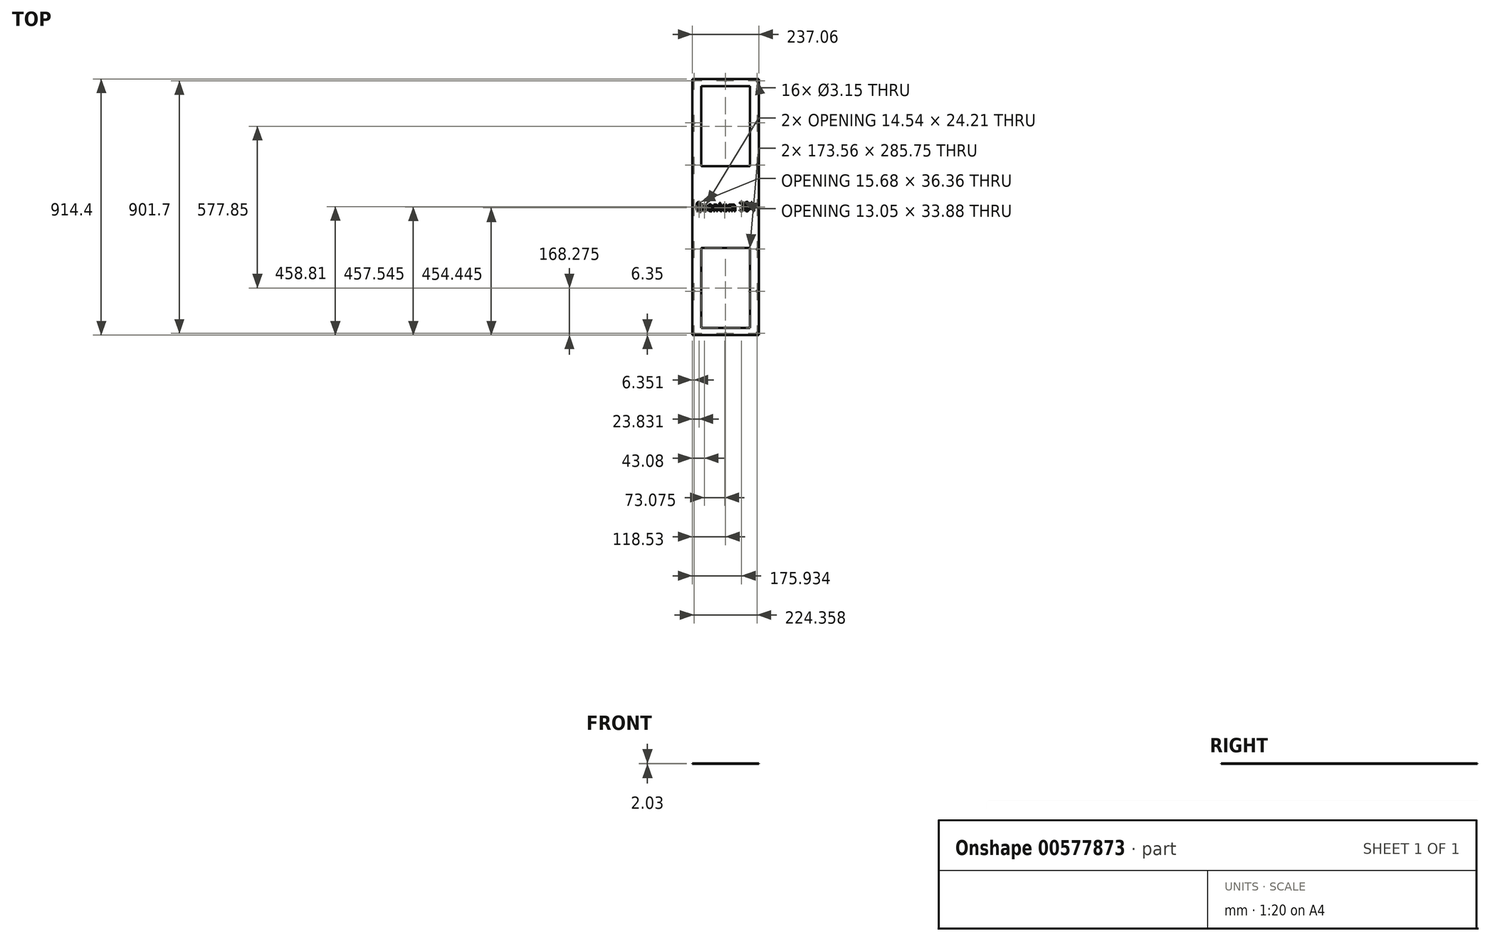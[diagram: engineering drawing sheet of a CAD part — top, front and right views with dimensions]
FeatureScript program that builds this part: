
annotation { "Feature Type Name" : "Feature", "Feature Type Description" : "" }
export const myFeature = defineFeature(function(context is Context, id is Id, definition is map)
    precondition{}
    {
        {
            var Q0;
            Q0=qCreatedBy(makeId("Top.planeOp"),FACE);
            var sketch = newSketch(context, id + "F0", { "sketchPlane" : qUnion([Q0])});
            skLineSegment(sketch, "E0", {"start": v(-118.53, -457.2) * mm, "end": v(118.53, -457.2) * mm});
            skLineSegment(sketch, "E1", {"start": v(-118.53, 457.2) * mm, "end": v(118.53, 457.2) * mm});
            skLineSegment(sketch, "E2", {"start": v(-118.53, 457.2) * mm, "end": v(-118.53, -457.2) * mm});
            skLineSegment(sketch, "E3", {"start": v(118.53, 457.2) * mm, "end": v(118.53, -457.2) * mm});
            skLineSegment(sketch, "E4", {"start": v(-86.78, 431.8) * mm, "end": v(86.78, 431.8) * mm});
            skLineSegment(sketch, "E5", {"start": v(-86.78, 146.05) * mm, "end": v(86.78, 146.05) * mm});
            skLineSegment(sketch, "E6", {"start": v(-86.78, 431.8) * mm, "end": v(-86.78, 146.05) * mm});
            skLineSegment(sketch, "E7", {"start": v(86.78, 431.8) * mm, "end": v(86.78, 146.05) * mm});
            skLineSegment(sketch, "E8", {"start": v(-86.78, -146.05) * mm, "end": v(86.78, -146.05) * mm});
            skLineSegment(sketch, "E9", {"start": v(-86.78, -431.8) * mm, "end": v(86.78, -431.8) * mm});
            skLineSegment(sketch, "E10", {"start": v(-86.78, -146.05) * mm, "end": v(-86.78, -431.8) * mm});
            skLineSegment(sketch, "E11", {"start": v(86.78, -146.05) * mm, "end": v(86.78, -431.8) * mm});
            skCircle(sketch, "E12", {"center": v(-112.18, 450.85) * mm, "radius": 1.58 * mm});
            skCircle(sketch, "E13", {"center": v(-112.18, -450.85) * mm, "radius": 1.58 * mm});
            skCircle(sketch, "E14", {"center": v(112.18, -450.85) * mm, "radius": 1.58 * mm});
            skCircle(sketch, "E15", {"center": v(112.18, 450.85) * mm, "radius": 1.58 * mm});
            skCircle(sketch, "E16", {"center": v(0, 450.85) * mm, "radius": 1.58 * mm});
            skCircle(sketch, "E17", {"center": v(0, -450.85) * mm, "radius": 1.58 * mm});
            skCircle(sketch, "E18", {"center": v(-112.18, 0) * mm, "radius": 1.58 * mm});
            skCircle(sketch, "E19", {"center": v(112.18, 0) * mm, "radius": 1.58 * mm});
            skCircle(sketch, "E20", {"center": v(-112.18, 300.57) * mm, "radius": 1.58 * mm});
            skCircle(sketch, "E21", {"center": v(-112.18, 150.28) * mm, "radius": 1.58 * mm});
            skCircle(sketch, "E22", {"center": v(112.18, 300.57) * mm, "radius": 1.58 * mm});
            skCircle(sketch, "E23", {"center": v(112.18, 150.28) * mm, "radius": 1.58 * mm});
            skCircle(sketch, "E24", {"center": v(-112.18, -150.28) * mm, "radius": 1.58 * mm});
            skCircle(sketch, "E25", {"center": v(112.18, -150.28) * mm, "radius": 1.58 * mm});
            skCircle(sketch, "E26", {"center": v(112.18, -300.57) * mm, "radius": 1.58 * mm});
            skCircle(sketch, "E27", {"center": v(-112.18, -300.57) * mm, "radius": 1.58 * mm});
            skLineSegment(sketch, "E28", {"start": v(-102.51, 12) * mm, "end": v(-102.41, 12.72) * mm});
            skLineSegment(sketch, "E29", {"start": v(-102.41, 12.72) * mm, "end": v(-102.24, 13.4) * mm});
            skLineSegment(sketch, "E30", {"start": v(-102.24, 13.4) * mm, "end": v(-102.02, 14.06) * mm});
            skLineSegment(sketch, "E31", {"start": v(-102.02, 14.06) * mm, "end": v(-101.7, 14.68) * mm});
            skLineSegment(sketch, "E32", {"start": v(-101.7, 14.68) * mm, "end": v(-101.35, 15.28) * mm});
            skLineSegment(sketch, "E33", {"start": v(-101.35, 15.28) * mm, "end": v(-100.9, 15.85) * mm});
            skLineSegment(sketch, "E34", {"start": v(-100.9, 15.85) * mm, "end": v(-100.4, 16.4) * mm});
            skLineSegment(sketch, "E35", {"start": v(-100.4, 16.4) * mm, "end": v(-99.86, 16.9) * mm});
            skLineSegment(sketch, "E36", {"start": v(-99.86, 16.9) * mm, "end": v(-99.29, 17.34) * mm});
            skLineSegment(sketch, "E37", {"start": v(-99.29, 17.34) * mm, "end": v(-98.7, 17.68) * mm});
            skLineSegment(sketch, "E38", {"start": v(-98.7, 17.68) * mm, "end": v(-98.07, 18) * mm});
            skLineSegment(sketch, "E39", {"start": v(-98.07, 18) * mm, "end": v(-97.4, 18.23) * mm});
            skLineSegment(sketch, "E40", {"start": v(-97.4, 18.23) * mm, "end": v(-96.73, 18.4) * mm});
            skLineSegment(sketch, "E41", {"start": v(-96.73, 18.4) * mm, "end": v(-96.01, 18.5) * mm});
            skLineSegment(sketch, "E42", {"start": v(-96.01, 18.5) * mm, "end": v(-95.27, 18.53) * mm});
            skLineSegment(sketch, "E43", {"start": v(-95.27, 18.53) * mm, "end": v(-94.55, 18.5) * mm});
            skLineSegment(sketch, "E44", {"start": v(-94.55, 18.5) * mm, "end": v(-93.83, 18.4) * mm});
            skLineSegment(sketch, "E45", {"start": v(-93.83, 18.4) * mm, "end": v(-93.16, 18.23) * mm});
            skLineSegment(sketch, "E46", {"start": v(-93.16, 18.23) * mm, "end": v(-92.5, 18) * mm});
            skLineSegment(sketch, "E47", {"start": v(-92.5, 18) * mm, "end": v(-91.87, 17.68) * mm});
            skLineSegment(sketch, "E48", {"start": v(-91.87, 17.68) * mm, "end": v(-91.28, 17.34) * mm});
            skLineSegment(sketch, "E49", {"start": v(-91.28, 17.34) * mm, "end": v(-90.7, 16.9) * mm});
            skLineSegment(sketch, "E50", {"start": v(-90.7, 16.9) * mm, "end": v(-90.16, 16.4) * mm});
            skLineSegment(sketch, "E51", {"start": v(-90.16, 16.4) * mm, "end": v(-89.66, 15.85) * mm});
            skLineSegment(sketch, "E52", {"start": v(-89.66, 15.85) * mm, "end": v(-89.22, 15.28) * mm});
            skLineSegment(sketch, "E53", {"start": v(-89.22, 15.28) * mm, "end": v(-88.87, 14.68) * mm});
            skLineSegment(sketch, "E54", {"start": v(-88.87, 14.68) * mm, "end": v(-88.55, 14.06) * mm});
            skLineSegment(sketch, "E55", {"start": v(-88.55, 14.06) * mm, "end": v(-88.32, 13.4) * mm});
            skLineSegment(sketch, "E56", {"start": v(-88.32, 13.4) * mm, "end": v(-88.15, 12.72) * mm});
            skLineSegment(sketch, "E57", {"start": v(-88.15, 12.72) * mm, "end": v(-88.05, 12) * mm});
            skLineSegment(sketch, "E58", {"start": v(-88.05, 12) * mm, "end": v(-88.03, 11.28) * mm});
            skLineSegment(sketch, "E59", {"start": v(-88.03, 11.28) * mm, "end": v(-88.03, -8.06) * mm});
            skLineSegment(sketch, "E60", {"start": v(-88.03, -8.06) * mm, "end": v(-88.03, -8.29) * mm});
            skLineSegment(sketch, "E61", {"start": v(-88.03, -8.29) * mm, "end": v(-88.03, -8.5) * mm});
            skLineSegment(sketch, "E62", {"start": v(-88.03, -8.5) * mm, "end": v(-88.05, -8.73) * mm});
            skLineSegment(sketch, "E63", {"start": v(-88.05, -8.73) * mm, "end": v(-88.08, -8.96) * mm});
            skLineSegment(sketch, "E64", {"start": v(-88.08, -8.96) * mm, "end": v(-88.1, -9.15) * mm});
            skLineSegment(sketch, "E65", {"start": v(-88.1, -9.15) * mm, "end": v(-88.13, -9.38) * mm});
            skLineSegment(sketch, "E66", {"start": v(-88.13, -9.38) * mm, "end": v(-88.15, -9.58) * mm});
            skLineSegment(sketch, "E67", {"start": v(-88.15, -9.58) * mm, "end": v(-88.2, -9.8) * mm});
            skLineSegment(sketch, "E68", {"start": v(-88.2, -9.8) * mm, "end": v(-88.22, -9.92) * mm});
            skLineSegment(sketch, "E69", {"start": v(-88.22, -9.92) * mm, "end": v(-88.27, -10.07) * mm});
            skLineSegment(sketch, "E70", {"start": v(-88.27, -10.07) * mm, "end": v(-88.32, -10.2) * mm});
            skLineSegment(sketch, "E71", {"start": v(-88.32, -10.2) * mm, "end": v(-88.37, -10.32) * mm});
            skLineSegment(sketch, "E72", {"start": v(-88.37, -10.32) * mm, "end": v(-88.45, -10.42) * mm});
            skLineSegment(sketch, "E73", {"start": v(-88.45, -10.42) * mm, "end": v(-88.52, -10.54) * mm});
            skLineSegment(sketch, "E74", {"start": v(-88.52, -10.54) * mm, "end": v(-88.62, -10.64) * mm});
            skLineSegment(sketch, "E75", {"start": v(-88.62, -10.64) * mm, "end": v(-88.72, -10.77) * mm});
            skLineSegment(sketch, "E76", {"start": v(-88.72, -10.77) * mm, "end": v(-88.87, -10.9) * mm});
            skLineSegment(sketch, "E77", {"start": v(-88.87, -10.9) * mm, "end": v(-89.04, -11.02) * mm});
            skLineSegment(sketch, "E78", {"start": v(-89.04, -11.02) * mm, "end": v(-89.2, -11.11) * mm});
            skLineSegment(sketch, "E79", {"start": v(-89.2, -11.11) * mm, "end": v(-89.37, -11.19) * mm});
            skLineSegment(sketch, "E80", {"start": v(-89.37, -11.19) * mm, "end": v(-89.54, -11.26) * mm});
            skLineSegment(sketch, "E81", {"start": v(-89.54, -11.26) * mm, "end": v(-89.71, -11.31) * mm});
            skLineSegment(sketch, "E82", {"start": v(-89.71, -11.31) * mm, "end": v(-89.91, -11.34) * mm});
            skLineSegment(sketch, "E83", {"start": v(-89.91, -11.34) * mm, "end": v(-90.1, -11.34) * mm});
            skLineSegment(sketch, "E84", {"start": v(-90.1, -11.34) * mm, "end": v(-90.3, -11.34) * mm});
            skLineSegment(sketch, "E85", {"start": v(-90.3, -11.34) * mm, "end": v(-90.48, -11.31) * mm});
            skLineSegment(sketch, "E86", {"start": v(-90.48, -11.31) * mm, "end": v(-90.68, -11.26) * mm});
            skLineSegment(sketch, "E87", {"start": v(-90.68, -11.26) * mm, "end": v(-90.85, -11.19) * mm});
            skLineSegment(sketch, "E88", {"start": v(-90.85, -11.19) * mm, "end": v(-91, -11.11) * mm});
            skLineSegment(sketch, "E89", {"start": v(-91, -11.11) * mm, "end": v(-91.18, -11.02) * mm});
            skLineSegment(sketch, "E90", {"start": v(-91.18, -11.02) * mm, "end": v(-91.33, -10.92) * mm});
            skLineSegment(sketch, "E91", {"start": v(-91.33, -10.92) * mm, "end": v(-91.47, -10.77) * mm});
            skLineSegment(sketch, "E92", {"start": v(-91.47, -10.77) * mm, "end": v(-91.6, -10.62) * mm});
            skLineSegment(sketch, "E93", {"start": v(-91.6, -10.62) * mm, "end": v(-91.72, -10.47) * mm});
            skLineSegment(sketch, "E94", {"start": v(-91.72, -10.47) * mm, "end": v(-91.82, -10.32) * mm});
            skLineSegment(sketch, "E95", {"start": v(-91.82, -10.32) * mm, "end": v(-91.9, -10.15) * mm});
            skLineSegment(sketch, "E96", {"start": v(-91.9, -10.15) * mm, "end": v(-91.97, -9.97) * mm});
            skLineSegment(sketch, "E97", {"start": v(-91.97, -9.97) * mm, "end": v(-92, -9.8) * mm});
            skLineSegment(sketch, "E98", {"start": v(-92, -9.8) * mm, "end": v(-92.02, -9.6) * mm});
            skLineSegment(sketch, "E99", {"start": v(-92.02, -9.6) * mm, "end": v(-92.04, -9.4) * mm});
            skLineSegment(sketch, "E100", {"start": v(-92.04, -9.4) * mm, "end": v(-92.04, -9.35) * mm});
            skLineSegment(sketch, "E101", {"start": v(-92.04, -9.35) * mm, "end": v(-92.04, -9.3) * mm});
            skLineSegment(sketch, "E102", {"start": v(-92.04, -9.3) * mm, "end": v(-92.04, -9.25) * mm});
            skLineSegment(sketch, "E103", {"start": v(-92.04, -9.25) * mm, "end": v(-92.04, -9.2) * mm});
            skLineSegment(sketch, "E104", {"start": v(-92.04, -9.2) * mm, "end": v(-92.02, -9.15) * mm});
            skLineSegment(sketch, "E105", {"start": v(-92.02, -9.15) * mm, "end": v(-92.02, -9.08) * mm});
            skLineSegment(sketch, "E106", {"start": v(-92.02, -9.08) * mm, "end": v(-92.02, -9.03) * mm});
            skLineSegment(sketch, "E107", {"start": v(-92.02, -9.03) * mm, "end": v(-92.02, -8.98) * mm});
            skLineSegment(sketch, "E108", {"start": v(-92.02, -8.98) * mm, "end": v(-92, -8.86) * mm});
            skLineSegment(sketch, "E109", {"start": v(-92, -8.86) * mm, "end": v(-91.97, -8.76) * mm});
            skLineSegment(sketch, "E110", {"start": v(-91.97, -8.76) * mm, "end": v(-91.95, -8.63) * mm});
            skLineSegment(sketch, "E111", {"start": v(-91.95, -8.63) * mm, "end": v(-91.92, -8.53) * mm});
            skLineSegment(sketch, "E112", {"start": v(-91.92, -8.53) * mm, "end": v(-91.92, -8.41) * mm});
            skLineSegment(sketch, "E113", {"start": v(-91.92, -8.41) * mm, "end": v(-91.9, -8.31) * mm});
            skLineSegment(sketch, "E114", {"start": v(-91.9, -8.31) * mm, "end": v(-91.9, -8.19) * mm});
            skLineSegment(sketch, "E115", {"start": v(-91.9, -8.19) * mm, "end": v(-91.9, -8.06) * mm});
            skLineSegment(sketch, "E116", {"start": v(-91.9, -8.06) * mm, "end": v(-91.9, 11.28) * mm});
            skLineSegment(sketch, "E117", {"start": v(-91.9, 11.28) * mm, "end": v(-91.92, 11.6) * mm});
            skLineSegment(sketch, "E118", {"start": v(-91.92, 11.6) * mm, "end": v(-91.95, 11.95) * mm});
            skLineSegment(sketch, "E119", {"start": v(-91.95, 11.95) * mm, "end": v(-92.04, 12.28) * mm});
            skLineSegment(sketch, "E120", {"start": v(-92.04, 12.28) * mm, "end": v(-92.14, 12.57) * mm});
            skLineSegment(sketch, "E121", {"start": v(-92.14, 12.57) * mm, "end": v(-92.3, 12.87) * mm});
            skLineSegment(sketch, "E122", {"start": v(-92.3, 12.87) * mm, "end": v(-92.44, 13.14) * mm});
            skLineSegment(sketch, "E123", {"start": v(-92.44, 13.14) * mm, "end": v(-92.66, 13.42) * mm});
            skLineSegment(sketch, "E124", {"start": v(-92.66, 13.42) * mm, "end": v(-92.89, 13.67) * mm});
            skLineSegment(sketch, "E125", {"start": v(-92.89, 13.67) * mm, "end": v(-93.14, 13.89) * mm});
            skLineSegment(sketch, "E126", {"start": v(-93.14, 13.89) * mm, "end": v(-93.4, 14.11) * mm});
            skLineSegment(sketch, "E127", {"start": v(-93.4, 14.11) * mm, "end": v(-93.68, 14.26) * mm});
            skLineSegment(sketch, "E128", {"start": v(-93.68, 14.26) * mm, "end": v(-93.98, 14.4) * mm});
            skLineSegment(sketch, "E129", {"start": v(-93.98, 14.4) * mm, "end": v(-94.28, 14.5) * mm});
            skLineSegment(sketch, "E130", {"start": v(-94.28, 14.5) * mm, "end": v(-94.6, 14.6) * mm});
            skLineSegment(sketch, "E131", {"start": v(-94.6, 14.6) * mm, "end": v(-94.95, 14.63) * mm});
            skLineSegment(sketch, "E132", {"start": v(-94.95, 14.63) * mm, "end": v(-95.27, 14.66) * mm});
            skLineSegment(sketch, "E133", {"start": v(-95.27, 14.66) * mm, "end": v(-95.62, 14.63) * mm});
            skLineSegment(sketch, "E134", {"start": v(-95.62, 14.63) * mm, "end": v(-95.96, 14.6) * mm});
            skLineSegment(sketch, "E135", {"start": v(-95.96, 14.6) * mm, "end": v(-96.29, 14.5) * mm});
            skLineSegment(sketch, "E136", {"start": v(-96.29, 14.5) * mm, "end": v(-96.58, 14.4) * mm});
            skLineSegment(sketch, "E137", {"start": v(-96.58, 14.4) * mm, "end": v(-96.88, 14.26) * mm});
            skLineSegment(sketch, "E138", {"start": v(-96.88, 14.26) * mm, "end": v(-97.15, 14.11) * mm});
            skLineSegment(sketch, "E139", {"start": v(-97.15, 14.11) * mm, "end": v(-97.43, 13.89) * mm});
            skLineSegment(sketch, "E140", {"start": v(-97.43, 13.89) * mm, "end": v(-97.68, 13.67) * mm});
            skLineSegment(sketch, "E141", {"start": v(-97.68, 13.67) * mm, "end": v(-97.9, 13.42) * mm});
            skLineSegment(sketch, "E142", {"start": v(-97.9, 13.42) * mm, "end": v(-98.12, 13.14) * mm});
            skLineSegment(sketch, "E143", {"start": v(-98.12, 13.14) * mm, "end": v(-98.27, 12.87) * mm});
            skLineSegment(sketch, "E144", {"start": v(-98.27, 12.87) * mm, "end": v(-98.42, 12.57) * mm});
            skLineSegment(sketch, "E145", {"start": v(-98.42, 12.57) * mm, "end": v(-98.52, 12.28) * mm});
            skLineSegment(sketch, "E146", {"start": v(-98.52, 12.28) * mm, "end": v(-98.62, 11.95) * mm});
            skLineSegment(sketch, "E147", {"start": v(-98.62, 11.95) * mm, "end": v(-98.64, 11.6) * mm});
            skLineSegment(sketch, "E148", {"start": v(-98.64, 11.6) * mm, "end": v(-98.67, 11.28) * mm});
            skLineSegment(sketch, "E149", {"start": v(-98.67, 11.28) * mm, "end": v(-98.67, -8.06) * mm});
            skLineSegment(sketch, "E150", {"start": v(-98.67, -8.06) * mm, "end": v(-98.64, -8.41) * mm});
            skLineSegment(sketch, "E151", {"start": v(-98.64, -8.41) * mm, "end": v(-98.62, -8.73) * mm});
            skLineSegment(sketch, "E152", {"start": v(-98.62, -8.73) * mm, "end": v(-98.54, -9.03) * mm});
            skLineSegment(sketch, "E153", {"start": v(-98.54, -9.03) * mm, "end": v(-98.44, -9.33) * mm});
            skLineSegment(sketch, "E154", {"start": v(-98.44, -9.33) * mm, "end": v(-98.3, -9.6) * mm});
            skLineSegment(sketch, "E155", {"start": v(-98.3, -9.6) * mm, "end": v(-98.15, -9.85) * mm});
            skLineSegment(sketch, "E156", {"start": v(-98.15, -9.85) * mm, "end": v(-97.95, -10.1) * mm});
            skLineSegment(sketch, "E157", {"start": v(-97.95, -10.1) * mm, "end": v(-97.72, -10.32) * mm});
            skLineSegment(sketch, "E158", {"start": v(-97.72, -10.32) * mm, "end": v(-97.5, -10.52) * mm});
            skLineSegment(sketch, "E159", {"start": v(-97.5, -10.52) * mm, "end": v(-97.25, -10.72) * mm});
            skLineSegment(sketch, "E160", {"start": v(-97.25, -10.72) * mm, "end": v(-97, -10.9) * mm});
            skLineSegment(sketch, "E161", {"start": v(-97, -10.9) * mm, "end": v(-96.73, -11.04) * mm});
            skLineSegment(sketch, "E162", {"start": v(-96.73, -11.04) * mm, "end": v(-96.48, -11.16) * mm});
            skLineSegment(sketch, "E163", {"start": v(-96.48, -11.16) * mm, "end": v(-96.19, -11.29) * mm});
            skLineSegment(sketch, "E164", {"start": v(-96.19, -11.29) * mm, "end": v(-95.91, -11.39) * mm});
            skLineSegment(sketch, "E165", {"start": v(-95.91, -11.39) * mm, "end": v(-95.62, -11.49) * mm});
            skLineSegment(sketch, "E166", {"start": v(-95.62, -11.49) * mm, "end": v(-88.2, -14.07) * mm});
            skLineSegment(sketch, "E167", {"start": v(-88.2, -14.07) * mm, "end": v(-88, -14.14) * mm});
            skLineSegment(sketch, "E168", {"start": v(-88, -14.14) * mm, "end": v(-87.83, -14.24) * mm});
            skLineSegment(sketch, "E169", {"start": v(-87.83, -14.24) * mm, "end": v(-87.68, -14.34) * mm});
            skLineSegment(sketch, "E170", {"start": v(-87.68, -14.34) * mm, "end": v(-87.53, -14.46) * mm});
            skLineSegment(sketch, "E171", {"start": v(-87.53, -14.46) * mm, "end": v(-87.38, -14.59) * mm});
            skLineSegment(sketch, "E172", {"start": v(-87.38, -14.59) * mm, "end": v(-87.26, -14.74) * mm});
            skLineSegment(sketch, "E173", {"start": v(-87.26, -14.74) * mm, "end": v(-87.16, -14.88) * mm});
            skLineSegment(sketch, "E174", {"start": v(-87.16, -14.88) * mm, "end": v(-87.06, -15.06) * mm});
            skLineSegment(sketch, "E175", {"start": v(-87.06, -15.06) * mm, "end": v(-87, -15.18) * mm});
            skLineSegment(sketch, "E176", {"start": v(-87, -15.18) * mm, "end": v(-86.98, -15.28) * mm});
            skLineSegment(sketch, "E177", {"start": v(-86.98, -15.28) * mm, "end": v(-86.93, -15.38) * mm});
            skLineSegment(sketch, "E178", {"start": v(-86.93, -15.38) * mm, "end": v(-86.91, -15.5) * mm});
            skLineSegment(sketch, "E179", {"start": v(-86.91, -15.5) * mm, "end": v(-86.89, -15.6) * mm});
            skLineSegment(sketch, "E180", {"start": v(-86.89, -15.6) * mm, "end": v(-86.89, -15.7) * mm});
            skLineSegment(sketch, "E181", {"start": v(-86.89, -15.7) * mm, "end": v(-86.86, -15.8) * mm});
            skLineSegment(sketch, "E182", {"start": v(-86.86, -15.8) * mm, "end": v(-86.86, -15.9) * mm});
            skLineSegment(sketch, "E183", {"start": v(-86.86, -15.9) * mm, "end": v(-86.86, -15.98) * mm});
            skLineSegment(sketch, "E184", {"start": v(-86.86, -15.98) * mm, "end": v(-86.86, -16.05) * mm});
            skLineSegment(sketch, "E185", {"start": v(-86.86, -16.05) * mm, "end": v(-86.89, -16.13) * mm});
            skLineSegment(sketch, "E186", {"start": v(-86.89, -16.13) * mm, "end": v(-86.89, -16.2) * mm});
            skLineSegment(sketch, "E187", {"start": v(-86.89, -16.2) * mm, "end": v(-86.91, -16.27) * mm});
            skLineSegment(sketch, "E188", {"start": v(-86.91, -16.27) * mm, "end": v(-86.91, -16.35) * mm});
            skLineSegment(sketch, "E189", {"start": v(-86.91, -16.35) * mm, "end": v(-86.93, -16.45) * mm});
            skLineSegment(sketch, "E190", {"start": v(-86.93, -16.45) * mm, "end": v(-86.96, -16.52) * mm});
            skLineSegment(sketch, "E191", {"start": v(-86.96, -16.52) * mm, "end": v(-87.03, -16.7) * mm});
            skLineSegment(sketch, "E192", {"start": v(-87.03, -16.7) * mm, "end": v(-87.13, -16.87) * mm});
            skLineSegment(sketch, "E193", {"start": v(-87.13, -16.87) * mm, "end": v(-87.23, -17.04) * mm});
            skLineSegment(sketch, "E194", {"start": v(-87.23, -17.04) * mm, "end": v(-87.33, -17.2) * mm});
            skLineSegment(sketch, "E195", {"start": v(-87.33, -17.2) * mm, "end": v(-87.48, -17.32) * mm});
            skLineSegment(sketch, "E196", {"start": v(-87.48, -17.32) * mm, "end": v(-87.63, -17.44) * mm});
            skLineSegment(sketch, "E197", {"start": v(-87.63, -17.44) * mm, "end": v(-87.78, -17.56) * mm});
            skLineSegment(sketch, "E198", {"start": v(-87.78, -17.56) * mm, "end": v(-87.95, -17.66) * mm});
            skLineSegment(sketch, "E199", {"start": v(-87.95, -17.66) * mm, "end": v(-88.05, -17.69) * mm});
            skLineSegment(sketch, "E200", {"start": v(-88.05, -17.69) * mm, "end": v(-88.18, -17.74) * mm});
            skLineSegment(sketch, "E201", {"start": v(-88.18, -17.74) * mm, "end": v(-88.27, -17.76) * mm});
            skLineSegment(sketch, "E202", {"start": v(-88.27, -17.76) * mm, "end": v(-88.37, -17.79) * mm});
            skLineSegment(sketch, "E203", {"start": v(-88.37, -17.79) * mm, "end": v(-88.5, -17.81) * mm});
            skLineSegment(sketch, "E204", {"start": v(-88.5, -17.81) * mm, "end": v(-88.6, -17.84) * mm});
            skLineSegment(sketch, "E205", {"start": v(-88.6, -17.84) * mm, "end": v(-88.7, -17.84) * mm});
            skLineSegment(sketch, "E206", {"start": v(-88.7, -17.84) * mm, "end": v(-88.8, -17.84) * mm});
            skLineSegment(sketch, "E207", {"start": v(-88.8, -17.84) * mm, "end": v(-88.87, -17.84) * mm});
            skLineSegment(sketch, "E208", {"start": v(-88.87, -17.84) * mm, "end": v(-88.97, -17.84) * mm});
            skLineSegment(sketch, "E209", {"start": v(-88.97, -17.84) * mm, "end": v(-89.04, -17.84) * mm});
            skLineSegment(sketch, "E210", {"start": v(-89.04, -17.84) * mm, "end": v(-89.12, -17.81) * mm});
            skLineSegment(sketch, "E211", {"start": v(-89.12, -17.81) * mm, "end": v(-89.2, -17.81) * mm});
            skLineSegment(sketch, "E212", {"start": v(-89.2, -17.81) * mm, "end": v(-89.27, -17.79) * mm});
            skLineSegment(sketch, "E213", {"start": v(-89.27, -17.79) * mm, "end": v(-89.34, -17.76) * mm});
            skLineSegment(sketch, "E214", {"start": v(-89.34, -17.76) * mm, "end": v(-89.44, -17.74) * mm});
            skLineSegment(sketch, "E215", {"start": v(-89.44, -17.74) * mm, "end": v(-97.2, -15.08) * mm});
            skLineSegment(sketch, "E216", {"start": v(-97.2, -15.08) * mm, "end": v(-97.7, -14.9) * mm});
            skLineSegment(sketch, "E217", {"start": v(-97.7, -14.9) * mm, "end": v(-98.15, -14.71) * mm});
            skLineSegment(sketch, "E218", {"start": v(-98.15, -14.71) * mm, "end": v(-98.6, -14.49) * mm});
            skLineSegment(sketch, "E219", {"start": v(-98.6, -14.49) * mm, "end": v(-98.99, -14.26) * mm});
            skLineSegment(sketch, "E220", {"start": v(-98.99, -14.26) * mm, "end": v(-99.39, -14.02) * mm});
            skLineSegment(sketch, "E221", {"start": v(-99.39, -14.02) * mm, "end": v(-99.76, -13.77) * mm});
            skLineSegment(sketch, "E222", {"start": v(-99.76, -13.77) * mm, "end": v(-100.08, -13.5) * mm});
            skLineSegment(sketch, "E223", {"start": v(-100.08, -13.5) * mm, "end": v(-100.4, -13.2) * mm});
            skLineSegment(sketch, "E224", {"start": v(-100.4, -13.2) * mm, "end": v(-100.9, -12.65) * mm});
            skLineSegment(sketch, "E225", {"start": v(-100.9, -12.65) * mm, "end": v(-101.35, -12.08) * mm});
            skLineSegment(sketch, "E226", {"start": v(-101.35, -12.08) * mm, "end": v(-101.7, -11.49) * mm});
            skLineSegment(sketch, "E227", {"start": v(-101.7, -11.49) * mm, "end": v(-102.02, -10.87) * mm});
            skLineSegment(sketch, "E228", {"start": v(-102.02, -10.87) * mm, "end": v(-102.24, -10.2) * mm});
            skLineSegment(sketch, "E229", {"start": v(-102.24, -10.2) * mm, "end": v(-102.41, -9.53) * mm});
            skLineSegment(sketch, "E230", {"start": v(-102.41, -9.53) * mm, "end": v(-102.51, -8.8) * mm});
            skLineSegment(sketch, "E231", {"start": v(-102.51, -8.8) * mm, "end": v(-102.54, -8.06) * mm});
            skLineSegment(sketch, "E232", {"start": v(-102.54, -8.06) * mm, "end": v(-102.54, 11.28) * mm});
            skLineSegment(sketch, "E233", {"start": v(-102.54, 11.28) * mm, "end": v(-102.51, 12) * mm});
            skLineSegment(sketch, "E234", {"start": v(-82.67, -8.34) * mm, "end": v(-82.72, -7.6) * mm});
            skLineSegment(sketch, "E235", {"start": v(-82.72, -7.6) * mm, "end": v(-82.72, 7.41) * mm});
            skLineSegment(sketch, "E236", {"start": v(-82.72, 7.41) * mm, "end": v(-82.7, 7.59) * mm});
            skLineSegment(sketch, "E237", {"start": v(-82.7, 7.59) * mm, "end": v(-82.67, 7.79) * mm});
            skLineSegment(sketch, "E238", {"start": v(-82.67, 7.79) * mm, "end": v(-82.62, 7.96) * mm});
            skLineSegment(sketch, "E239", {"start": v(-82.62, 7.96) * mm, "end": v(-82.57, 8.13) * mm});
            skLineSegment(sketch, "E240", {"start": v(-82.57, 8.13) * mm, "end": v(-82.5, 8.3) * mm});
            skLineSegment(sketch, "E241", {"start": v(-82.5, 8.3) * mm, "end": v(-82.4, 8.48) * mm});
            skLineSegment(sketch, "E242", {"start": v(-82.4, 8.48) * mm, "end": v(-82.27, 8.63) * mm});
            skLineSegment(sketch, "E243", {"start": v(-82.27, 8.63) * mm, "end": v(-82.15, 8.78) * mm});
            skLineSegment(sketch, "E244", {"start": v(-82.15, 8.78) * mm, "end": v(-82, 8.9) * mm});
            skLineSegment(sketch, "E245", {"start": v(-82, 8.9) * mm, "end": v(-81.85, 9.03) * mm});
            skLineSegment(sketch, "E246", {"start": v(-81.85, 9.03) * mm, "end": v(-81.68, 9.13) * mm});
            skLineSegment(sketch, "E247", {"start": v(-81.68, 9.13) * mm, "end": v(-81.5, 9.2) * mm});
            skLineSegment(sketch, "E248", {"start": v(-81.5, 9.2) * mm, "end": v(-81.33, 9.25) * mm});
            skLineSegment(sketch, "E249", {"start": v(-81.33, 9.25) * mm, "end": v(-81.16, 9.3) * mm});
            skLineSegment(sketch, "E250", {"start": v(-81.16, 9.3) * mm, "end": v(-80.96, 9.32) * mm});
            skLineSegment(sketch, "E251", {"start": v(-80.96, 9.32) * mm, "end": v(-80.78, 9.35) * mm});
            skLineSegment(sketch, "E252", {"start": v(-80.78, 9.35) * mm, "end": v(-80.58, 9.32) * mm});
            skLineSegment(sketch, "E253", {"start": v(-80.58, 9.32) * mm, "end": v(-80.39, 9.3) * mm});
            skLineSegment(sketch, "E254", {"start": v(-80.39, 9.3) * mm, "end": v(-80.21, 9.25) * mm});
            skLineSegment(sketch, "E255", {"start": v(-80.21, 9.25) * mm, "end": v(-80.04, 9.2) * mm});
            skLineSegment(sketch, "E256", {"start": v(-80.04, 9.2) * mm, "end": v(-79.87, 9.13) * mm});
            skLineSegment(sketch, "E257", {"start": v(-79.87, 9.13) * mm, "end": v(-79.7, 9.03) * mm});
            skLineSegment(sketch, "E258", {"start": v(-79.7, 9.03) * mm, "end": v(-79.54, 8.9) * mm});
            skLineSegment(sketch, "E259", {"start": v(-79.54, 8.9) * mm, "end": v(-79.4, 8.78) * mm});
            skLineSegment(sketch, "E260", {"start": v(-79.4, 8.78) * mm, "end": v(-79.27, 8.63) * mm});
            skLineSegment(sketch, "E261", {"start": v(-79.27, 8.63) * mm, "end": v(-79.15, 8.48) * mm});
            skLineSegment(sketch, "E262", {"start": v(-79.15, 8.48) * mm, "end": v(-79.05, 8.3) * mm});
            skLineSegment(sketch, "E263", {"start": v(-79.05, 8.3) * mm, "end": v(-78.97, 8.13) * mm});
            skLineSegment(sketch, "E264", {"start": v(-78.97, 8.13) * mm, "end": v(-78.92, 7.96) * mm});
            skLineSegment(sketch, "E265", {"start": v(-78.92, 7.96) * mm, "end": v(-78.87, 7.79) * mm});
            skLineSegment(sketch, "E266", {"start": v(-78.87, 7.79) * mm, "end": v(-78.85, 7.59) * mm});
            skLineSegment(sketch, "E267", {"start": v(-78.85, 7.59) * mm, "end": v(-78.85, 7.41) * mm});
            skLineSegment(sketch, "E268", {"start": v(-78.85, 7.41) * mm, "end": v(-78.85, -7.6) * mm});
            skLineSegment(sketch, "E269", {"start": v(-78.85, -7.6) * mm, "end": v(-78.82, -7.94) * mm});
            skLineSegment(sketch, "E270", {"start": v(-78.82, -7.94) * mm, "end": v(-78.77, -8.26) * mm});
            skLineSegment(sketch, "E271", {"start": v(-78.77, -8.26) * mm, "end": v(-78.7, -8.58) * mm});
            skLineSegment(sketch, "E272", {"start": v(-78.7, -8.58) * mm, "end": v(-78.6, -8.88) * mm});
            skLineSegment(sketch, "E273", {"start": v(-78.6, -8.88) * mm, "end": v(-78.45, -9.18) * mm});
            skLineSegment(sketch, "E274", {"start": v(-78.45, -9.18) * mm, "end": v(-78.28, -9.45) * mm});
            skLineSegment(sketch, "E275", {"start": v(-78.28, -9.45) * mm, "end": v(-78.08, -9.73) * mm});
            skLineSegment(sketch, "E276", {"start": v(-78.08, -9.73) * mm, "end": v(-77.86, -10) * mm});
            skLineSegment(sketch, "E277", {"start": v(-77.86, -10) * mm, "end": v(-77.58, -10.22) * mm});
            skLineSegment(sketch, "E278", {"start": v(-77.58, -10.22) * mm, "end": v(-77.31, -10.42) * mm});
            skLineSegment(sketch, "E279", {"start": v(-77.31, -10.42) * mm, "end": v(-77.04, -10.6) * mm});
            skLineSegment(sketch, "E280", {"start": v(-77.04, -10.6) * mm, "end": v(-76.74, -10.74) * mm});
            skLineSegment(sketch, "E281", {"start": v(-76.74, -10.74) * mm, "end": v(-76.44, -10.84) * mm});
            skLineSegment(sketch, "E282", {"start": v(-76.44, -10.84) * mm, "end": v(-76.12, -10.92) * mm});
            skLineSegment(sketch, "E283", {"start": v(-76.12, -10.92) * mm, "end": v(-75.8, -10.97) * mm});
            skLineSegment(sketch, "E284", {"start": v(-75.8, -10.97) * mm, "end": v(-75.45, -11) * mm});
            skLineSegment(sketch, "E285", {"start": v(-75.45, -11) * mm, "end": v(-72.05, -11) * mm});
            skLineSegment(sketch, "E286", {"start": v(-72.05, -11) * mm, "end": v(-72.05, 7.41) * mm});
            skLineSegment(sketch, "E287", {"start": v(-72.05, 7.41) * mm, "end": v(-72.05, 7.59) * mm});
            skLineSegment(sketch, "E288", {"start": v(-72.05, 7.59) * mm, "end": v(-72.03, 7.79) * mm});
            skLineSegment(sketch, "E289", {"start": v(-72.03, 7.79) * mm, "end": v(-71.98, 7.96) * mm});
            skLineSegment(sketch, "E290", {"start": v(-71.98, 7.96) * mm, "end": v(-71.93, 8.13) * mm});
            skLineSegment(sketch, "E291", {"start": v(-71.93, 8.13) * mm, "end": v(-71.85, 8.3) * mm});
            skLineSegment(sketch, "E292", {"start": v(-71.85, 8.3) * mm, "end": v(-71.75, 8.48) * mm});
            skLineSegment(sketch, "E293", {"start": v(-71.75, 8.48) * mm, "end": v(-71.63, 8.63) * mm});
            skLineSegment(sketch, "E294", {"start": v(-71.63, 8.63) * mm, "end": v(-71.5, 8.78) * mm});
            skLineSegment(sketch, "E295", {"start": v(-71.5, 8.78) * mm, "end": v(-71.36, 8.9) * mm});
            skLineSegment(sketch, "E296", {"start": v(-71.36, 8.9) * mm, "end": v(-71.2, 9.03) * mm});
            skLineSegment(sketch, "E297", {"start": v(-71.2, 9.03) * mm, "end": v(-71.04, 9.13) * mm});
            skLineSegment(sketch, "E298", {"start": v(-71.04, 9.13) * mm, "end": v(-70.86, 9.2) * mm});
            skLineSegment(sketch, "E299", {"start": v(-70.86, 9.2) * mm, "end": v(-70.69, 9.25) * mm});
            skLineSegment(sketch, "E300", {"start": v(-70.69, 9.25) * mm, "end": v(-70.51, 9.3) * mm});
            skLineSegment(sketch, "E301", {"start": v(-70.51, 9.3) * mm, "end": v(-70.32, 9.32) * mm});
            skLineSegment(sketch, "E302", {"start": v(-70.32, 9.32) * mm, "end": v(-70.12, 9.35) * mm});
            skLineSegment(sketch, "E303", {"start": v(-70.12, 9.35) * mm, "end": v(-69.94, 9.32) * mm});
            skLineSegment(sketch, "E304", {"start": v(-69.94, 9.32) * mm, "end": v(-69.75, 9.3) * mm});
            skLineSegment(sketch, "E305", {"start": v(-69.75, 9.3) * mm, "end": v(-69.57, 9.25) * mm});
            skLineSegment(sketch, "E306", {"start": v(-69.57, 9.25) * mm, "end": v(-69.4, 9.2) * mm});
            skLineSegment(sketch, "E307", {"start": v(-69.4, 9.2) * mm, "end": v(-69.22, 9.13) * mm});
            skLineSegment(sketch, "E308", {"start": v(-69.22, 9.13) * mm, "end": v(-69.05, 9.03) * mm});
            skLineSegment(sketch, "E309", {"start": v(-69.05, 9.03) * mm, "end": v(-68.9, 8.9) * mm});
            skLineSegment(sketch, "E310", {"start": v(-68.9, 8.9) * mm, "end": v(-68.75, 8.78) * mm});
            skLineSegment(sketch, "E311", {"start": v(-68.75, 8.78) * mm, "end": v(-68.63, 8.63) * mm});
            skLineSegment(sketch, "E312", {"start": v(-68.63, 8.63) * mm, "end": v(-68.5, 8.48) * mm});
            skLineSegment(sketch, "E313", {"start": v(-68.5, 8.48) * mm, "end": v(-68.4, 8.3) * mm});
            skLineSegment(sketch, "E314", {"start": v(-68.4, 8.3) * mm, "end": v(-68.33, 8.13) * mm});
            skLineSegment(sketch, "E315", {"start": v(-68.33, 8.13) * mm, "end": v(-68.28, 7.96) * mm});
            skLineSegment(sketch, "E316", {"start": v(-68.28, 7.96) * mm, "end": v(-68.23, 7.79) * mm});
            skLineSegment(sketch, "E317", {"start": v(-68.23, 7.79) * mm, "end": v(-68.2, 7.59) * mm});
            skLineSegment(sketch, "E318", {"start": v(-68.2, 7.59) * mm, "end": v(-68.18, 7.41) * mm});
            skLineSegment(sketch, "E319", {"start": v(-68.18, 7.41) * mm, "end": v(-68.18, -12.93) * mm});
            skLineSegment(sketch, "E320", {"start": v(-68.18, -12.93) * mm, "end": v(-68.2, -13.1) * mm});
            skLineSegment(sketch, "E321", {"start": v(-68.2, -13.1) * mm, "end": v(-68.23, -13.3) * mm});
            skLineSegment(sketch, "E322", {"start": v(-68.23, -13.3) * mm, "end": v(-68.28, -13.47) * mm});
            skLineSegment(sketch, "E323", {"start": v(-68.28, -13.47) * mm, "end": v(-68.33, -13.64) * mm});
            skLineSegment(sketch, "E324", {"start": v(-68.33, -13.64) * mm, "end": v(-68.4, -13.82) * mm});
            skLineSegment(sketch, "E325", {"start": v(-68.4, -13.82) * mm, "end": v(-68.5, -14) * mm});
            skLineSegment(sketch, "E326", {"start": v(-68.5, -14) * mm, "end": v(-68.63, -14.14) * mm});
            skLineSegment(sketch, "E327", {"start": v(-68.63, -14.14) * mm, "end": v(-68.75, -14.29) * mm});
            skLineSegment(sketch, "E328", {"start": v(-68.75, -14.29) * mm, "end": v(-68.9, -14.41) * mm});
            skLineSegment(sketch, "E329", {"start": v(-68.9, -14.41) * mm, "end": v(-69.05, -14.54) * mm});
            skLineSegment(sketch, "E330", {"start": v(-69.05, -14.54) * mm, "end": v(-69.22, -14.64) * mm});
            skLineSegment(sketch, "E331", {"start": v(-69.22, -14.64) * mm, "end": v(-69.4, -14.71) * mm});
            skLineSegment(sketch, "E332", {"start": v(-69.4, -14.71) * mm, "end": v(-69.57, -14.76) * mm});
            skLineSegment(sketch, "E333", {"start": v(-69.57, -14.76) * mm, "end": v(-69.75, -14.81) * mm});
            skLineSegment(sketch, "E334", {"start": v(-69.75, -14.81) * mm, "end": v(-69.94, -14.84) * mm});
            skLineSegment(sketch, "E335", {"start": v(-69.94, -14.84) * mm, "end": v(-70.12, -14.86) * mm});
            skLineSegment(sketch, "E336", {"start": v(-70.12, -14.86) * mm, "end": v(-75.45, -14.86) * mm});
            skLineSegment(sketch, "E337", {"start": v(-75.45, -14.86) * mm, "end": v(-76.2, -14.81) * mm});
            skLineSegment(sketch, "E338", {"start": v(-76.2, -14.81) * mm, "end": v(-76.89, -14.71) * mm});
            skLineSegment(sketch, "E339", {"start": v(-76.89, -14.71) * mm, "end": v(-77.58, -14.54) * mm});
            skLineSegment(sketch, "E340", {"start": v(-77.58, -14.54) * mm, "end": v(-78.23, -14.31) * mm});
            skLineSegment(sketch, "E341", {"start": v(-78.23, -14.31) * mm, "end": v(-78.85, -14.02) * mm});
            skLineSegment(sketch, "E342", {"start": v(-78.85, -14.02) * mm, "end": v(-79.47, -13.64) * mm});
            skLineSegment(sketch, "E343", {"start": v(-79.47, -13.64) * mm, "end": v(-80.04, -13.22) * mm});
            skLineSegment(sketch, "E344", {"start": v(-80.04, -13.22) * mm, "end": v(-80.58, -12.73) * mm});
            skLineSegment(sketch, "E345", {"start": v(-80.58, -12.73) * mm, "end": v(-81.08, -12.18) * mm});
            skLineSegment(sketch, "E346", {"start": v(-81.08, -12.18) * mm, "end": v(-81.5, -11.61) * mm});
            skLineSegment(sketch, "E347", {"start": v(-81.5, -11.61) * mm, "end": v(-81.87, -11) * mm});
            skLineSegment(sketch, "E348", {"start": v(-81.87, -11) * mm, "end": v(-82.17, -10.37) * mm});
            skLineSegment(sketch, "E349", {"start": v(-82.17, -10.37) * mm, "end": v(-82.4, -9.73) * mm});
            skLineSegment(sketch, "E350", {"start": v(-82.4, -9.73) * mm, "end": v(-82.57, -9.03) * mm});
            skLineSegment(sketch, "E351", {"start": v(-82.57, -9.03) * mm, "end": v(-82.67, -8.34) * mm});
            skLineSegment(sketch, "E352", {"start": v(-62.35, -4.89) * mm, "end": v(-62.25, -4.2) * mm});
            skLineSegment(sketch, "E353", {"start": v(-62.25, -4.2) * mm, "end": v(-62.08, -3.5) * mm});
            skLineSegment(sketch, "E354", {"start": v(-62.08, -3.5) * mm, "end": v(-61.86, -2.85) * mm});
            skLineSegment(sketch, "E355", {"start": v(-61.86, -2.85) * mm, "end": v(-61.53, -2.23) * mm});
            skLineSegment(sketch, "E356", {"start": v(-61.53, -2.23) * mm, "end": v(-61.19, -1.61) * mm});
            skLineSegment(sketch, "E357", {"start": v(-61.19, -1.61) * mm, "end": v(-60.74, -1.04) * mm});
            skLineSegment(sketch, "E358", {"start": v(-60.74, -1.04) * mm, "end": v(-60.25, -0.5) * mm});
            skLineSegment(sketch, "E359", {"start": v(-60.25, -0.5) * mm, "end": v(-59.77, -0.05) * mm});
            skLineSegment(sketch, "E360", {"start": v(-59.77, -0.05) * mm, "end": v(-59.25, 0.32) * mm});
            skLineSegment(sketch, "E361", {"start": v(-59.25, 0.32) * mm, "end": v(-58.73, 0.67) * mm});
            skLineSegment(sketch, "E362", {"start": v(-58.73, 0.67) * mm, "end": v(-58.19, 0.97) * mm});
            skLineSegment(sketch, "E363", {"start": v(-58.19, 0.97) * mm, "end": v(-57.62, 1.19) * mm});
            skLineSegment(sketch, "E364", {"start": v(-57.62, 1.19) * mm, "end": v(-57.02, 1.39) * mm});
            skLineSegment(sketch, "E365", {"start": v(-57.02, 1.39) * mm, "end": v(-56.4, 1.51) * mm});
            skLineSegment(sketch, "E366", {"start": v(-56.4, 1.51) * mm, "end": v(-55.78, 1.61) * mm});
            skLineSegment(sketch, "E367", {"start": v(-55.78, 1.61) * mm, "end": v(-55.53, 1.59) * mm});
            skLineSegment(sketch, "E368", {"start": v(-55.53, 1.59) * mm, "end": v(-55.3, 1.56) * mm});
            skLineSegment(sketch, "E369", {"start": v(-55.3, 1.56) * mm, "end": v(-55.11, 1.51) * mm});
            skLineSegment(sketch, "E370", {"start": v(-55.11, 1.51) * mm, "end": v(-54.91, 1.46) * mm});
            skLineSegment(sketch, "E371", {"start": v(-54.91, 1.46) * mm, "end": v(-54.71, 1.36) * mm});
            skLineSegment(sketch, "E372", {"start": v(-54.71, 1.36) * mm, "end": v(-54.54, 1.26) * mm});
            skLineSegment(sketch, "E373", {"start": v(-54.54, 1.26) * mm, "end": v(-54.4, 1.16) * mm});
            skLineSegment(sketch, "E374", {"start": v(-54.4, 1.16) * mm, "end": v(-54.24, 1.02) * mm});
            skLineSegment(sketch, "E375", {"start": v(-54.24, 1.02) * mm, "end": v(-54.12, 0.87) * mm});
            skLineSegment(sketch, "E376", {"start": v(-54.12, 0.87) * mm, "end": v(-54, 0.72) * mm});
            skLineSegment(sketch, "E377", {"start": v(-54, 0.72) * mm, "end": v(-53.9, 0.54) * mm});
            skLineSegment(sketch, "E378", {"start": v(-53.9, 0.54) * mm, "end": v(-53.82, 0.4) * mm});
            skLineSegment(sketch, "E379", {"start": v(-53.82, 0.4) * mm, "end": v(-53.75, 0.22) * mm});
            skLineSegment(sketch, "E380", {"start": v(-53.75, 0.22) * mm, "end": v(-53.7, 0.05) * mm});
            skLineSegment(sketch, "E381", {"start": v(-53.7, 0.05) * mm, "end": v(-53.67, -0.15) * mm});
            skLineSegment(sketch, "E382", {"start": v(-53.67, -0.15) * mm, "end": v(-53.67, -0.32) * mm});
            skLineSegment(sketch, "E383", {"start": v(-53.67, -0.32) * mm, "end": v(-53.67, -0.52) * mm});
            skLineSegment(sketch, "E384", {"start": v(-53.67, -0.52) * mm, "end": v(-53.7, -0.72) * mm});
            skLineSegment(sketch, "E385", {"start": v(-53.7, -0.72) * mm, "end": v(-53.75, -0.9) * mm});
            skLineSegment(sketch, "E386", {"start": v(-53.75, -0.9) * mm, "end": v(-53.82, -1.07) * mm});
            skLineSegment(sketch, "E387", {"start": v(-53.82, -1.07) * mm, "end": v(-53.9, -1.24) * mm});
            skLineSegment(sketch, "E388", {"start": v(-53.9, -1.24) * mm, "end": v(-54, -1.4) * mm});
            skLineSegment(sketch, "E389", {"start": v(-54, -1.4) * mm, "end": v(-54.1, -1.54) * mm});
            skLineSegment(sketch, "E390", {"start": v(-54.1, -1.54) * mm, "end": v(-54.22, -1.69) * mm});
            skLineSegment(sketch, "E391", {"start": v(-54.22, -1.69) * mm, "end": v(-54.37, -1.81) * mm});
            skLineSegment(sketch, "E392", {"start": v(-54.37, -1.81) * mm, "end": v(-54.5, -1.91) * mm});
            skLineSegment(sketch, "E393", {"start": v(-54.5, -1.91) * mm, "end": v(-54.64, -2.01) * mm});
            skLineSegment(sketch, "E394", {"start": v(-54.64, -2.01) * mm, "end": v(-54.79, -2.09) * mm});
            skLineSegment(sketch, "E395", {"start": v(-54.79, -2.09) * mm, "end": v(-54.94, -2.16) * mm});
            skLineSegment(sketch, "E396", {"start": v(-54.94, -2.16) * mm, "end": v(-55.09, -2.2) * mm});
            skLineSegment(sketch, "E397", {"start": v(-55.09, -2.2) * mm, "end": v(-55.23, -2.23) * mm});
            skLineSegment(sketch, "E398", {"start": v(-55.23, -2.23) * mm, "end": v(-55.4, -2.26) * mm});
            skLineSegment(sketch, "E399", {"start": v(-55.4, -2.26) * mm, "end": v(-55.7, -2.3) * mm});
            skLineSegment(sketch, "E400", {"start": v(-55.7, -2.3) * mm, "end": v(-56, -2.36) * mm});
            skLineSegment(sketch, "E401", {"start": v(-56, -2.36) * mm, "end": v(-56.28, -2.43) * mm});
            skLineSegment(sketch, "E402", {"start": v(-56.28, -2.43) * mm, "end": v(-56.55, -2.56) * mm});
            skLineSegment(sketch, "E403", {"start": v(-56.55, -2.56) * mm, "end": v(-56.8, -2.68) * mm});
            skLineSegment(sketch, "E404", {"start": v(-56.8, -2.68) * mm, "end": v(-57.05, -2.85) * mm});
            skLineSegment(sketch, "E405", {"start": v(-57.05, -2.85) * mm, "end": v(-57.3, -3.03) * mm});
            skLineSegment(sketch, "E406", {"start": v(-57.3, -3.03) * mm, "end": v(-57.52, -3.25) * mm});
            skLineSegment(sketch, "E407", {"start": v(-57.52, -3.25) * mm, "end": v(-57.74, -3.5) * mm});
            skLineSegment(sketch, "E408", {"start": v(-57.74, -3.5) * mm, "end": v(-57.96, -3.77) * mm});
            skLineSegment(sketch, "E409", {"start": v(-57.96, -3.77) * mm, "end": v(-58.11, -4.05) * mm});
            skLineSegment(sketch, "E410", {"start": v(-58.11, -4.05) * mm, "end": v(-58.26, -4.34) * mm});
            skLineSegment(sketch, "E411", {"start": v(-58.26, -4.34) * mm, "end": v(-58.36, -4.64) * mm});
            skLineSegment(sketch, "E412", {"start": v(-58.36, -4.64) * mm, "end": v(-58.46, -4.96) * mm});
            skLineSegment(sketch, "E413", {"start": v(-58.46, -4.96) * mm, "end": v(-58.48, -5.29) * mm});
            skLineSegment(sketch, "E414", {"start": v(-58.48, -5.29) * mm, "end": v(-58.5, -5.63) * mm});
            skLineSegment(sketch, "E415", {"start": v(-58.5, -5.63) * mm, "end": v(-58.5, -7.6) * mm});
            skLineSegment(sketch, "E416", {"start": v(-58.5, -7.6) * mm, "end": v(-58.48, -7.94) * mm});
            skLineSegment(sketch, "E417", {"start": v(-58.48, -7.94) * mm, "end": v(-58.46, -8.26) * mm});
            skLineSegment(sketch, "E418", {"start": v(-58.46, -8.26) * mm, "end": v(-58.36, -8.58) * mm});
            skLineSegment(sketch, "E419", {"start": v(-58.36, -8.58) * mm, "end": v(-58.26, -8.88) * mm});
            skLineSegment(sketch, "E420", {"start": v(-58.26, -8.88) * mm, "end": v(-58.11, -9.18) * mm});
            skLineSegment(sketch, "E421", {"start": v(-58.11, -9.18) * mm, "end": v(-57.96, -9.45) * mm});
            skLineSegment(sketch, "E422", {"start": v(-57.96, -9.45) * mm, "end": v(-57.74, -9.73) * mm});
            skLineSegment(sketch, "E423", {"start": v(-57.74, -9.73) * mm, "end": v(-57.52, -10) * mm});
            skLineSegment(sketch, "E424", {"start": v(-57.52, -10) * mm, "end": v(-57.27, -10.22) * mm});
            skLineSegment(sketch, "E425", {"start": v(-57.27, -10.22) * mm, "end": v(-57, -10.42) * mm});
            skLineSegment(sketch, "E426", {"start": v(-57, -10.42) * mm, "end": v(-56.72, -10.6) * mm});
            skLineSegment(sketch, "E427", {"start": v(-56.72, -10.6) * mm, "end": v(-56.43, -10.74) * mm});
            skLineSegment(sketch, "E428", {"start": v(-56.43, -10.74) * mm, "end": v(-56.13, -10.84) * mm});
            skLineSegment(sketch, "E429", {"start": v(-56.13, -10.84) * mm, "end": v(-55.8, -10.92) * mm});
            skLineSegment(sketch, "E430", {"start": v(-55.8, -10.92) * mm, "end": v(-55.46, -10.97) * mm});
            skLineSegment(sketch, "E431", {"start": v(-55.46, -10.97) * mm, "end": v(-55.11, -11) * mm});
            skLineSegment(sketch, "E432", {"start": v(-55.11, -11) * mm, "end": v(-51.74, -11) * mm});
            skLineSegment(sketch, "E433", {"start": v(-51.74, -11) * mm, "end": v(-51.74, 2.55) * mm});
            skLineSegment(sketch, "E434", {"start": v(-51.74, 2.55) * mm, "end": v(-51.76, 2.88) * mm});
            skLineSegment(sketch, "E435", {"start": v(-51.76, 2.88) * mm, "end": v(-51.81, 3.22) * mm});
            skLineSegment(sketch, "E436", {"start": v(-51.81, 3.22) * mm, "end": v(-51.89, 3.55) * mm});
            skLineSegment(sketch, "E437", {"start": v(-51.89, 3.55) * mm, "end": v(-52, 3.84) * mm});
            skLineSegment(sketch, "E438", {"start": v(-52, 3.84) * mm, "end": v(-52.13, 4.14) * mm});
            skLineSegment(sketch, "E439", {"start": v(-52.13, 4.14) * mm, "end": v(-52.3, 4.41) * mm});
            skLineSegment(sketch, "E440", {"start": v(-52.3, 4.41) * mm, "end": v(-52.5, 4.69) * mm});
            skLineSegment(sketch, "E441", {"start": v(-52.5, 4.69) * mm, "end": v(-52.73, 4.93) * mm});
            skLineSegment(sketch, "E442", {"start": v(-52.73, 4.93) * mm, "end": v(-53, 5.16) * mm});
            skLineSegment(sketch, "E443", {"start": v(-53, 5.16) * mm, "end": v(-53.25, 5.38) * mm});
            skLineSegment(sketch, "E444", {"start": v(-53.25, 5.38) * mm, "end": v(-53.55, 5.53) * mm});
            skLineSegment(sketch, "E445", {"start": v(-53.55, 5.53) * mm, "end": v(-53.82, 5.68) * mm});
            skLineSegment(sketch, "E446", {"start": v(-53.82, 5.68) * mm, "end": v(-54.14, 5.78) * mm});
            skLineSegment(sketch, "E447", {"start": v(-54.14, 5.78) * mm, "end": v(-54.47, 5.88) * mm});
            skLineSegment(sketch, "E448", {"start": v(-54.47, 5.88) * mm, "end": v(-54.79, 5.9) * mm});
            skLineSegment(sketch, "E449", {"start": v(-54.79, 5.9) * mm, "end": v(-55.14, 5.93) * mm});
            skLineSegment(sketch, "E450", {"start": v(-55.14, 5.93) * mm, "end": v(-55.48, 5.9) * mm});
            skLineSegment(sketch, "E451", {"start": v(-55.48, 5.9) * mm, "end": v(-55.83, 5.85) * mm});
            skLineSegment(sketch, "E452", {"start": v(-55.83, 5.85) * mm, "end": v(-56.15, 5.78) * mm});
            skLineSegment(sketch, "E453", {"start": v(-56.15, 5.78) * mm, "end": v(-56.45, 5.68) * mm});
            skLineSegment(sketch, "E454", {"start": v(-56.45, 5.68) * mm, "end": v(-56.75, 5.53) * mm});
            skLineSegment(sketch, "E455", {"start": v(-56.75, 5.53) * mm, "end": v(-57.05, 5.36) * mm});
            skLineSegment(sketch, "E456", {"start": v(-57.05, 5.36) * mm, "end": v(-57.32, 5.16) * mm});
            skLineSegment(sketch, "E457", {"start": v(-57.32, 5.16) * mm, "end": v(-57.6, 4.9) * mm});
            skLineSegment(sketch, "E458", {"start": v(-57.6, 4.9) * mm, "end": v(-57.71, 4.79) * mm});
            skLineSegment(sketch, "E459", {"start": v(-57.71, 4.79) * mm, "end": v(-57.86, 4.66) * mm});
            skLineSegment(sketch, "E460", {"start": v(-57.86, 4.66) * mm, "end": v(-58.04, 4.56) * mm});
            skLineSegment(sketch, "E461", {"start": v(-58.04, 4.56) * mm, "end": v(-58.19, 4.49) * mm});
            skLineSegment(sketch, "E462", {"start": v(-58.19, 4.49) * mm, "end": v(-58.36, 4.41) * mm});
            skLineSegment(sketch, "E463", {"start": v(-58.36, 4.41) * mm, "end": v(-58.56, 4.36) * mm});
            skLineSegment(sketch, "E464", {"start": v(-58.56, 4.36) * mm, "end": v(-58.73, 4.34) * mm});
            skLineSegment(sketch, "E465", {"start": v(-58.73, 4.34) * mm, "end": v(-58.96, 4.34) * mm});
            skLineSegment(sketch, "E466", {"start": v(-58.96, 4.34) * mm, "end": v(-59.13, 4.34) * mm});
            skLineSegment(sketch, "E467", {"start": v(-59.13, 4.34) * mm, "end": v(-59.33, 4.36) * mm});
            skLineSegment(sketch, "E468", {"start": v(-59.33, 4.36) * mm, "end": v(-59.5, 4.41) * mm});
            skLineSegment(sketch, "E469", {"start": v(-59.5, 4.41) * mm, "end": v(-59.67, 4.46) * mm});
            skLineSegment(sketch, "E470", {"start": v(-59.67, 4.46) * mm, "end": v(-59.85, 4.56) * mm});
            skLineSegment(sketch, "E471", {"start": v(-59.85, 4.56) * mm, "end": v(-60.02, 4.66) * mm});
            skLineSegment(sketch, "E472", {"start": v(-60.02, 4.66) * mm, "end": v(-60.17, 4.76) * mm});
            skLineSegment(sketch, "E473", {"start": v(-60.17, 4.76) * mm, "end": v(-60.32, 4.9) * mm});
            skLineSegment(sketch, "E474", {"start": v(-60.32, 4.9) * mm, "end": v(-60.44, 5.03) * mm});
            skLineSegment(sketch, "E475", {"start": v(-60.44, 5.03) * mm, "end": v(-60.57, 5.2) * mm});
            skLineSegment(sketch, "E476", {"start": v(-60.57, 5.2) * mm, "end": v(-60.67, 5.36) * mm});
            skLineSegment(sketch, "E477", {"start": v(-60.67, 5.36) * mm, "end": v(-60.74, 5.53) * mm});
            skLineSegment(sketch, "E478", {"start": v(-60.74, 5.53) * mm, "end": v(-60.8, 5.7) * mm});
            skLineSegment(sketch, "E479", {"start": v(-60.8, 5.7) * mm, "end": v(-60.84, 5.88) * mm});
            skLineSegment(sketch, "E480", {"start": v(-60.84, 5.88) * mm, "end": v(-60.87, 6.08) * mm});
            skLineSegment(sketch, "E481", {"start": v(-60.87, 6.08) * mm, "end": v(-60.89, 6.27) * mm});
            skLineSegment(sketch, "E482", {"start": v(-60.89, 6.27) * mm, "end": v(-60.87, 6.45) * mm});
            skLineSegment(sketch, "E483", {"start": v(-60.87, 6.45) * mm, "end": v(-60.84, 6.65) * mm});
            skLineSegment(sketch, "E484", {"start": v(-60.84, 6.65) * mm, "end": v(-60.8, 6.82) * mm});
            skLineSegment(sketch, "E485", {"start": v(-60.8, 6.82) * mm, "end": v(-60.74, 7) * mm});
            skLineSegment(sketch, "E486", {"start": v(-60.74, 7) * mm, "end": v(-60.67, 7.17) * mm});
            skLineSegment(sketch, "E487", {"start": v(-60.67, 7.17) * mm, "end": v(-60.57, 7.32) * mm});
            skLineSegment(sketch, "E488", {"start": v(-60.57, 7.32) * mm, "end": v(-60.44, 7.46) * mm});
            skLineSegment(sketch, "E489", {"start": v(-60.44, 7.46) * mm, "end": v(-60.32, 7.61) * mm});
            skLineSegment(sketch, "E490", {"start": v(-60.32, 7.61) * mm, "end": v(-59.77, 8.13) * mm});
            skLineSegment(sketch, "E491", {"start": v(-59.77, 8.13) * mm, "end": v(-59.18, 8.58) * mm});
            skLineSegment(sketch, "E492", {"start": v(-59.18, 8.58) * mm, "end": v(-58.58, 8.95) * mm});
            skLineSegment(sketch, "E493", {"start": v(-58.58, 8.95) * mm, "end": v(-57.94, 9.27) * mm});
            skLineSegment(sketch, "E494", {"start": v(-57.94, 9.27) * mm, "end": v(-57.27, 9.52) * mm});
            skLineSegment(sketch, "E495", {"start": v(-57.27, 9.52) * mm, "end": v(-56.6, 9.67) * mm});
            skLineSegment(sketch, "E496", {"start": v(-56.6, 9.67) * mm, "end": v(-55.88, 9.8) * mm});
            skLineSegment(sketch, "E497", {"start": v(-55.88, 9.8) * mm, "end": v(-55.14, 9.82) * mm});
            skLineSegment(sketch, "E498", {"start": v(-55.14, 9.82) * mm, "end": v(-54.42, 9.8) * mm});
            skLineSegment(sketch, "E499", {"start": v(-54.42, 9.8) * mm, "end": v(-53.7, 9.7) * mm});
            skLineSegment(sketch, "E500", {"start": v(-53.7, 9.7) * mm, "end": v(-53.03, 9.52) * mm});
            skLineSegment(sketch, "E501", {"start": v(-53.03, 9.52) * mm, "end": v(-52.36, 9.3) * mm});
            skLineSegment(sketch, "E502", {"start": v(-52.36, 9.3) * mm, "end": v(-51.74, 8.98) * mm});
            skLineSegment(sketch, "E503", {"start": v(-51.74, 8.98) * mm, "end": v(-51.14, 8.63) * mm});
            skLineSegment(sketch, "E504", {"start": v(-51.14, 8.63) * mm, "end": v(-50.57, 8.18) * mm});
            skLineSegment(sketch, "E505", {"start": v(-50.57, 8.18) * mm, "end": v(-50.03, 7.69) * mm});
            skLineSegment(sketch, "E506", {"start": v(-50.03, 7.69) * mm, "end": v(-49.53, 7.14) * mm});
            skLineSegment(sketch, "E507", {"start": v(-49.53, 7.14) * mm, "end": v(-49.08, 6.57) * mm});
            skLineSegment(sketch, "E508", {"start": v(-49.08, 6.57) * mm, "end": v(-48.71, 5.98) * mm});
            skLineSegment(sketch, "E509", {"start": v(-48.71, 5.98) * mm, "end": v(-48.41, 5.33) * mm});
            skLineSegment(sketch, "E510", {"start": v(-48.41, 5.33) * mm, "end": v(-48.19, 4.69) * mm});
            skLineSegment(sketch, "E511", {"start": v(-48.19, 4.69) * mm, "end": v(-48.02, 4) * mm});
            skLineSegment(sketch, "E512", {"start": v(-48.02, 4) * mm, "end": v(-47.92, 3.27) * mm});
            skLineSegment(sketch, "E513", {"start": v(-47.92, 3.27) * mm, "end": v(-47.87, 2.55) * mm});
            skLineSegment(sketch, "E514", {"start": v(-47.87, 2.55) * mm, "end": v(-47.87, -12.93) * mm});
            skLineSegment(sketch, "E515", {"start": v(-47.87, -12.93) * mm, "end": v(-47.87, -13.1) * mm});
            skLineSegment(sketch, "E516", {"start": v(-47.87, -13.1) * mm, "end": v(-47.9, -13.3) * mm});
            skLineSegment(sketch, "E517", {"start": v(-47.9, -13.3) * mm, "end": v(-47.94, -13.47) * mm});
            skLineSegment(sketch, "E518", {"start": v(-47.94, -13.47) * mm, "end": v(-48.02, -13.64) * mm});
            skLineSegment(sketch, "E519", {"start": v(-48.02, -13.64) * mm, "end": v(-48.1, -13.82) * mm});
            skLineSegment(sketch, "E520", {"start": v(-48.1, -13.82) * mm, "end": v(-48.19, -14) * mm});
            skLineSegment(sketch, "E521", {"start": v(-48.19, -14) * mm, "end": v(-48.31, -14.14) * mm});
            skLineSegment(sketch, "E522", {"start": v(-48.31, -14.14) * mm, "end": v(-48.44, -14.29) * mm});
            skLineSegment(sketch, "E523", {"start": v(-48.44, -14.29) * mm, "end": v(-48.59, -14.41) * mm});
            skLineSegment(sketch, "E524", {"start": v(-48.59, -14.41) * mm, "end": v(-48.74, -14.54) * mm});
            skLineSegment(sketch, "E525", {"start": v(-48.74, -14.54) * mm, "end": v(-48.88, -14.64) * mm});
            skLineSegment(sketch, "E526", {"start": v(-48.88, -14.64) * mm, "end": v(-49.06, -14.71) * mm});
            skLineSegment(sketch, "E527", {"start": v(-49.06, -14.71) * mm, "end": v(-49.23, -14.76) * mm});
            skLineSegment(sketch, "E528", {"start": v(-49.23, -14.76) * mm, "end": v(-49.4, -14.81) * mm});
            skLineSegment(sketch, "E529", {"start": v(-49.4, -14.81) * mm, "end": v(-49.6, -14.84) * mm});
            skLineSegment(sketch, "E530", {"start": v(-49.6, -14.84) * mm, "end": v(-49.8, -14.86) * mm});
            skLineSegment(sketch, "E531", {"start": v(-49.8, -14.86) * mm, "end": v(-55.11, -14.86) * mm});
            skLineSegment(sketch, "E532", {"start": v(-55.11, -14.86) * mm, "end": v(-55.85, -14.81) * mm});
            skLineSegment(sketch, "E533", {"start": v(-55.85, -14.81) * mm, "end": v(-56.57, -14.71) * mm});
            skLineSegment(sketch, "E534", {"start": v(-56.57, -14.71) * mm, "end": v(-57.24, -14.54) * mm});
            skLineSegment(sketch, "E535", {"start": v(-57.24, -14.54) * mm, "end": v(-57.91, -14.31) * mm});
            skLineSegment(sketch, "E536", {"start": v(-57.91, -14.31) * mm, "end": v(-58.53, -14.02) * mm});
            skLineSegment(sketch, "E537", {"start": v(-58.53, -14.02) * mm, "end": v(-59.13, -13.64) * mm});
            skLineSegment(sketch, "E538", {"start": v(-59.13, -13.64) * mm, "end": v(-59.7, -13.22) * mm});
            skLineSegment(sketch, "E539", {"start": v(-59.7, -13.22) * mm, "end": v(-60.25, -12.73) * mm});
            skLineSegment(sketch, "E540", {"start": v(-60.25, -12.73) * mm, "end": v(-60.74, -12.18) * mm});
            skLineSegment(sketch, "E541", {"start": v(-60.74, -12.18) * mm, "end": v(-61.19, -11.61) * mm});
            skLineSegment(sketch, "E542", {"start": v(-61.19, -11.61) * mm, "end": v(-61.53, -11) * mm});
            skLineSegment(sketch, "E543", {"start": v(-61.53, -11) * mm, "end": v(-61.86, -10.37) * mm});
            skLineSegment(sketch, "E544", {"start": v(-61.86, -10.37) * mm, "end": v(-62.08, -9.73) * mm});
            skLineSegment(sketch, "E545", {"start": v(-62.08, -9.73) * mm, "end": v(-62.25, -9.03) * mm});
            skLineSegment(sketch, "E546", {"start": v(-62.25, -9.03) * mm, "end": v(-62.35, -8.34) * mm});
            skLineSegment(sketch, "E547", {"start": v(-62.35, -8.34) * mm, "end": v(-62.38, -7.6) * mm});
            skLineSegment(sketch, "E548", {"start": v(-62.38, -7.6) * mm, "end": v(-62.38, -5.63) * mm});
            skLineSegment(sketch, "E549", {"start": v(-62.38, -5.63) * mm, "end": v(-62.35, -4.89) * mm});
            skLineSegment(sketch, "E550", {"start": v(-42.5, -13.3) * mm, "end": v(-42.53, -13.1) * mm});
            skLineSegment(sketch, "E551", {"start": v(-42.53, -13.1) * mm, "end": v(-42.53, -12.93) * mm});
            skLineSegment(sketch, "E552", {"start": v(-42.53, -12.93) * mm, "end": v(-42.53, 7.41) * mm});
            skLineSegment(sketch, "E553", {"start": v(-42.53, 7.41) * mm, "end": v(-42.53, 7.59) * mm});
            skLineSegment(sketch, "E554", {"start": v(-42.53, 7.59) * mm, "end": v(-42.5, 7.79) * mm});
            skLineSegment(sketch, "E555", {"start": v(-42.5, 7.79) * mm, "end": v(-42.46, 7.96) * mm});
            skLineSegment(sketch, "E556", {"start": v(-42.46, 7.96) * mm, "end": v(-42.39, 8.13) * mm});
            skLineSegment(sketch, "E557", {"start": v(-42.39, 8.13) * mm, "end": v(-42.31, 8.3) * mm});
            skLineSegment(sketch, "E558", {"start": v(-42.31, 8.3) * mm, "end": v(-42.21, 8.48) * mm});
            skLineSegment(sketch, "E559", {"start": v(-42.21, 8.48) * mm, "end": v(-42.09, 8.63) * mm});
            skLineSegment(sketch, "E560", {"start": v(-42.09, 8.63) * mm, "end": v(-41.96, 8.78) * mm});
            skLineSegment(sketch, "E561", {"start": v(-41.96, 8.78) * mm, "end": v(-41.82, 8.9) * mm});
            skLineSegment(sketch, "E562", {"start": v(-41.82, 8.9) * mm, "end": v(-41.67, 9.03) * mm});
            skLineSegment(sketch, "E563", {"start": v(-41.67, 9.03) * mm, "end": v(-41.52, 9.13) * mm});
            skLineSegment(sketch, "E564", {"start": v(-41.52, 9.13) * mm, "end": v(-41.34, 9.2) * mm});
            skLineSegment(sketch, "E565", {"start": v(-41.34, 9.2) * mm, "end": v(-41.17, 9.25) * mm});
            skLineSegment(sketch, "E566", {"start": v(-41.17, 9.25) * mm, "end": v(-41, 9.3) * mm});
            skLineSegment(sketch, "E567", {"start": v(-41, 9.3) * mm, "end": v(-40.8, 9.32) * mm});
            skLineSegment(sketch, "E568", {"start": v(-40.8, 9.32) * mm, "end": v(-40.6, 9.35) * mm});
            skLineSegment(sketch, "E569", {"start": v(-40.6, 9.35) * mm, "end": v(-35.3, 9.35) * mm});
            skLineSegment(sketch, "E570", {"start": v(-35.3, 9.35) * mm, "end": v(-34.55, 9.3) * mm});
            skLineSegment(sketch, "E571", {"start": v(-34.55, 9.3) * mm, "end": v(-33.83, 9.2) * mm});
            skLineSegment(sketch, "E572", {"start": v(-33.83, 9.2) * mm, "end": v(-33.16, 9.03) * mm});
            skLineSegment(sketch, "E573", {"start": v(-33.16, 9.03) * mm, "end": v(-32.49, 8.8) * mm});
            skLineSegment(sketch, "E574", {"start": v(-32.49, 8.8) * mm, "end": v(-31.87, 8.5) * mm});
            skLineSegment(sketch, "E575", {"start": v(-31.87, 8.5) * mm, "end": v(-31.27, 8.13) * mm});
            skLineSegment(sketch, "E576", {"start": v(-31.27, 8.13) * mm, "end": v(-30.7, 7.71) * mm});
            skLineSegment(sketch, "E577", {"start": v(-30.7, 7.71) * mm, "end": v(-30.16, 7.22) * mm});
            skLineSegment(sketch, "E578", {"start": v(-30.16, 7.22) * mm, "end": v(-29.66, 6.67) * mm});
            skLineSegment(sketch, "E579", {"start": v(-29.66, 6.67) * mm, "end": v(-29.21, 6.1) * mm});
            skLineSegment(sketch, "E580", {"start": v(-29.21, 6.1) * mm, "end": v(-28.87, 5.48) * mm});
            skLineSegment(sketch, "E581", {"start": v(-28.87, 5.48) * mm, "end": v(-28.54, 4.86) * mm});
            skLineSegment(sketch, "E582", {"start": v(-28.54, 4.86) * mm, "end": v(-28.32, 4.21) * mm});
            skLineSegment(sketch, "E583", {"start": v(-28.32, 4.21) * mm, "end": v(-28.15, 3.52) * mm});
            skLineSegment(sketch, "E584", {"start": v(-28.15, 3.52) * mm, "end": v(-28.05, 2.83) * mm});
            skLineSegment(sketch, "E585", {"start": v(-28.05, 2.83) * mm, "end": v(-28.02, 2.08) * mm});
            skLineSegment(sketch, "E586", {"start": v(-28.02, 2.08) * mm, "end": v(-28.02, -12.93) * mm});
            skLineSegment(sketch, "E587", {"start": v(-28.02, -12.93) * mm, "end": v(-28.02, -13.1) * mm});
            skLineSegment(sketch, "E588", {"start": v(-28.02, -13.1) * mm, "end": v(-28.05, -13.3) * mm});
            skLineSegment(sketch, "E589", {"start": v(-28.05, -13.3) * mm, "end": v(-28.1, -13.47) * mm});
            skLineSegment(sketch, "E590", {"start": v(-28.1, -13.47) * mm, "end": v(-28.17, -13.64) * mm});
            skLineSegment(sketch, "E591", {"start": v(-28.17, -13.64) * mm, "end": v(-28.25, -13.82) * mm});
            skLineSegment(sketch, "E592", {"start": v(-28.25, -13.82) * mm, "end": v(-28.35, -14) * mm});
            skLineSegment(sketch, "E593", {"start": v(-28.35, -14) * mm, "end": v(-28.47, -14.14) * mm});
            skLineSegment(sketch, "E594", {"start": v(-28.47, -14.14) * mm, "end": v(-28.6, -14.29) * mm});
            skLineSegment(sketch, "E595", {"start": v(-28.6, -14.29) * mm, "end": v(-28.74, -14.41) * mm});
            skLineSegment(sketch, "E596", {"start": v(-28.74, -14.41) * mm, "end": v(-28.9, -14.54) * mm});
            skLineSegment(sketch, "E597", {"start": v(-28.9, -14.54) * mm, "end": v(-29.04, -14.64) * mm});
            skLineSegment(sketch, "E598", {"start": v(-29.04, -14.64) * mm, "end": v(-29.21, -14.71) * mm});
            skLineSegment(sketch, "E599", {"start": v(-29.21, -14.71) * mm, "end": v(-29.39, -14.76) * mm});
            skLineSegment(sketch, "E600", {"start": v(-29.39, -14.76) * mm, "end": v(-29.56, -14.81) * mm});
            skLineSegment(sketch, "E601", {"start": v(-29.56, -14.81) * mm, "end": v(-29.76, -14.84) * mm});
            skLineSegment(sketch, "E602", {"start": v(-29.76, -14.84) * mm, "end": v(-29.96, -14.86) * mm});
            skLineSegment(sketch, "E603", {"start": v(-29.96, -14.86) * mm, "end": v(-30.16, -14.84) * mm});
            skLineSegment(sketch, "E604", {"start": v(-30.16, -14.84) * mm, "end": v(-30.36, -14.81) * mm});
            skLineSegment(sketch, "E605", {"start": v(-30.36, -14.81) * mm, "end": v(-30.53, -14.76) * mm});
            skLineSegment(sketch, "E606", {"start": v(-30.53, -14.76) * mm, "end": v(-30.7, -14.71) * mm});
            skLineSegment(sketch, "E607", {"start": v(-30.7, -14.71) * mm, "end": v(-30.88, -14.64) * mm});
            skLineSegment(sketch, "E608", {"start": v(-30.88, -14.64) * mm, "end": v(-31.03, -14.54) * mm});
            skLineSegment(sketch, "E609", {"start": v(-31.03, -14.54) * mm, "end": v(-31.17, -14.41) * mm});
            skLineSegment(sketch, "E610", {"start": v(-31.17, -14.41) * mm, "end": v(-31.32, -14.29) * mm});
            skLineSegment(sketch, "E611", {"start": v(-31.32, -14.29) * mm, "end": v(-31.45, -14.14) * mm});
            skLineSegment(sketch, "E612", {"start": v(-31.45, -14.14) * mm, "end": v(-31.57, -14) * mm});
            skLineSegment(sketch, "E613", {"start": v(-31.57, -14) * mm, "end": v(-31.67, -13.82) * mm});
            skLineSegment(sketch, "E614", {"start": v(-31.67, -13.82) * mm, "end": v(-31.74, -13.64) * mm});
            skLineSegment(sketch, "E615", {"start": v(-31.74, -13.64) * mm, "end": v(-31.82, -13.47) * mm});
            skLineSegment(sketch, "E616", {"start": v(-31.82, -13.47) * mm, "end": v(-31.87, -13.3) * mm});
            skLineSegment(sketch, "E617", {"start": v(-31.87, -13.3) * mm, "end": v(-31.9, -13.1) * mm});
            skLineSegment(sketch, "E618", {"start": v(-31.9, -13.1) * mm, "end": v(-31.9, -12.93) * mm});
            skLineSegment(sketch, "E619", {"start": v(-31.9, -12.93) * mm, "end": v(-31.9, 2.08) * mm});
            skLineSegment(sketch, "E620", {"start": v(-31.9, 2.08) * mm, "end": v(-31.92, 2.43) * mm});
            skLineSegment(sketch, "E621", {"start": v(-31.92, 2.43) * mm, "end": v(-31.94, 2.75) * mm});
            skLineSegment(sketch, "E622", {"start": v(-31.94, 2.75) * mm, "end": v(-32.04, 3.07) * mm});
            skLineSegment(sketch, "E623", {"start": v(-32.04, 3.07) * mm, "end": v(-32.14, 3.37) * mm});
            skLineSegment(sketch, "E624", {"start": v(-32.14, 3.37) * mm, "end": v(-32.3, 3.67) * mm});
            skLineSegment(sketch, "E625", {"start": v(-32.3, 3.67) * mm, "end": v(-32.44, 3.94) * mm});
            skLineSegment(sketch, "E626", {"start": v(-32.44, 3.94) * mm, "end": v(-32.66, 4.21) * mm});
            skLineSegment(sketch, "E627", {"start": v(-32.66, 4.21) * mm, "end": v(-32.89, 4.49) * mm});
            skLineSegment(sketch, "E628", {"start": v(-32.89, 4.49) * mm, "end": v(-33.13, 4.71) * mm});
            skLineSegment(sketch, "E629", {"start": v(-33.13, 4.71) * mm, "end": v(-33.4, 4.9) * mm});
            skLineSegment(sketch, "E630", {"start": v(-33.4, 4.9) * mm, "end": v(-33.68, 5.08) * mm});
            skLineSegment(sketch, "E631", {"start": v(-33.68, 5.08) * mm, "end": v(-33.98, 5.23) * mm});
            skLineSegment(sketch, "E632", {"start": v(-33.98, 5.23) * mm, "end": v(-34.27, 5.33) * mm});
            skLineSegment(sketch, "E633", {"start": v(-34.27, 5.33) * mm, "end": v(-34.6, 5.4) * mm});
            skLineSegment(sketch, "E634", {"start": v(-34.6, 5.4) * mm, "end": v(-34.94, 5.46) * mm});
            skLineSegment(sketch, "E635", {"start": v(-34.94, 5.46) * mm, "end": v(-35.3, 5.48) * mm});
            skLineSegment(sketch, "E636", {"start": v(-35.3, 5.48) * mm, "end": v(-38.66, 5.48) * mm});
            skLineSegment(sketch, "E637", {"start": v(-38.66, 5.48) * mm, "end": v(-38.66, -12.93) * mm});
            skLineSegment(sketch, "E638", {"start": v(-38.66, -12.93) * mm, "end": v(-38.66, -13.1) * mm});
            skLineSegment(sketch, "E639", {"start": v(-38.66, -13.1) * mm, "end": v(-38.69, -13.3) * mm});
            skLineSegment(sketch, "E640", {"start": v(-38.69, -13.3) * mm, "end": v(-38.74, -13.47) * mm});
            skLineSegment(sketch, "E641", {"start": v(-38.74, -13.47) * mm, "end": v(-38.81, -13.64) * mm});
            skLineSegment(sketch, "E642", {"start": v(-38.81, -13.64) * mm, "end": v(-38.89, -13.82) * mm});
            skLineSegment(sketch, "E643", {"start": v(-38.89, -13.82) * mm, "end": v(-38.99, -14) * mm});
            skLineSegment(sketch, "E644", {"start": v(-38.99, -14) * mm, "end": v(-39.11, -14.14) * mm});
            skLineSegment(sketch, "E645", {"start": v(-39.11, -14.14) * mm, "end": v(-39.24, -14.29) * mm});
            skLineSegment(sketch, "E646", {"start": v(-39.24, -14.29) * mm, "end": v(-39.38, -14.41) * mm});
            skLineSegment(sketch, "E647", {"start": v(-39.38, -14.41) * mm, "end": v(-39.53, -14.54) * mm});
            skLineSegment(sketch, "E648", {"start": v(-39.53, -14.54) * mm, "end": v(-39.68, -14.64) * mm});
            skLineSegment(sketch, "E649", {"start": v(-39.68, -14.64) * mm, "end": v(-39.86, -14.71) * mm});
            skLineSegment(sketch, "E650", {"start": v(-39.86, -14.71) * mm, "end": v(-40.03, -14.76) * mm});
            skLineSegment(sketch, "E651", {"start": v(-40.03, -14.76) * mm, "end": v(-40.2, -14.81) * mm});
            skLineSegment(sketch, "E652", {"start": v(-40.2, -14.81) * mm, "end": v(-40.4, -14.84) * mm});
            skLineSegment(sketch, "E653", {"start": v(-40.4, -14.84) * mm, "end": v(-40.6, -14.86) * mm});
            skLineSegment(sketch, "E654", {"start": v(-40.6, -14.86) * mm, "end": v(-40.8, -14.84) * mm});
            skLineSegment(sketch, "E655", {"start": v(-40.8, -14.84) * mm, "end": v(-41, -14.81) * mm});
            skLineSegment(sketch, "E656", {"start": v(-41, -14.81) * mm, "end": v(-41.17, -14.76) * mm});
            skLineSegment(sketch, "E657", {"start": v(-41.17, -14.76) * mm, "end": v(-41.34, -14.71) * mm});
            skLineSegment(sketch, "E658", {"start": v(-41.34, -14.71) * mm, "end": v(-41.52, -14.64) * mm});
            skLineSegment(sketch, "E659", {"start": v(-41.52, -14.64) * mm, "end": v(-41.67, -14.54) * mm});
            skLineSegment(sketch, "E660", {"start": v(-41.67, -14.54) * mm, "end": v(-41.82, -14.41) * mm});
            skLineSegment(sketch, "E661", {"start": v(-41.82, -14.41) * mm, "end": v(-41.96, -14.29) * mm});
            skLineSegment(sketch, "E662", {"start": v(-41.96, -14.29) * mm, "end": v(-42.09, -14.14) * mm});
            skLineSegment(sketch, "E663", {"start": v(-42.09, -14.14) * mm, "end": v(-42.21, -14) * mm});
            skLineSegment(sketch, "E664", {"start": v(-42.21, -14) * mm, "end": v(-42.31, -13.82) * mm});
            skLineSegment(sketch, "E665", {"start": v(-42.31, -13.82) * mm, "end": v(-42.39, -13.64) * mm});
            skLineSegment(sketch, "E666", {"start": v(-42.39, -13.64) * mm, "end": v(-42.46, -13.47) * mm});
            skLineSegment(sketch, "E667", {"start": v(-42.46, -13.47) * mm, "end": v(-42.5, -13.3) * mm});
            skLineSegment(sketch, "E668", {"start": v(-23.16, 7.02) * mm, "end": v(-23.19, 7.22) * mm});
            skLineSegment(sketch, "E669", {"start": v(-23.19, 7.22) * mm, "end": v(-23.19, 7.41) * mm});
            skLineSegment(sketch, "E670", {"start": v(-23.19, 7.41) * mm, "end": v(-23.19, 7.59) * mm});
            skLineSegment(sketch, "E671", {"start": v(-23.19, 7.59) * mm, "end": v(-23.16, 7.79) * mm});
            skLineSegment(sketch, "E672", {"start": v(-23.16, 7.79) * mm, "end": v(-23.11, 7.96) * mm});
            skLineSegment(sketch, "E673", {"start": v(-23.11, 7.96) * mm, "end": v(-23.06, 8.13) * mm});
            skLineSegment(sketch, "E674", {"start": v(-23.06, 8.13) * mm, "end": v(-22.96, 8.3) * mm});
            skLineSegment(sketch, "E675", {"start": v(-22.96, 8.3) * mm, "end": v(-22.86, 8.48) * mm});
            skLineSegment(sketch, "E676", {"start": v(-22.86, 8.48) * mm, "end": v(-22.77, 8.63) * mm});
            skLineSegment(sketch, "E677", {"start": v(-22.77, 8.63) * mm, "end": v(-22.62, 8.78) * mm});
            skLineSegment(sketch, "E678", {"start": v(-22.62, 8.78) * mm, "end": v(-22.52, 8.88) * mm});
            skLineSegment(sketch, "E679", {"start": v(-22.52, 8.88) * mm, "end": v(-22.42, 8.95) * mm});
            skLineSegment(sketch, "E680", {"start": v(-22.42, 8.95) * mm, "end": v(-22.32, 9.03) * mm});
            skLineSegment(sketch, "E681", {"start": v(-22.32, 9.03) * mm, "end": v(-22.2, 9.1) * mm});
            skLineSegment(sketch, "E682", {"start": v(-22.2, 9.1) * mm, "end": v(-22.1, 9.15) * mm});
            skLineSegment(sketch, "E683", {"start": v(-22.1, 9.15) * mm, "end": v(-21.97, 9.2) * mm});
            skLineSegment(sketch, "E684", {"start": v(-21.97, 9.2) * mm, "end": v(-21.85, 9.25) * mm});
            skLineSegment(sketch, "E685", {"start": v(-21.85, 9.25) * mm, "end": v(-21.72, 9.3) * mm});
            skLineSegment(sketch, "E686", {"start": v(-21.72, 9.3) * mm, "end": v(-21.72, 13.2) * mm});
            skLineSegment(sketch, "E687", {"start": v(-21.72, 13.2) * mm, "end": v(-21.72, 13.37) * mm});
            skLineSegment(sketch, "E688", {"start": v(-21.72, 13.37) * mm, "end": v(-21.7, 13.57) * mm});
            skLineSegment(sketch, "E689", {"start": v(-21.7, 13.57) * mm, "end": v(-21.65, 13.74) * mm});
            skLineSegment(sketch, "E690", {"start": v(-21.65, 13.74) * mm, "end": v(-21.57, 13.91) * mm});
            skLineSegment(sketch, "E691", {"start": v(-21.57, 13.91) * mm, "end": v(-21.5, 14.09) * mm});
            skLineSegment(sketch, "E692", {"start": v(-21.5, 14.09) * mm, "end": v(-21.4, 14.26) * mm});
            skLineSegment(sketch, "E693", {"start": v(-21.4, 14.26) * mm, "end": v(-21.28, 14.4) * mm});
            skLineSegment(sketch, "E694", {"start": v(-21.28, 14.4) * mm, "end": v(-21.15, 14.56) * mm});
            skLineSegment(sketch, "E695", {"start": v(-21.15, 14.56) * mm, "end": v(-21, 14.68) * mm});
            skLineSegment(sketch, "E696", {"start": v(-21, 14.68) * mm, "end": v(-20.83, 14.8) * mm});
            skLineSegment(sketch, "E697", {"start": v(-20.83, 14.8) * mm, "end": v(-20.68, 14.9) * mm});
            skLineSegment(sketch, "E698", {"start": v(-20.68, 14.9) * mm, "end": v(-20.5, 14.98) * mm});
            skLineSegment(sketch, "E699", {"start": v(-20.5, 14.98) * mm, "end": v(-20.33, 15.03) * mm});
            skLineSegment(sketch, "E700", {"start": v(-20.33, 15.03) * mm, "end": v(-20.16, 15.08) * mm});
            skLineSegment(sketch, "E701", {"start": v(-20.16, 15.08) * mm, "end": v(-19.99, 15.1) * mm});
            skLineSegment(sketch, "E702", {"start": v(-19.99, 15.1) * mm, "end": v(-19.79, 15.13) * mm});
            skLineSegment(sketch, "E703", {"start": v(-19.79, 15.13) * mm, "end": v(-19.6, 15.1) * mm});
            skLineSegment(sketch, "E704", {"start": v(-19.6, 15.1) * mm, "end": v(-19.4, 15.08) * mm});
            skLineSegment(sketch, "E705", {"start": v(-19.4, 15.08) * mm, "end": v(-19.22, 15.03) * mm});
            skLineSegment(sketch, "E706", {"start": v(-19.22, 15.03) * mm, "end": v(-19.04, 14.98) * mm});
            skLineSegment(sketch, "E707", {"start": v(-19.04, 14.98) * mm, "end": v(-18.87, 14.9) * mm});
            skLineSegment(sketch, "E708", {"start": v(-18.87, 14.9) * mm, "end": v(-18.72, 14.8) * mm});
            skLineSegment(sketch, "E709", {"start": v(-18.72, 14.8) * mm, "end": v(-18.57, 14.68) * mm});
            skLineSegment(sketch, "E710", {"start": v(-18.57, 14.68) * mm, "end": v(-18.42, 14.56) * mm});
            skLineSegment(sketch, "E711", {"start": v(-18.42, 14.56) * mm, "end": v(-18.3, 14.4) * mm});
            skLineSegment(sketch, "E712", {"start": v(-18.3, 14.4) * mm, "end": v(-18.18, 14.26) * mm});
            skLineSegment(sketch, "E713", {"start": v(-18.18, 14.26) * mm, "end": v(-18.08, 14.09) * mm});
            skLineSegment(sketch, "E714", {"start": v(-18.08, 14.09) * mm, "end": v(-18, 13.91) * mm});
            skLineSegment(sketch, "E715", {"start": v(-18, 13.91) * mm, "end": v(-17.93, 13.74) * mm});
            skLineSegment(sketch, "E716", {"start": v(-17.93, 13.74) * mm, "end": v(-17.88, 13.57) * mm});
            skLineSegment(sketch, "E717", {"start": v(-17.88, 13.57) * mm, "end": v(-17.85, 13.37) * mm});
            skLineSegment(sketch, "E718", {"start": v(-17.85, 13.37) * mm, "end": v(-17.85, 13.2) * mm});
            skLineSegment(sketch, "E719", {"start": v(-17.85, 13.2) * mm, "end": v(-17.85, 9.35) * mm});
            skLineSegment(sketch, "E720", {"start": v(-17.85, 9.35) * mm, "end": v(-15.42, 9.35) * mm});
            skLineSegment(sketch, "E721", {"start": v(-15.42, 9.35) * mm, "end": v(-15.25, 9.32) * mm});
            skLineSegment(sketch, "E722", {"start": v(-15.25, 9.32) * mm, "end": v(-15.05, 9.3) * mm});
            skLineSegment(sketch, "E723", {"start": v(-15.05, 9.3) * mm, "end": v(-14.88, 9.25) * mm});
            skLineSegment(sketch, "E724", {"start": v(-14.88, 9.25) * mm, "end": v(-14.7, 9.2) * mm});
            skLineSegment(sketch, "E725", {"start": v(-14.7, 9.2) * mm, "end": v(-14.53, 9.13) * mm});
            skLineSegment(sketch, "E726", {"start": v(-14.53, 9.13) * mm, "end": v(-14.36, 9.03) * mm});
            skLineSegment(sketch, "E727", {"start": v(-14.36, 9.03) * mm, "end": v(-14.2, 8.9) * mm});
            skLineSegment(sketch, "E728", {"start": v(-14.2, 8.9) * mm, "end": v(-14.06, 8.78) * mm});
            skLineSegment(sketch, "E729", {"start": v(-14.06, 8.78) * mm, "end": v(-13.93, 8.63) * mm});
            skLineSegment(sketch, "E730", {"start": v(-13.93, 8.63) * mm, "end": v(-13.81, 8.48) * mm});
            skLineSegment(sketch, "E731", {"start": v(-13.81, 8.48) * mm, "end": v(-13.71, 8.3) * mm});
            skLineSegment(sketch, "E732", {"start": v(-13.71, 8.3) * mm, "end": v(-13.64, 8.13) * mm});
            skLineSegment(sketch, "E733", {"start": v(-13.64, 8.13) * mm, "end": v(-13.59, 7.96) * mm});
            skLineSegment(sketch, "E734", {"start": v(-13.59, 7.96) * mm, "end": v(-13.54, 7.79) * mm});
            skLineSegment(sketch, "E735", {"start": v(-13.54, 7.79) * mm, "end": v(-13.51, 7.59) * mm});
            skLineSegment(sketch, "E736", {"start": v(-13.51, 7.59) * mm, "end": v(-13.49, 7.41) * mm});
            skLineSegment(sketch, "E737", {"start": v(-13.49, 7.41) * mm, "end": v(-13.51, 7.22) * mm});
            skLineSegment(sketch, "E738", {"start": v(-13.51, 7.22) * mm, "end": v(-13.54, 7.02) * mm});
            skLineSegment(sketch, "E739", {"start": v(-13.54, 7.02) * mm, "end": v(-13.59, 6.84) * mm});
            skLineSegment(sketch, "E740", {"start": v(-13.59, 6.84) * mm, "end": v(-13.64, 6.67) * mm});
            skLineSegment(sketch, "E741", {"start": v(-13.64, 6.67) * mm, "end": v(-13.71, 6.5) * mm});
            skLineSegment(sketch, "E742", {"start": v(-13.71, 6.5) * mm, "end": v(-13.81, 6.32) * mm});
            skLineSegment(sketch, "E743", {"start": v(-13.81, 6.32) * mm, "end": v(-13.93, 6.17) * mm});
            skLineSegment(sketch, "E744", {"start": v(-13.93, 6.17) * mm, "end": v(-14.06, 6.03) * mm});
            skLineSegment(sketch, "E745", {"start": v(-14.06, 6.03) * mm, "end": v(-14.2, 5.9) * mm});
            skLineSegment(sketch, "E746", {"start": v(-14.2, 5.9) * mm, "end": v(-14.36, 5.78) * mm});
            skLineSegment(sketch, "E747", {"start": v(-14.36, 5.78) * mm, "end": v(-14.53, 5.68) * mm});
            skLineSegment(sketch, "E748", {"start": v(-14.53, 5.68) * mm, "end": v(-14.7, 5.6) * mm});
            skLineSegment(sketch, "E749", {"start": v(-14.7, 5.6) * mm, "end": v(-14.88, 5.55) * mm});
            skLineSegment(sketch, "E750", {"start": v(-14.88, 5.55) * mm, "end": v(-15.05, 5.5) * mm});
            skLineSegment(sketch, "E751", {"start": v(-15.05, 5.5) * mm, "end": v(-15.25, 5.48) * mm});
            skLineSegment(sketch, "E752", {"start": v(-15.25, 5.48) * mm, "end": v(-15.42, 5.48) * mm});
            skLineSegment(sketch, "E753", {"start": v(-15.42, 5.48) * mm, "end": v(-17.85, 5.48) * mm});
            skLineSegment(sketch, "E754", {"start": v(-17.85, 5.48) * mm, "end": v(-17.85, -8.56) * mm});
            skLineSegment(sketch, "E755", {"start": v(-17.85, -8.56) * mm, "end": v(-17.85, -8.8) * mm});
            skLineSegment(sketch, "E756", {"start": v(-17.85, -8.8) * mm, "end": v(-17.8, -9.06) * mm});
            skLineSegment(sketch, "E757", {"start": v(-17.8, -9.06) * mm, "end": v(-17.75, -9.28) * mm});
            skLineSegment(sketch, "E758", {"start": v(-17.75, -9.28) * mm, "end": v(-17.68, -9.5) * mm});
            skLineSegment(sketch, "E759", {"start": v(-17.68, -9.5) * mm, "end": v(-17.58, -9.7) * mm});
            skLineSegment(sketch, "E760", {"start": v(-17.58, -9.7) * mm, "end": v(-17.46, -9.9) * mm});
            skLineSegment(sketch, "E761", {"start": v(-17.46, -9.9) * mm, "end": v(-17.3, -10.1) * mm});
            skLineSegment(sketch, "E762", {"start": v(-17.3, -10.1) * mm, "end": v(-17.16, -10.27) * mm});
            skLineSegment(sketch, "E763", {"start": v(-17.16, -10.27) * mm, "end": v(-16.96, -10.44) * mm});
            skLineSegment(sketch, "E764", {"start": v(-16.96, -10.44) * mm, "end": v(-16.79, -10.6) * mm});
            skLineSegment(sketch, "E765", {"start": v(-16.79, -10.6) * mm, "end": v(-16.59, -10.7) * mm});
            skLineSegment(sketch, "E766", {"start": v(-16.59, -10.7) * mm, "end": v(-16.37, -10.8) * mm});
            skLineSegment(sketch, "E767", {"start": v(-16.37, -10.8) * mm, "end": v(-16.14, -10.9) * mm});
            skLineSegment(sketch, "E768", {"start": v(-16.14, -10.9) * mm, "end": v(-15.92, -10.94) * mm});
            skLineSegment(sketch, "E769", {"start": v(-15.92, -10.94) * mm, "end": v(-15.7, -10.97) * mm});
            skLineSegment(sketch, "E770", {"start": v(-15.7, -10.97) * mm, "end": v(-15.42, -11) * mm});
            skLineSegment(sketch, "E771", {"start": v(-15.42, -11) * mm, "end": v(-15.22, -11) * mm});
            skLineSegment(sketch, "E772", {"start": v(-15.22, -11) * mm, "end": v(-15.05, -11.02) * mm});
            skLineSegment(sketch, "E773", {"start": v(-15.05, -11.02) * mm, "end": v(-14.85, -11.06) * mm});
            skLineSegment(sketch, "E774", {"start": v(-14.85, -11.06) * mm, "end": v(-14.68, -11.11) * mm});
            skLineSegment(sketch, "E775", {"start": v(-14.68, -11.11) * mm, "end": v(-14.5, -11.21) * mm});
            skLineSegment(sketch, "E776", {"start": v(-14.5, -11.21) * mm, "end": v(-14.36, -11.31) * mm});
            skLineSegment(sketch, "E777", {"start": v(-14.36, -11.31) * mm, "end": v(-14.18, -11.41) * mm});
            skLineSegment(sketch, "E778", {"start": v(-14.18, -11.41) * mm, "end": v(-14.03, -11.56) * mm});
            skLineSegment(sketch, "E779", {"start": v(-14.03, -11.56) * mm, "end": v(-13.9, -11.7) * mm});
            skLineSegment(sketch, "E780", {"start": v(-13.9, -11.7) * mm, "end": v(-13.79, -11.86) * mm});
            skLineSegment(sketch, "E781", {"start": v(-13.79, -11.86) * mm, "end": v(-13.69, -12.03) * mm});
            skLineSegment(sketch, "E782", {"start": v(-13.69, -12.03) * mm, "end": v(-13.61, -12.18) * mm});
            skLineSegment(sketch, "E783", {"start": v(-13.61, -12.18) * mm, "end": v(-13.56, -12.35) * mm});
            skLineSegment(sketch, "E784", {"start": v(-13.56, -12.35) * mm, "end": v(-13.51, -12.53) * mm});
            skLineSegment(sketch, "E785", {"start": v(-13.51, -12.53) * mm, "end": v(-13.49, -12.73) * mm});
            skLineSegment(sketch, "E786", {"start": v(-13.49, -12.73) * mm, "end": v(-13.49, -12.93) * mm});
            skLineSegment(sketch, "E787", {"start": v(-13.49, -12.93) * mm, "end": v(-13.49, -13.1) * mm});
            skLineSegment(sketch, "E788", {"start": v(-13.49, -13.1) * mm, "end": v(-13.51, -13.3) * mm});
            skLineSegment(sketch, "E789", {"start": v(-13.51, -13.3) * mm, "end": v(-13.56, -13.47) * mm});
            skLineSegment(sketch, "E790", {"start": v(-13.56, -13.47) * mm, "end": v(-13.61, -13.64) * mm});
            skLineSegment(sketch, "E791", {"start": v(-13.61, -13.64) * mm, "end": v(-13.69, -13.82) * mm});
            skLineSegment(sketch, "E792", {"start": v(-13.69, -13.82) * mm, "end": v(-13.79, -14) * mm});
            skLineSegment(sketch, "E793", {"start": v(-13.79, -14) * mm, "end": v(-13.9, -14.14) * mm});
            skLineSegment(sketch, "E794", {"start": v(-13.9, -14.14) * mm, "end": v(-14.03, -14.29) * mm});
            skLineSegment(sketch, "E795", {"start": v(-14.03, -14.29) * mm, "end": v(-14.18, -14.41) * mm});
            skLineSegment(sketch, "E796", {"start": v(-14.18, -14.41) * mm, "end": v(-14.36, -14.54) * mm});
            skLineSegment(sketch, "E797", {"start": v(-14.36, -14.54) * mm, "end": v(-14.5, -14.64) * mm});
            skLineSegment(sketch, "E798", {"start": v(-14.5, -14.64) * mm, "end": v(-14.68, -14.71) * mm});
            skLineSegment(sketch, "E799", {"start": v(-14.68, -14.71) * mm, "end": v(-14.85, -14.76) * mm});
            skLineSegment(sketch, "E800", {"start": v(-14.85, -14.76) * mm, "end": v(-15.05, -14.81) * mm});
            skLineSegment(sketch, "E801", {"start": v(-15.05, -14.81) * mm, "end": v(-15.22, -14.84) * mm});
            skLineSegment(sketch, "E802", {"start": v(-15.22, -14.84) * mm, "end": v(-15.42, -14.86) * mm});
            skLineSegment(sketch, "E803", {"start": v(-15.42, -14.86) * mm, "end": v(-16.07, -14.81) * mm});
            skLineSegment(sketch, "E804", {"start": v(-16.07, -14.81) * mm, "end": v(-16.69, -14.74) * mm});
            skLineSegment(sketch, "E805", {"start": v(-16.69, -14.74) * mm, "end": v(-17.28, -14.59) * mm});
            skLineSegment(sketch, "E806", {"start": v(-17.28, -14.59) * mm, "end": v(-17.83, -14.39) * mm});
            skLineSegment(sketch, "E807", {"start": v(-17.83, -14.39) * mm, "end": v(-18.37, -14.12) * mm});
            skLineSegment(sketch, "E808", {"start": v(-18.37, -14.12) * mm, "end": v(-18.9, -13.82) * mm});
            skLineSegment(sketch, "E809", {"start": v(-18.9, -13.82) * mm, "end": v(-19.4, -13.42) * mm});
            skLineSegment(sketch, "E810", {"start": v(-19.4, -13.42) * mm, "end": v(-19.86, -13) * mm});
            skLineSegment(sketch, "E811", {"start": v(-19.86, -13) * mm, "end": v(-20.3, -12.53) * mm});
            skLineSegment(sketch, "E812", {"start": v(-20.3, -12.53) * mm, "end": v(-20.68, -12.03) * mm});
            skLineSegment(sketch, "E813", {"start": v(-20.68, -12.03) * mm, "end": v(-21, -11.51) * mm});
            skLineSegment(sketch, "E814", {"start": v(-21, -11.51) * mm, "end": v(-21.25, -10.97) * mm});
            skLineSegment(sketch, "E815", {"start": v(-21.25, -10.97) * mm, "end": v(-21.48, -10.4) * mm});
            skLineSegment(sketch, "E816", {"start": v(-21.48, -10.4) * mm, "end": v(-21.6, -9.8) * mm});
            skLineSegment(sketch, "E817", {"start": v(-21.6, -9.8) * mm, "end": v(-21.7, -9.2) * mm});
            skLineSegment(sketch, "E818", {"start": v(-21.7, -9.2) * mm, "end": v(-21.72, -8.56) * mm});
            skLineSegment(sketch, "E819", {"start": v(-21.72, -8.56) * mm, "end": v(-21.72, 5.5) * mm});
            skLineSegment(sketch, "E820", {"start": v(-21.72, 5.5) * mm, "end": v(-21.85, 5.55) * mm});
            skLineSegment(sketch, "E821", {"start": v(-21.85, 5.55) * mm, "end": v(-21.97, 5.6) * mm});
            skLineSegment(sketch, "E822", {"start": v(-21.97, 5.6) * mm, "end": v(-22.1, 5.65) * mm});
            skLineSegment(sketch, "E823", {"start": v(-22.1, 5.65) * mm, "end": v(-22.2, 5.7) * mm});
            skLineSegment(sketch, "E824", {"start": v(-22.2, 5.7) * mm, "end": v(-22.32, 5.78) * mm});
            skLineSegment(sketch, "E825", {"start": v(-22.32, 5.78) * mm, "end": v(-22.42, 5.85) * mm});
            skLineSegment(sketch, "E826", {"start": v(-22.42, 5.85) * mm, "end": v(-22.52, 5.95) * mm});
            skLineSegment(sketch, "E827", {"start": v(-22.52, 5.95) * mm, "end": v(-22.62, 6.05) * mm});
            skLineSegment(sketch, "E828", {"start": v(-22.62, 6.05) * mm, "end": v(-22.77, 6.2) * mm});
            skLineSegment(sketch, "E829", {"start": v(-22.77, 6.2) * mm, "end": v(-22.86, 6.35) * mm});
            skLineSegment(sketch, "E830", {"start": v(-22.86, 6.35) * mm, "end": v(-22.96, 6.52) * mm});
            skLineSegment(sketch, "E831", {"start": v(-22.96, 6.52) * mm, "end": v(-23.06, 6.67) * mm});
            skLineSegment(sketch, "E832", {"start": v(-23.06, 6.67) * mm, "end": v(-23.11, 6.84) * mm});
            skLineSegment(sketch, "E833", {"start": v(-23.11, 6.84) * mm, "end": v(-23.16, 7.02) * mm});
            skLineSegment(sketch, "E834", {"start": v(-9.6, -8.34) * mm, "end": v(-9.64, -7.6) * mm});
            skLineSegment(sketch, "E835", {"start": v(-9.64, -7.6) * mm, "end": v(-9.64, 7.41) * mm});
            skLineSegment(sketch, "E836", {"start": v(-9.64, 7.41) * mm, "end": v(-9.62, 7.59) * mm});
            skLineSegment(sketch, "E837", {"start": v(-9.62, 7.59) * mm, "end": v(-9.6, 7.79) * mm});
            skLineSegment(sketch, "E838", {"start": v(-9.6, 7.79) * mm, "end": v(-9.54, 7.96) * mm});
            skLineSegment(sketch, "E839", {"start": v(-9.54, 7.96) * mm, "end": v(-9.5, 8.13) * mm});
            skLineSegment(sketch, "E840", {"start": v(-9.5, 8.13) * mm, "end": v(-9.42, 8.3) * mm});
            skLineSegment(sketch, "E841", {"start": v(-9.42, 8.3) * mm, "end": v(-9.32, 8.48) * mm});
            skLineSegment(sketch, "E842", {"start": v(-9.32, 8.48) * mm, "end": v(-9.2, 8.63) * mm});
            skLineSegment(sketch, "E843", {"start": v(-9.2, 8.63) * mm, "end": v(-9.07, 8.78) * mm});
            skLineSegment(sketch, "E844", {"start": v(-9.07, 8.78) * mm, "end": v(-8.92, 8.9) * mm});
            skLineSegment(sketch, "E845", {"start": v(-8.92, 8.9) * mm, "end": v(-8.78, 9.03) * mm});
            skLineSegment(sketch, "E846", {"start": v(-8.78, 9.03) * mm, "end": v(-8.6, 9.13) * mm});
            skLineSegment(sketch, "E847", {"start": v(-8.6, 9.13) * mm, "end": v(-8.43, 9.2) * mm});
            skLineSegment(sketch, "E848", {"start": v(-8.43, 9.2) * mm, "end": v(-8.25, 9.25) * mm});
            skLineSegment(sketch, "E849", {"start": v(-8.25, 9.25) * mm, "end": v(-8.08, 9.3) * mm});
            skLineSegment(sketch, "E850", {"start": v(-8.08, 9.3) * mm, "end": v(-7.88, 9.32) * mm});
            skLineSegment(sketch, "E851", {"start": v(-7.88, 9.32) * mm, "end": v(-7.7, 9.35) * mm});
            skLineSegment(sketch, "E852", {"start": v(-7.7, 9.35) * mm, "end": v(-7.51, 9.32) * mm});
            skLineSegment(sketch, "E853", {"start": v(-7.51, 9.32) * mm, "end": v(-7.31, 9.3) * mm});
            skLineSegment(sketch, "E854", {"start": v(-7.31, 9.3) * mm, "end": v(-7.14, 9.25) * mm});
            skLineSegment(sketch, "E855", {"start": v(-7.14, 9.25) * mm, "end": v(-6.96, 9.2) * mm});
            skLineSegment(sketch, "E856", {"start": v(-6.96, 9.2) * mm, "end": v(-6.8, 9.13) * mm});
            skLineSegment(sketch, "E857", {"start": v(-6.8, 9.13) * mm, "end": v(-6.62, 9.03) * mm});
            skLineSegment(sketch, "E858", {"start": v(-6.62, 9.03) * mm, "end": v(-6.47, 8.9) * mm});
            skLineSegment(sketch, "E859", {"start": v(-6.47, 8.9) * mm, "end": v(-6.32, 8.78) * mm});
            skLineSegment(sketch, "E860", {"start": v(-6.32, 8.78) * mm, "end": v(-6.2, 8.63) * mm});
            skLineSegment(sketch, "E861", {"start": v(-6.2, 8.63) * mm, "end": v(-6.07, 8.48) * mm});
            skLineSegment(sketch, "E862", {"start": v(-6.07, 8.48) * mm, "end": v(-5.97, 8.3) * mm});
            skLineSegment(sketch, "E863", {"start": v(-5.97, 8.3) * mm, "end": v(-5.9, 8.13) * mm});
            skLineSegment(sketch, "E864", {"start": v(-5.9, 8.13) * mm, "end": v(-5.85, 7.96) * mm});
            skLineSegment(sketch, "E865", {"start": v(-5.85, 7.96) * mm, "end": v(-5.8, 7.79) * mm});
            skLineSegment(sketch, "E866", {"start": v(-5.8, 7.79) * mm, "end": v(-5.77, 7.59) * mm});
            skLineSegment(sketch, "E867", {"start": v(-5.77, 7.59) * mm, "end": v(-5.77, 7.41) * mm});
            skLineSegment(sketch, "E868", {"start": v(-5.77, 7.41) * mm, "end": v(-5.77, -7.6) * mm});
            skLineSegment(sketch, "E869", {"start": v(-5.77, -7.6) * mm, "end": v(-5.75, -7.94) * mm});
            skLineSegment(sketch, "E870", {"start": v(-5.75, -7.94) * mm, "end": v(-5.7, -8.26) * mm});
            skLineSegment(sketch, "E871", {"start": v(-5.7, -8.26) * mm, "end": v(-5.63, -8.58) * mm});
            skLineSegment(sketch, "E872", {"start": v(-5.63, -8.58) * mm, "end": v(-5.53, -8.88) * mm});
            skLineSegment(sketch, "E873", {"start": v(-5.53, -8.88) * mm, "end": v(-5.38, -9.18) * mm});
            skLineSegment(sketch, "E874", {"start": v(-5.38, -9.18) * mm, "end": v(-5.2, -9.45) * mm});
            skLineSegment(sketch, "E875", {"start": v(-5.2, -9.45) * mm, "end": v(-5, -9.73) * mm});
            skLineSegment(sketch, "E876", {"start": v(-5, -9.73) * mm, "end": v(-4.78, -10) * mm});
            skLineSegment(sketch, "E877", {"start": v(-4.78, -10) * mm, "end": v(-4.5, -10.22) * mm});
            skLineSegment(sketch, "E878", {"start": v(-4.5, -10.22) * mm, "end": v(-4.24, -10.42) * mm});
            skLineSegment(sketch, "E879", {"start": v(-4.24, -10.42) * mm, "end": v(-3.96, -10.6) * mm});
            skLineSegment(sketch, "E880", {"start": v(-3.96, -10.6) * mm, "end": v(-3.67, -10.74) * mm});
            skLineSegment(sketch, "E881", {"start": v(-3.67, -10.74) * mm, "end": v(-3.37, -10.84) * mm});
            skLineSegment(sketch, "E882", {"start": v(-3.37, -10.84) * mm, "end": v(-3.05, -10.92) * mm});
            skLineSegment(sketch, "E883", {"start": v(-3.05, -10.92) * mm, "end": v(-2.72, -10.97) * mm});
            skLineSegment(sketch, "E884", {"start": v(-2.72, -10.97) * mm, "end": v(-2.38, -11) * mm});
            skLineSegment(sketch, "E885", {"start": v(-2.38, -11) * mm, "end": v(1.02, -11) * mm});
            skLineSegment(sketch, "E886", {"start": v(1.02, -11) * mm, "end": v(1.02, 7.41) * mm});
            skLineSegment(sketch, "E887", {"start": v(1.02, 7.41) * mm, "end": v(1.02, 7.59) * mm});
            skLineSegment(sketch, "E888", {"start": v(1.02, 7.59) * mm, "end": v(1.05, 7.79) * mm});
            skLineSegment(sketch, "E889", {"start": v(1.05, 7.79) * mm, "end": v(1.1, 7.96) * mm});
            skLineSegment(sketch, "E890", {"start": v(1.1, 7.96) * mm, "end": v(1.15, 8.13) * mm});
            skLineSegment(sketch, "E891", {"start": v(1.15, 8.13) * mm, "end": v(1.22, 8.3) * mm});
            skLineSegment(sketch, "E892", {"start": v(1.22, 8.3) * mm, "end": v(1.32, 8.48) * mm});
            skLineSegment(sketch, "E893", {"start": v(1.32, 8.48) * mm, "end": v(1.44, 8.63) * mm});
            skLineSegment(sketch, "E894", {"start": v(1.44, 8.63) * mm, "end": v(1.57, 8.78) * mm});
            skLineSegment(sketch, "E895", {"start": v(1.57, 8.78) * mm, "end": v(1.72, 8.9) * mm});
            skLineSegment(sketch, "E896", {"start": v(1.72, 8.9) * mm, "end": v(1.87, 9.03) * mm});
            skLineSegment(sketch, "E897", {"start": v(1.87, 9.03) * mm, "end": v(2.04, 9.13) * mm});
            skLineSegment(sketch, "E898", {"start": v(2.04, 9.13) * mm, "end": v(2.21, 9.2) * mm});
            skLineSegment(sketch, "E899", {"start": v(2.21, 9.2) * mm, "end": v(2.39, 9.25) * mm});
            skLineSegment(sketch, "E900", {"start": v(2.39, 9.25) * mm, "end": v(2.56, 9.3) * mm});
            skLineSegment(sketch, "E901", {"start": v(2.56, 9.3) * mm, "end": v(2.76, 9.32) * mm});
            skLineSegment(sketch, "E902", {"start": v(2.76, 9.32) * mm, "end": v(2.96, 9.35) * mm});
            skLineSegment(sketch, "E903", {"start": v(2.96, 9.35) * mm, "end": v(3.13, 9.32) * mm});
            skLineSegment(sketch, "E904", {"start": v(3.13, 9.32) * mm, "end": v(3.33, 9.3) * mm});
            skLineSegment(sketch, "E905", {"start": v(3.33, 9.3) * mm, "end": v(3.5, 9.25) * mm});
            skLineSegment(sketch, "E906", {"start": v(3.5, 9.25) * mm, "end": v(3.68, 9.2) * mm});
            skLineSegment(sketch, "E907", {"start": v(3.68, 9.2) * mm, "end": v(3.85, 9.13) * mm});
            skLineSegment(sketch, "E908", {"start": v(3.85, 9.13) * mm, "end": v(4.02, 9.03) * mm});
            skLineSegment(sketch, "E909", {"start": v(4.02, 9.03) * mm, "end": v(4.17, 8.9) * mm});
            skLineSegment(sketch, "E910", {"start": v(4.17, 8.9) * mm, "end": v(4.32, 8.78) * mm});
            skLineSegment(sketch, "E911", {"start": v(4.32, 8.78) * mm, "end": v(4.45, 8.63) * mm});
            skLineSegment(sketch, "E912", {"start": v(4.45, 8.63) * mm, "end": v(4.57, 8.48) * mm});
            skLineSegment(sketch, "E913", {"start": v(4.57, 8.48) * mm, "end": v(4.67, 8.3) * mm});
            skLineSegment(sketch, "E914", {"start": v(4.67, 8.3) * mm, "end": v(4.74, 8.13) * mm});
            skLineSegment(sketch, "E915", {"start": v(4.74, 8.13) * mm, "end": v(4.8, 7.96) * mm});
            skLineSegment(sketch, "E916", {"start": v(4.8, 7.96) * mm, "end": v(4.84, 7.79) * mm});
            skLineSegment(sketch, "E917", {"start": v(4.84, 7.79) * mm, "end": v(4.87, 7.59) * mm});
            skLineSegment(sketch, "E918", {"start": v(4.87, 7.59) * mm, "end": v(4.9, 7.41) * mm});
            skLineSegment(sketch, "E919", {"start": v(4.9, 7.41) * mm, "end": v(4.9, -12.93) * mm});
            skLineSegment(sketch, "E920", {"start": v(4.9, -12.93) * mm, "end": v(4.87, -13.1) * mm});
            skLineSegment(sketch, "E921", {"start": v(4.87, -13.1) * mm, "end": v(4.84, -13.3) * mm});
            skLineSegment(sketch, "E922", {"start": v(4.84, -13.3) * mm, "end": v(4.8, -13.47) * mm});
            skLineSegment(sketch, "E923", {"start": v(4.8, -13.47) * mm, "end": v(4.74, -13.64) * mm});
            skLineSegment(sketch, "E924", {"start": v(4.74, -13.64) * mm, "end": v(4.67, -13.82) * mm});
            skLineSegment(sketch, "E925", {"start": v(4.67, -13.82) * mm, "end": v(4.57, -14) * mm});
            skLineSegment(sketch, "E926", {"start": v(4.57, -14) * mm, "end": v(4.45, -14.14) * mm});
            skLineSegment(sketch, "E927", {"start": v(4.45, -14.14) * mm, "end": v(4.32, -14.29) * mm});
            skLineSegment(sketch, "E928", {"start": v(4.32, -14.29) * mm, "end": v(4.17, -14.41) * mm});
            skLineSegment(sketch, "E929", {"start": v(4.17, -14.41) * mm, "end": v(4.02, -14.54) * mm});
            skLineSegment(sketch, "E930", {"start": v(4.02, -14.54) * mm, "end": v(3.85, -14.64) * mm});
            skLineSegment(sketch, "E931", {"start": v(3.85, -14.64) * mm, "end": v(3.68, -14.71) * mm});
            skLineSegment(sketch, "E932", {"start": v(3.68, -14.71) * mm, "end": v(3.5, -14.76) * mm});
            skLineSegment(sketch, "E933", {"start": v(3.5, -14.76) * mm, "end": v(3.33, -14.81) * mm});
            skLineSegment(sketch, "E934", {"start": v(3.33, -14.81) * mm, "end": v(3.13, -14.84) * mm});
            skLineSegment(sketch, "E935", {"start": v(3.13, -14.84) * mm, "end": v(2.96, -14.86) * mm});
            skLineSegment(sketch, "E936", {"start": v(2.96, -14.86) * mm, "end": v(-2.38, -14.86) * mm});
            skLineSegment(sketch, "E937", {"start": v(-2.38, -14.86) * mm, "end": v(-3.12, -14.81) * mm});
            skLineSegment(sketch, "E938", {"start": v(-3.12, -14.81) * mm, "end": v(-3.81, -14.71) * mm});
            skLineSegment(sketch, "E939", {"start": v(-3.81, -14.71) * mm, "end": v(-4.5, -14.54) * mm});
            skLineSegment(sketch, "E940", {"start": v(-4.5, -14.54) * mm, "end": v(-5.15, -14.31) * mm});
            skLineSegment(sketch, "E941", {"start": v(-5.15, -14.31) * mm, "end": v(-5.77, -14.02) * mm});
            skLineSegment(sketch, "E942", {"start": v(-5.77, -14.02) * mm, "end": v(-6.4, -13.64) * mm});
            skLineSegment(sketch, "E943", {"start": v(-6.4, -13.64) * mm, "end": v(-6.96, -13.22) * mm});
            skLineSegment(sketch, "E944", {"start": v(-6.96, -13.22) * mm, "end": v(-7.51, -12.73) * mm});
            skLineSegment(sketch, "E945", {"start": v(-7.51, -12.73) * mm, "end": v(-8, -12.18) * mm});
            skLineSegment(sketch, "E946", {"start": v(-8, -12.18) * mm, "end": v(-8.43, -11.61) * mm});
            skLineSegment(sketch, "E947", {"start": v(-8.43, -11.61) * mm, "end": v(-8.8, -11) * mm});
            skLineSegment(sketch, "E948", {"start": v(-8.8, -11) * mm, "end": v(-9.1, -10.37) * mm});
            skLineSegment(sketch, "E949", {"start": v(-9.1, -10.37) * mm, "end": v(-9.32, -9.73) * mm});
            skLineSegment(sketch, "E950", {"start": v(-9.32, -9.73) * mm, "end": v(-9.5, -9.03) * mm});
            skLineSegment(sketch, "E951", {"start": v(-9.5, -9.03) * mm, "end": v(-9.6, -8.34) * mm});
            skLineSegment(sketch, "E952", {"start": v(11.69, -13.3) * mm, "end": v(11.66, -13.1) * mm});
            skLineSegment(sketch, "E953", {"start": v(11.66, -13.1) * mm, "end": v(11.66, -12.93) * mm});
            skLineSegment(sketch, "E954", {"start": v(11.66, -12.93) * mm, "end": v(11.66, 7.41) * mm});
            skLineSegment(sketch, "E955", {"start": v(11.66, 7.41) * mm, "end": v(11.66, 7.59) * mm});
            skLineSegment(sketch, "E956", {"start": v(11.66, 7.59) * mm, "end": v(11.69, 7.79) * mm});
            skLineSegment(sketch, "E957", {"start": v(11.69, 7.79) * mm, "end": v(11.74, 7.96) * mm});
            skLineSegment(sketch, "E958", {"start": v(11.74, 7.96) * mm, "end": v(11.81, 8.13) * mm});
            skLineSegment(sketch, "E959", {"start": v(11.81, 8.13) * mm, "end": v(11.89, 8.3) * mm});
            skLineSegment(sketch, "E960", {"start": v(11.89, 8.3) * mm, "end": v(11.99, 8.48) * mm});
            skLineSegment(sketch, "E961", {"start": v(11.99, 8.48) * mm, "end": v(12.11, 8.63) * mm});
            skLineSegment(sketch, "E962", {"start": v(12.11, 8.63) * mm, "end": v(12.23, 8.78) * mm});
            skLineSegment(sketch, "E963", {"start": v(12.23, 8.78) * mm, "end": v(12.38, 8.9) * mm});
            skLineSegment(sketch, "E964", {"start": v(12.38, 8.9) * mm, "end": v(12.53, 9.03) * mm});
            skLineSegment(sketch, "E965", {"start": v(12.53, 9.03) * mm, "end": v(12.68, 9.13) * mm});
            skLineSegment(sketch, "E966", {"start": v(12.68, 9.13) * mm, "end": v(12.85, 9.2) * mm});
            skLineSegment(sketch, "E967", {"start": v(12.85, 9.2) * mm, "end": v(13.03, 9.25) * mm});
            skLineSegment(sketch, "E968", {"start": v(13.03, 9.25) * mm, "end": v(13.2, 9.3) * mm});
            skLineSegment(sketch, "E969", {"start": v(13.2, 9.3) * mm, "end": v(13.4, 9.32) * mm});
            skLineSegment(sketch, "E970", {"start": v(13.4, 9.32) * mm, "end": v(13.6, 9.35) * mm});
            skLineSegment(sketch, "E971", {"start": v(13.6, 9.35) * mm, "end": v(27.64, 9.35) * mm});
            skLineSegment(sketch, "E972", {"start": v(27.64, 9.35) * mm, "end": v(28.36, 9.3) * mm});
            skLineSegment(sketch, "E973", {"start": v(28.36, 9.3) * mm, "end": v(29.08, 9.2) * mm});
            skLineSegment(sketch, "E974", {"start": v(29.08, 9.2) * mm, "end": v(29.75, 9.03) * mm});
            skLineSegment(sketch, "E975", {"start": v(29.75, 9.03) * mm, "end": v(30.42, 8.8) * mm});
            skLineSegment(sketch, "E976", {"start": v(30.42, 8.8) * mm, "end": v(31.04, 8.5) * mm});
            skLineSegment(sketch, "E977", {"start": v(31.04, 8.5) * mm, "end": v(31.63, 8.13) * mm});
            skLineSegment(sketch, "E978", {"start": v(31.63, 8.13) * mm, "end": v(32.2, 7.71) * mm});
            skLineSegment(sketch, "E979", {"start": v(32.2, 7.71) * mm, "end": v(32.75, 7.22) * mm});
            skLineSegment(sketch, "E980", {"start": v(32.75, 7.22) * mm, "end": v(33.24, 6.67) * mm});
            skLineSegment(sketch, "E981", {"start": v(33.24, 6.67) * mm, "end": v(33.7, 6.1) * mm});
            skLineSegment(sketch, "E982", {"start": v(33.7, 6.1) * mm, "end": v(34.04, 5.48) * mm});
            skLineSegment(sketch, "E983", {"start": v(34.04, 5.48) * mm, "end": v(34.36, 4.86) * mm});
            skLineSegment(sketch, "E984", {"start": v(34.36, 4.86) * mm, "end": v(34.58, 4.21) * mm});
            skLineSegment(sketch, "E985", {"start": v(34.58, 4.21) * mm, "end": v(34.76, 3.52) * mm});
            skLineSegment(sketch, "E986", {"start": v(34.76, 3.52) * mm, "end": v(34.86, 2.83) * mm});
            skLineSegment(sketch, "E987", {"start": v(34.86, 2.83) * mm, "end": v(34.88, 2.08) * mm});
            skLineSegment(sketch, "E988", {"start": v(34.88, 2.08) * mm, "end": v(34.88, -12.93) * mm});
            skLineSegment(sketch, "E989", {"start": v(34.88, -12.93) * mm, "end": v(34.88, -13.1) * mm});
            skLineSegment(sketch, "E990", {"start": v(34.88, -13.1) * mm, "end": v(34.86, -13.3) * mm});
            skLineSegment(sketch, "E991", {"start": v(34.86, -13.3) * mm, "end": v(34.8, -13.47) * mm});
            skLineSegment(sketch, "E992", {"start": v(34.8, -13.47) * mm, "end": v(34.73, -13.64) * mm});
            skLineSegment(sketch, "E993", {"start": v(34.73, -13.64) * mm, "end": v(34.66, -13.82) * mm});
            skLineSegment(sketch, "E994", {"start": v(34.66, -13.82) * mm, "end": v(34.56, -14) * mm});
            skLineSegment(sketch, "E995", {"start": v(34.56, -14) * mm, "end": v(34.43, -14.14) * mm});
            skLineSegment(sketch, "E996", {"start": v(34.43, -14.14) * mm, "end": v(34.31, -14.29) * mm});
            skLineSegment(sketch, "E997", {"start": v(34.31, -14.29) * mm, "end": v(34.16, -14.41) * mm});
            skLineSegment(sketch, "E998", {"start": v(34.16, -14.41) * mm, "end": v(34.01, -14.54) * mm});
            skLineSegment(sketch, "E999", {"start": v(34.01, -14.54) * mm, "end": v(33.86, -14.64) * mm});
            skLineSegment(sketch, "E1000", {"start": v(33.86, -14.64) * mm, "end": v(33.7, -14.71) * mm});
            skLineSegment(sketch, "E1001", {"start": v(33.7, -14.71) * mm, "end": v(33.52, -14.76) * mm});
            skLineSegment(sketch, "E1002", {"start": v(33.52, -14.76) * mm, "end": v(33.34, -14.81) * mm});
            skLineSegment(sketch, "E1003", {"start": v(33.34, -14.81) * mm, "end": v(33.14, -14.84) * mm});
            skLineSegment(sketch, "E1004", {"start": v(33.14, -14.84) * mm, "end": v(32.95, -14.86) * mm});
            skLineSegment(sketch, "E1005", {"start": v(32.95, -14.86) * mm, "end": v(32.75, -14.84) * mm});
            skLineSegment(sketch, "E1006", {"start": v(32.75, -14.84) * mm, "end": v(32.55, -14.81) * mm});
            skLineSegment(sketch, "E1007", {"start": v(32.55, -14.81) * mm, "end": v(32.38, -14.76) * mm});
            skLineSegment(sketch, "E1008", {"start": v(32.38, -14.76) * mm, "end": v(32.2, -14.71) * mm});
            skLineSegment(sketch, "E1009", {"start": v(32.2, -14.71) * mm, "end": v(32.03, -14.64) * mm});
            skLineSegment(sketch, "E1010", {"start": v(32.03, -14.64) * mm, "end": v(31.88, -14.54) * mm});
            skLineSegment(sketch, "E1011", {"start": v(31.88, -14.54) * mm, "end": v(31.73, -14.41) * mm});
            skLineSegment(sketch, "E1012", {"start": v(31.73, -14.41) * mm, "end": v(31.58, -14.29) * mm});
            skLineSegment(sketch, "E1013", {"start": v(31.58, -14.29) * mm, "end": v(31.46, -14.14) * mm});
            skLineSegment(sketch, "E1014", {"start": v(31.46, -14.14) * mm, "end": v(31.33, -14) * mm});
            skLineSegment(sketch, "E1015", {"start": v(31.33, -14) * mm, "end": v(31.23, -13.82) * mm});
            skLineSegment(sketch, "E1016", {"start": v(31.23, -13.82) * mm, "end": v(31.16, -13.64) * mm});
            skLineSegment(sketch, "E1017", {"start": v(31.16, -13.64) * mm, "end": v(31.09, -13.47) * mm});
            skLineSegment(sketch, "E1018", {"start": v(31.09, -13.47) * mm, "end": v(31.04, -13.3) * mm});
            skLineSegment(sketch, "E1019", {"start": v(31.04, -13.3) * mm, "end": v(31.01, -13.1) * mm});
            skLineSegment(sketch, "E1020", {"start": v(31.01, -13.1) * mm, "end": v(31.01, -12.93) * mm});
            skLineSegment(sketch, "E1021", {"start": v(31.01, -12.93) * mm, "end": v(31.01, 2.08) * mm});
            skLineSegment(sketch, "E1022", {"start": v(31.01, 2.08) * mm, "end": v(30.99, 2.43) * mm});
            skLineSegment(sketch, "E1023", {"start": v(30.99, 2.43) * mm, "end": v(30.96, 2.75) * mm});
            skLineSegment(sketch, "E1024", {"start": v(30.96, 2.75) * mm, "end": v(30.86, 3.07) * mm});
            skLineSegment(sketch, "E1025", {"start": v(30.86, 3.07) * mm, "end": v(30.76, 3.37) * mm});
            skLineSegment(sketch, "E1026", {"start": v(30.76, 3.37) * mm, "end": v(30.61, 3.67) * mm});
            skLineSegment(sketch, "E1027", {"start": v(30.61, 3.67) * mm, "end": v(30.47, 3.94) * mm});
            skLineSegment(sketch, "E1028", {"start": v(30.47, 3.94) * mm, "end": v(30.24, 4.21) * mm});
            skLineSegment(sketch, "E1029", {"start": v(30.24, 4.21) * mm, "end": v(30.02, 4.49) * mm});
            skLineSegment(sketch, "E1030", {"start": v(30.02, 4.49) * mm, "end": v(29.77, 4.71) * mm});
            skLineSegment(sketch, "E1031", {"start": v(29.77, 4.71) * mm, "end": v(29.5, 4.9) * mm});
            skLineSegment(sketch, "E1032", {"start": v(29.5, 4.9) * mm, "end": v(29.23, 5.08) * mm});
            skLineSegment(sketch, "E1033", {"start": v(29.23, 5.08) * mm, "end": v(28.93, 5.23) * mm});
            skLineSegment(sketch, "E1034", {"start": v(28.93, 5.23) * mm, "end": v(28.63, 5.33) * mm});
            skLineSegment(sketch, "E1035", {"start": v(28.63, 5.33) * mm, "end": v(28.3, 5.4) * mm});
            skLineSegment(sketch, "E1036", {"start": v(28.3, 5.4) * mm, "end": v(27.96, 5.46) * mm});
            skLineSegment(sketch, "E1037", {"start": v(27.96, 5.46) * mm, "end": v(27.64, 5.48) * mm});
            skLineSegment(sketch, "E1038", {"start": v(27.64, 5.48) * mm, "end": v(25.2, 5.48) * mm});
            skLineSegment(sketch, "E1039", {"start": v(25.2, 5.48) * mm, "end": v(25.2, -12.93) * mm});
            skLineSegment(sketch, "E1040", {"start": v(25.2, -12.93) * mm, "end": v(25.2, -13.1) * mm});
            skLineSegment(sketch, "E1041", {"start": v(25.2, -13.1) * mm, "end": v(25.18, -13.3) * mm});
            skLineSegment(sketch, "E1042", {"start": v(25.18, -13.3) * mm, "end": v(25.13, -13.47) * mm});
            skLineSegment(sketch, "E1043", {"start": v(25.13, -13.47) * mm, "end": v(25.06, -13.64) * mm});
            skLineSegment(sketch, "E1044", {"start": v(25.06, -13.64) * mm, "end": v(24.98, -13.82) * mm});
            skLineSegment(sketch, "E1045", {"start": v(24.98, -13.82) * mm, "end": v(24.88, -14) * mm});
            skLineSegment(sketch, "E1046", {"start": v(24.88, -14) * mm, "end": v(24.76, -14.14) * mm});
            skLineSegment(sketch, "E1047", {"start": v(24.76, -14.14) * mm, "end": v(24.64, -14.29) * mm});
            skLineSegment(sketch, "E1048", {"start": v(24.64, -14.29) * mm, "end": v(24.49, -14.41) * mm});
            skLineSegment(sketch, "E1049", {"start": v(24.49, -14.41) * mm, "end": v(24.34, -14.54) * mm});
            skLineSegment(sketch, "E1050", {"start": v(24.34, -14.54) * mm, "end": v(24.2, -14.64) * mm});
            skLineSegment(sketch, "E1051", {"start": v(24.2, -14.64) * mm, "end": v(24.02, -14.71) * mm});
            skLineSegment(sketch, "E1052", {"start": v(24.02, -14.71) * mm, "end": v(23.84, -14.76) * mm});
            skLineSegment(sketch, "E1053", {"start": v(23.84, -14.76) * mm, "end": v(23.67, -14.81) * mm});
            skLineSegment(sketch, "E1054", {"start": v(23.67, -14.81) * mm, "end": v(23.47, -14.84) * mm});
            skLineSegment(sketch, "E1055", {"start": v(23.47, -14.84) * mm, "end": v(23.27, -14.86) * mm});
            skLineSegment(sketch, "E1056", {"start": v(23.27, -14.86) * mm, "end": v(23.07, -14.84) * mm});
            skLineSegment(sketch, "E1057", {"start": v(23.07, -14.84) * mm, "end": v(22.88, -14.81) * mm});
            skLineSegment(sketch, "E1058", {"start": v(22.88, -14.81) * mm, "end": v(22.7, -14.76) * mm});
            skLineSegment(sketch, "E1059", {"start": v(22.7, -14.76) * mm, "end": v(22.53, -14.71) * mm});
            skLineSegment(sketch, "E1060", {"start": v(22.53, -14.71) * mm, "end": v(22.35, -14.64) * mm});
            skLineSegment(sketch, "E1061", {"start": v(22.35, -14.64) * mm, "end": v(22.2, -14.54) * mm});
            skLineSegment(sketch, "E1062", {"start": v(22.2, -14.54) * mm, "end": v(22.06, -14.41) * mm});
            skLineSegment(sketch, "E1063", {"start": v(22.06, -14.41) * mm, "end": v(21.9, -14.29) * mm});
            skLineSegment(sketch, "E1064", {"start": v(21.9, -14.29) * mm, "end": v(21.78, -14.14) * mm});
            skLineSegment(sketch, "E1065", {"start": v(21.78, -14.14) * mm, "end": v(21.66, -14) * mm});
            skLineSegment(sketch, "E1066", {"start": v(21.66, -14) * mm, "end": v(21.56, -13.82) * mm});
            skLineSegment(sketch, "E1067", {"start": v(21.56, -13.82) * mm, "end": v(21.49, -13.64) * mm});
            skLineSegment(sketch, "E1068", {"start": v(21.49, -13.64) * mm, "end": v(21.41, -13.47) * mm});
            skLineSegment(sketch, "E1069", {"start": v(21.41, -13.47) * mm, "end": v(21.36, -13.3) * mm});
            skLineSegment(sketch, "E1070", {"start": v(21.36, -13.3) * mm, "end": v(21.34, -13.1) * mm});
            skLineSegment(sketch, "E1071", {"start": v(21.34, -13.1) * mm, "end": v(21.34, -12.93) * mm});
            skLineSegment(sketch, "E1072", {"start": v(21.34, -12.93) * mm, "end": v(21.34, 5.48) * mm});
            skLineSegment(sketch, "E1073", {"start": v(21.34, 5.48) * mm, "end": v(15.53, 5.48) * mm});
            skLineSegment(sketch, "E1074", {"start": v(15.53, 5.48) * mm, "end": v(15.53, -12.93) * mm});
            skLineSegment(sketch, "E1075", {"start": v(15.53, -12.93) * mm, "end": v(15.53, -13.1) * mm});
            skLineSegment(sketch, "E1076", {"start": v(15.53, -13.1) * mm, "end": v(15.5, -13.3) * mm});
            skLineSegment(sketch, "E1077", {"start": v(15.5, -13.3) * mm, "end": v(15.46, -13.47) * mm});
            skLineSegment(sketch, "E1078", {"start": v(15.46, -13.47) * mm, "end": v(15.38, -13.64) * mm});
            skLineSegment(sketch, "E1079", {"start": v(15.38, -13.64) * mm, "end": v(15.31, -13.82) * mm});
            skLineSegment(sketch, "E1080", {"start": v(15.31, -13.82) * mm, "end": v(15.21, -14) * mm});
            skLineSegment(sketch, "E1081", {"start": v(15.21, -14) * mm, "end": v(15.09, -14.14) * mm});
            skLineSegment(sketch, "E1082", {"start": v(15.09, -14.14) * mm, "end": v(14.96, -14.29) * mm});
            skLineSegment(sketch, "E1083", {"start": v(14.96, -14.29) * mm, "end": v(14.81, -14.41) * mm});
            skLineSegment(sketch, "E1084", {"start": v(14.81, -14.41) * mm, "end": v(14.67, -14.54) * mm});
            skLineSegment(sketch, "E1085", {"start": v(14.67, -14.54) * mm, "end": v(14.52, -14.64) * mm});
            skLineSegment(sketch, "E1086", {"start": v(14.52, -14.64) * mm, "end": v(14.34, -14.71) * mm});
            skLineSegment(sketch, "E1087", {"start": v(14.34, -14.71) * mm, "end": v(14.17, -14.76) * mm});
            skLineSegment(sketch, "E1088", {"start": v(14.17, -14.76) * mm, "end": v(14, -14.81) * mm});
            skLineSegment(sketch, "E1089", {"start": v(14, -14.81) * mm, "end": v(13.8, -14.84) * mm});
            skLineSegment(sketch, "E1090", {"start": v(13.8, -14.84) * mm, "end": v(13.6, -14.86) * mm});
            skLineSegment(sketch, "E1091", {"start": v(13.6, -14.86) * mm, "end": v(13.4, -14.84) * mm});
            skLineSegment(sketch, "E1092", {"start": v(13.4, -14.84) * mm, "end": v(13.2, -14.81) * mm});
            skLineSegment(sketch, "E1093", {"start": v(13.2, -14.81) * mm, "end": v(13.03, -14.76) * mm});
            skLineSegment(sketch, "E1094", {"start": v(13.03, -14.76) * mm, "end": v(12.85, -14.71) * mm});
            skLineSegment(sketch, "E1095", {"start": v(12.85, -14.71) * mm, "end": v(12.68, -14.64) * mm});
            skLineSegment(sketch, "E1096", {"start": v(12.68, -14.64) * mm, "end": v(12.53, -14.54) * mm});
            skLineSegment(sketch, "E1097", {"start": v(12.53, -14.54) * mm, "end": v(12.38, -14.41) * mm});
            skLineSegment(sketch, "E1098", {"start": v(12.38, -14.41) * mm, "end": v(12.23, -14.29) * mm});
            skLineSegment(sketch, "E1099", {"start": v(12.23, -14.29) * mm, "end": v(12.11, -14.14) * mm});
            skLineSegment(sketch, "E1100", {"start": v(12.11, -14.14) * mm, "end": v(11.99, -14) * mm});
            skLineSegment(sketch, "E1101", {"start": v(11.99, -14) * mm, "end": v(11.89, -13.82) * mm});
            skLineSegment(sketch, "E1102", {"start": v(11.89, -13.82) * mm, "end": v(11.81, -13.64) * mm});
            skLineSegment(sketch, "E1103", {"start": v(11.81, -13.64) * mm, "end": v(11.74, -13.47) * mm});
            skLineSegment(sketch, "E1104", {"start": v(11.74, -13.47) * mm, "end": v(11.69, -13.3) * mm});
            skLineSegment(sketch, "E1105", {"start": v(50.9, -11.93) * mm, "end": v(50.88, -11.76) * mm});
            skLineSegment(sketch, "E1106", {"start": v(50.88, -11.76) * mm, "end": v(50.9, -11.56) * mm});
            skLineSegment(sketch, "E1107", {"start": v(50.9, -11.56) * mm, "end": v(50.93, -11.36) * mm});
            skLineSegment(sketch, "E1108", {"start": v(50.93, -11.36) * mm, "end": v(50.98, -11.19) * mm});
            skLineSegment(sketch, "E1109", {"start": v(50.98, -11.19) * mm, "end": v(51.03, -11.02) * mm});
            skLineSegment(sketch, "E1110", {"start": v(51.03, -11.02) * mm, "end": v(51.1, -10.84) * mm});
            skLineSegment(sketch, "E1111", {"start": v(51.1, -10.84) * mm, "end": v(51.2, -10.7) * mm});
            skLineSegment(sketch, "E1112", {"start": v(51.2, -10.7) * mm, "end": v(51.33, -10.52) * mm});
            skLineSegment(sketch, "E1113", {"start": v(51.33, -10.52) * mm, "end": v(51.45, -10.4) * mm});
            skLineSegment(sketch, "E1114", {"start": v(51.45, -10.4) * mm, "end": v(51.6, -10.25) * mm});
            skLineSegment(sketch, "E1115", {"start": v(51.6, -10.25) * mm, "end": v(51.75, -10.15) * mm});
            skLineSegment(sketch, "E1116", {"start": v(51.75, -10.15) * mm, "end": v(51.92, -10.05) * mm});
            skLineSegment(sketch, "E1117", {"start": v(51.92, -10.05) * mm, "end": v(52.1, -9.95) * mm});
            skLineSegment(sketch, "E1118", {"start": v(52.1, -9.95) * mm, "end": v(52.27, -9.9) * mm});
            skLineSegment(sketch, "E1119", {"start": v(52.27, -9.9) * mm, "end": v(52.44, -9.85) * mm});
            skLineSegment(sketch, "E1120", {"start": v(52.44, -9.85) * mm, "end": v(52.64, -9.82) * mm});
            skLineSegment(sketch, "E1121", {"start": v(52.64, -9.82) * mm, "end": v(52.81, -9.82) * mm});
            skLineSegment(sketch, "E1122", {"start": v(52.81, -9.82) * mm, "end": v(53.01, -9.82) * mm});
            skLineSegment(sketch, "E1123", {"start": v(53.01, -9.82) * mm, "end": v(53.21, -9.85) * mm});
            skLineSegment(sketch, "E1124", {"start": v(53.21, -9.85) * mm, "end": v(53.39, -9.9) * mm});
            skLineSegment(sketch, "E1125", {"start": v(53.39, -9.9) * mm, "end": v(53.56, -9.95) * mm});
            skLineSegment(sketch, "E1126", {"start": v(53.56, -9.95) * mm, "end": v(53.73, -10.02) * mm});
            skLineSegment(sketch, "E1127", {"start": v(53.73, -10.02) * mm, "end": v(53.9, -10.12) * mm});
            skLineSegment(sketch, "E1128", {"start": v(53.9, -10.12) * mm, "end": v(54.05, -10.25) * mm});
            skLineSegment(sketch, "E1129", {"start": v(54.05, -10.25) * mm, "end": v(54.2, -10.37) * mm});
            skLineSegment(sketch, "E1130", {"start": v(54.2, -10.37) * mm, "end": v(54.48, -10.62) * mm});
            skLineSegment(sketch, "E1131", {"start": v(54.48, -10.62) * mm, "end": v(54.75, -10.84) * mm});
            skLineSegment(sketch, "E1132", {"start": v(54.75, -10.84) * mm, "end": v(55.05, -11.02) * mm});
            skLineSegment(sketch, "E1133", {"start": v(55.05, -11.02) * mm, "end": v(55.34, -11.16) * mm});
            skLineSegment(sketch, "E1134", {"start": v(55.34, -11.16) * mm, "end": v(55.67, -11.29) * mm});
            skLineSegment(sketch, "E1135", {"start": v(55.67, -11.29) * mm, "end": v(55.99, -11.36) * mm});
            skLineSegment(sketch, "E1136", {"start": v(55.99, -11.36) * mm, "end": v(56.34, -11.41) * mm});
            skLineSegment(sketch, "E1137", {"start": v(56.34, -11.41) * mm, "end": v(56.66, -11.44) * mm});
            skLineSegment(sketch, "E1138", {"start": v(56.66, -11.44) * mm, "end": v(57.03, -11.41) * mm});
            skLineSegment(sketch, "E1139", {"start": v(57.03, -11.41) * mm, "end": v(57.35, -11.39) * mm});
            skLineSegment(sketch, "E1140", {"start": v(57.35, -11.39) * mm, "end": v(57.68, -11.29) * mm});
            skLineSegment(sketch, "E1141", {"start": v(57.68, -11.29) * mm, "end": v(57.97, -11.19) * mm});
            skLineSegment(sketch, "E1142", {"start": v(57.97, -11.19) * mm, "end": v(58.27, -11.04) * mm});
            skLineSegment(sketch, "E1143", {"start": v(58.27, -11.04) * mm, "end": v(58.57, -10.9) * mm});
            skLineSegment(sketch, "E1144", {"start": v(58.57, -10.9) * mm, "end": v(58.82, -10.67) * mm});
            skLineSegment(sketch, "E1145", {"start": v(58.82, -10.67) * mm, "end": v(59.07, -10.44) * mm});
            skLineSegment(sketch, "E1146", {"start": v(59.07, -10.44) * mm, "end": v(59.31, -10.2) * mm});
            skLineSegment(sketch, "E1147", {"start": v(59.31, -10.2) * mm, "end": v(59.51, -9.92) * mm});
            skLineSegment(sketch, "E1148", {"start": v(59.51, -9.92) * mm, "end": v(59.69, -9.65) * mm});
            skLineSegment(sketch, "E1149", {"start": v(59.69, -9.65) * mm, "end": v(59.8, -9.35) * mm});
            skLineSegment(sketch, "E1150", {"start": v(59.8, -9.35) * mm, "end": v(59.9, -9.06) * mm});
            skLineSegment(sketch, "E1151", {"start": v(59.9, -9.06) * mm, "end": v(60, -8.73) * mm});
            skLineSegment(sketch, "E1152", {"start": v(60, -8.73) * mm, "end": v(60.03, -8.41) * mm});
            skLineSegment(sketch, "E1153", {"start": v(60.03, -8.41) * mm, "end": v(60.06, -8.06) * mm});
            skLineSegment(sketch, "E1154", {"start": v(60.06, -8.06) * mm, "end": v(60.06, -2.73) * mm});
            skLineSegment(sketch, "E1155", {"start": v(60.06, -2.73) * mm, "end": v(60.06, -2.48) * mm});
            skLineSegment(sketch, "E1156", {"start": v(60.06, -2.48) * mm, "end": v(60, -2.23) * mm});
            skLineSegment(sketch, "E1157", {"start": v(60, -2.23) * mm, "end": v(59.96, -2.01) * mm});
            skLineSegment(sketch, "E1158", {"start": v(59.96, -2.01) * mm, "end": v(59.88, -1.79) * mm});
            skLineSegment(sketch, "E1159", {"start": v(59.88, -1.79) * mm, "end": v(59.78, -1.59) * mm});
            skLineSegment(sketch, "E1160", {"start": v(59.78, -1.59) * mm, "end": v(59.66, -1.4) * mm});
            skLineSegment(sketch, "E1161", {"start": v(59.66, -1.4) * mm, "end": v(59.54, -1.2) * mm});
            skLineSegment(sketch, "E1162", {"start": v(59.54, -1.2) * mm, "end": v(59.36, -1.02) * mm});
            skLineSegment(sketch, "E1163", {"start": v(59.36, -1.02) * mm, "end": v(59.19, -0.85) * mm});
            skLineSegment(sketch, "E1164", {"start": v(59.19, -0.85) * mm, "end": v(59, -0.7) * mm});
            skLineSegment(sketch, "E1165", {"start": v(59, -0.7) * mm, "end": v(58.8, -0.6) * mm});
            skLineSegment(sketch, "E1166", {"start": v(58.8, -0.6) * mm, "end": v(58.6, -0.5) * mm});
            skLineSegment(sketch, "E1167", {"start": v(58.6, -0.5) * mm, "end": v(58.37, -0.42) * mm});
            skLineSegment(sketch, "E1168", {"start": v(58.37, -0.42) * mm, "end": v(58.15, -0.35) * mm});
            skLineSegment(sketch, "E1169", {"start": v(58.15, -0.35) * mm, "end": v(57.9, -0.32) * mm});
            skLineSegment(sketch, "E1170", {"start": v(57.9, -0.32) * mm, "end": v(57.65, -0.32) * mm});
            skLineSegment(sketch, "E1171", {"start": v(57.65, -0.32) * mm, "end": v(57.63, -0.32) * mm});
            skLineSegment(sketch, "E1172", {"start": v(57.63, -0.32) * mm, "end": v(57.45, -0.3) * mm});
            skLineSegment(sketch, "E1173", {"start": v(57.45, -0.3) * mm, "end": v(57.25, -0.27) * mm});
            skLineSegment(sketch, "E1174", {"start": v(57.25, -0.27) * mm, "end": v(57.08, -0.23) * mm});
            skLineSegment(sketch, "E1175", {"start": v(57.08, -0.23) * mm, "end": v(56.9, -0.18) * mm});
            skLineSegment(sketch, "E1176", {"start": v(56.9, -0.18) * mm, "end": v(56.73, -0.08) * mm});
            skLineSegment(sketch, "E1177", {"start": v(56.73, -0.08) * mm, "end": v(56.56, 0.02) * mm});
            skLineSegment(sketch, "E1178", {"start": v(56.56, 0.02) * mm, "end": v(56.41, 0.12) * mm});
            skLineSegment(sketch, "E1179", {"start": v(56.41, 0.12) * mm, "end": v(56.26, 0.27) * mm});
            skLineSegment(sketch, "E1180", {"start": v(56.26, 0.27) * mm, "end": v(56.14, 0.42) * mm});
            skLineSegment(sketch, "E1181", {"start": v(56.14, 0.42) * mm, "end": v(56.01, 0.57) * mm});
            skLineSegment(sketch, "E1182", {"start": v(56.01, 0.57) * mm, "end": v(55.92, 0.74) * mm});
            skLineSegment(sketch, "E1183", {"start": v(55.92, 0.74) * mm, "end": v(55.84, 0.9) * mm});
            skLineSegment(sketch, "E1184", {"start": v(55.84, 0.9) * mm, "end": v(55.8, 1.06) * mm});
            skLineSegment(sketch, "E1185", {"start": v(55.8, 1.06) * mm, "end": v(55.74, 1.24) * mm});
            skLineSegment(sketch, "E1186", {"start": v(55.74, 1.24) * mm, "end": v(55.72, 1.44) * mm});
            skLineSegment(sketch, "E1187", {"start": v(55.72, 1.44) * mm, "end": v(55.7, 1.61) * mm});
            skLineSegment(sketch, "E1188", {"start": v(55.7, 1.61) * mm, "end": v(55.72, 1.8) * mm});
            skLineSegment(sketch, "E1189", {"start": v(55.72, 1.8) * mm, "end": v(55.74, 2) * mm});
            skLineSegment(sketch, "E1190", {"start": v(55.74, 2) * mm, "end": v(55.8, 2.18) * mm});
            skLineSegment(sketch, "E1191", {"start": v(55.8, 2.18) * mm, "end": v(55.84, 2.35) * mm});
            skLineSegment(sketch, "E1192", {"start": v(55.84, 2.35) * mm, "end": v(55.92, 2.53) * mm});
            skLineSegment(sketch, "E1193", {"start": v(55.92, 2.53) * mm, "end": v(56.01, 2.7) * mm});
            skLineSegment(sketch, "E1194", {"start": v(56.01, 2.7) * mm, "end": v(56.14, 2.85) * mm});
            skLineSegment(sketch, "E1195", {"start": v(56.14, 2.85) * mm, "end": v(56.26, 3) * mm});
            skLineSegment(sketch, "E1196", {"start": v(56.26, 3) * mm, "end": v(56.41, 3.12) * mm});
            skLineSegment(sketch, "E1197", {"start": v(56.41, 3.12) * mm, "end": v(56.56, 3.25) * mm});
            skLineSegment(sketch, "E1198", {"start": v(56.56, 3.25) * mm, "end": v(56.73, 3.35) * mm});
            skLineSegment(sketch, "E1199", {"start": v(56.73, 3.35) * mm, "end": v(56.9, 3.42) * mm});
            skLineSegment(sketch, "E1200", {"start": v(56.9, 3.42) * mm, "end": v(57.08, 3.47) * mm});
            skLineSegment(sketch, "E1201", {"start": v(57.08, 3.47) * mm, "end": v(57.25, 3.52) * mm});
            skLineSegment(sketch, "E1202", {"start": v(57.25, 3.52) * mm, "end": v(57.45, 3.55) * mm});
            skLineSegment(sketch, "E1203", {"start": v(57.45, 3.55) * mm, "end": v(57.63, 3.55) * mm});
            skLineSegment(sketch, "E1204", {"start": v(57.63, 3.55) * mm, "end": v(57.65, 3.55) * mm});
            skLineSegment(sketch, "E1205", {"start": v(57.65, 3.55) * mm, "end": v(57.9, 3.57) * mm});
            skLineSegment(sketch, "E1206", {"start": v(57.9, 3.57) * mm, "end": v(58.15, 3.6) * mm});
            skLineSegment(sketch, "E1207", {"start": v(58.15, 3.6) * mm, "end": v(58.37, 3.64) * mm});
            skLineSegment(sketch, "E1208", {"start": v(58.37, 3.64) * mm, "end": v(58.6, 3.74) * mm});
            skLineSegment(sketch, "E1209", {"start": v(58.6, 3.74) * mm, "end": v(58.8, 3.84) * mm});
            skLineSegment(sketch, "E1210", {"start": v(58.8, 3.84) * mm, "end": v(59, 3.94) * mm});
            skLineSegment(sketch, "E1211", {"start": v(59, 3.94) * mm, "end": v(59.19, 4.1) * mm});
            skLineSegment(sketch, "E1212", {"start": v(59.19, 4.1) * mm, "end": v(59.36, 4.26) * mm});
            skLineSegment(sketch, "E1213", {"start": v(59.36, 4.26) * mm, "end": v(59.54, 4.44) * mm});
            skLineSegment(sketch, "E1214", {"start": v(59.54, 4.44) * mm, "end": v(59.66, 4.64) * mm});
            skLineSegment(sketch, "E1215", {"start": v(59.66, 4.64) * mm, "end": v(59.78, 4.83) * mm});
            skLineSegment(sketch, "E1216", {"start": v(59.78, 4.83) * mm, "end": v(59.88, 5.03) * mm});
            skLineSegment(sketch, "E1217", {"start": v(59.88, 5.03) * mm, "end": v(59.96, 5.26) * mm});
            skLineSegment(sketch, "E1218", {"start": v(59.96, 5.26) * mm, "end": v(60, 5.48) * mm});
            skLineSegment(sketch, "E1219", {"start": v(60, 5.48) * mm, "end": v(60.06, 5.73) * mm});
            skLineSegment(sketch, "E1220", {"start": v(60.06, 5.73) * mm, "end": v(60.06, 5.98) * mm});
            skLineSegment(sketch, "E1221", {"start": v(60.06, 5.98) * mm, "end": v(60.06, 11.28) * mm});
            skLineSegment(sketch, "E1222", {"start": v(60.06, 11.28) * mm, "end": v(60.03, 11.63) * mm});
            skLineSegment(sketch, "E1223", {"start": v(60.03, 11.63) * mm, "end": v(60, 11.95) * mm});
            skLineSegment(sketch, "E1224", {"start": v(60, 11.95) * mm, "end": v(59.9, 12.28) * mm});
            skLineSegment(sketch, "E1225", {"start": v(59.9, 12.28) * mm, "end": v(59.8, 12.57) * mm});
            skLineSegment(sketch, "E1226", {"start": v(59.8, 12.57) * mm, "end": v(59.69, 12.87) * mm});
            skLineSegment(sketch, "E1227", {"start": v(59.69, 12.87) * mm, "end": v(59.51, 13.14) * mm});
            skLineSegment(sketch, "E1228", {"start": v(59.51, 13.14) * mm, "end": v(59.31, 13.42) * mm});
            skLineSegment(sketch, "E1229", {"start": v(59.31, 13.42) * mm, "end": v(59.07, 13.67) * mm});
            skLineSegment(sketch, "E1230", {"start": v(59.07, 13.67) * mm, "end": v(58.82, 13.89) * mm});
            skLineSegment(sketch, "E1231", {"start": v(58.82, 13.89) * mm, "end": v(58.57, 14.11) * mm});
            skLineSegment(sketch, "E1232", {"start": v(58.57, 14.11) * mm, "end": v(58.27, 14.26) * mm});
            skLineSegment(sketch, "E1233", {"start": v(58.27, 14.26) * mm, "end": v(57.97, 14.4) * mm});
            skLineSegment(sketch, "E1234", {"start": v(57.97, 14.4) * mm, "end": v(57.68, 14.5) * mm});
            skLineSegment(sketch, "E1235", {"start": v(57.68, 14.5) * mm, "end": v(57.35, 14.6) * mm});
            skLineSegment(sketch, "E1236", {"start": v(57.35, 14.6) * mm, "end": v(57.03, 14.63) * mm});
            skLineSegment(sketch, "E1237", {"start": v(57.03, 14.63) * mm, "end": v(56.66, 14.66) * mm});
            skLineSegment(sketch, "E1238", {"start": v(56.66, 14.66) * mm, "end": v(56.34, 14.63) * mm});
            skLineSegment(sketch, "E1239", {"start": v(56.34, 14.63) * mm, "end": v(55.99, 14.58) * mm});
            skLineSegment(sketch, "E1240", {"start": v(55.99, 14.58) * mm, "end": v(55.67, 14.5) * mm});
            skLineSegment(sketch, "E1241", {"start": v(55.67, 14.5) * mm, "end": v(55.37, 14.4) * mm});
            skLineSegment(sketch, "E1242", {"start": v(55.37, 14.4) * mm, "end": v(55.07, 14.26) * mm});
            skLineSegment(sketch, "E1243", {"start": v(55.07, 14.26) * mm, "end": v(54.77, 14.06) * mm});
            skLineSegment(sketch, "E1244", {"start": v(54.77, 14.06) * mm, "end": v(54.48, 13.86) * mm});
            skLineSegment(sketch, "E1245", {"start": v(54.48, 13.86) * mm, "end": v(54.2, 13.62) * mm});
            skLineSegment(sketch, "E1246", {"start": v(54.2, 13.62) * mm, "end": v(54.05, 13.5) * mm});
            skLineSegment(sketch, "E1247", {"start": v(54.05, 13.5) * mm, "end": v(53.9, 13.37) * mm});
            skLineSegment(sketch, "E1248", {"start": v(53.9, 13.37) * mm, "end": v(53.73, 13.27) * mm});
            skLineSegment(sketch, "E1249", {"start": v(53.73, 13.27) * mm, "end": v(53.56, 13.2) * mm});
            skLineSegment(sketch, "E1250", {"start": v(53.56, 13.2) * mm, "end": v(53.39, 13.12) * mm});
            skLineSegment(sketch, "E1251", {"start": v(53.39, 13.12) * mm, "end": v(53.21, 13.07) * mm});
            skLineSegment(sketch, "E1252", {"start": v(53.21, 13.07) * mm, "end": v(53.01, 13.05) * mm});
            skLineSegment(sketch, "E1253", {"start": v(53.01, 13.05) * mm, "end": v(52.81, 13.05) * mm});
            skLineSegment(sketch, "E1254", {"start": v(52.81, 13.05) * mm, "end": v(52.64, 13.05) * mm});
            skLineSegment(sketch, "E1255", {"start": v(52.64, 13.05) * mm, "end": v(52.44, 13.07) * mm});
            skLineSegment(sketch, "E1256", {"start": v(52.44, 13.07) * mm, "end": v(52.27, 13.12) * mm});
            skLineSegment(sketch, "E1257", {"start": v(52.27, 13.12) * mm, "end": v(52.1, 13.17) * mm});
            skLineSegment(sketch, "E1258", {"start": v(52.1, 13.17) * mm, "end": v(51.92, 13.27) * mm});
            skLineSegment(sketch, "E1259", {"start": v(51.92, 13.27) * mm, "end": v(51.75, 13.37) * mm});
            skLineSegment(sketch, "E1260", {"start": v(51.75, 13.37) * mm, "end": v(51.6, 13.47) * mm});
            skLineSegment(sketch, "E1261", {"start": v(51.6, 13.47) * mm, "end": v(51.45, 13.62) * mm});
            skLineSegment(sketch, "E1262", {"start": v(51.45, 13.62) * mm, "end": v(51.33, 13.74) * mm});
            skLineSegment(sketch, "E1263", {"start": v(51.33, 13.74) * mm, "end": v(51.2, 13.91) * mm});
            skLineSegment(sketch, "E1264", {"start": v(51.2, 13.91) * mm, "end": v(51.1, 14.06) * mm});
            skLineSegment(sketch, "E1265", {"start": v(51.1, 14.06) * mm, "end": v(51.03, 14.24) * mm});
            skLineSegment(sketch, "E1266", {"start": v(51.03, 14.24) * mm, "end": v(50.98, 14.4) * mm});
            skLineSegment(sketch, "E1267", {"start": v(50.98, 14.4) * mm, "end": v(50.93, 14.58) * mm});
            skLineSegment(sketch, "E1268", {"start": v(50.93, 14.58) * mm, "end": v(50.9, 14.78) * mm});
            skLineSegment(sketch, "E1269", {"start": v(50.9, 14.78) * mm, "end": v(50.88, 14.98) * mm});
            skLineSegment(sketch, "E1270", {"start": v(50.88, 14.98) * mm, "end": v(50.9, 15.15) * mm});
            skLineSegment(sketch, "E1271", {"start": v(50.9, 15.15) * mm, "end": v(50.93, 15.35) * mm});
            skLineSegment(sketch, "E1272", {"start": v(50.93, 15.35) * mm, "end": v(50.98, 15.53) * mm});
            skLineSegment(sketch, "E1273", {"start": v(50.98, 15.53) * mm, "end": v(51.03, 15.7) * mm});
            skLineSegment(sketch, "E1274", {"start": v(51.03, 15.7) * mm, "end": v(51.13, 15.87) * mm});
            skLineSegment(sketch, "E1275", {"start": v(51.13, 15.87) * mm, "end": v(51.23, 16.02) * mm});
            skLineSegment(sketch, "E1276", {"start": v(51.23, 16.02) * mm, "end": v(51.33, 16.17) * mm});
            skLineSegment(sketch, "E1277", {"start": v(51.33, 16.17) * mm, "end": v(51.48, 16.32) * mm});
            skLineSegment(sketch, "E1278", {"start": v(51.48, 16.32) * mm, "end": v(52.05, 16.84) * mm});
            skLineSegment(sketch, "E1279", {"start": v(52.05, 16.84) * mm, "end": v(52.62, 17.31) * mm});
            skLineSegment(sketch, "E1280", {"start": v(52.62, 17.31) * mm, "end": v(53.24, 17.68) * mm});
            skLineSegment(sketch, "E1281", {"start": v(53.24, 17.68) * mm, "end": v(53.88, 18) * mm});
            skLineSegment(sketch, "E1282", {"start": v(53.88, 18) * mm, "end": v(54.53, 18.23) * mm});
            skLineSegment(sketch, "E1283", {"start": v(54.53, 18.23) * mm, "end": v(55.22, 18.4) * mm});
            skLineSegment(sketch, "E1284", {"start": v(55.22, 18.4) * mm, "end": v(55.94, 18.53) * mm});
            skLineSegment(sketch, "E1285", {"start": v(55.94, 18.53) * mm, "end": v(56.66, 18.55) * mm});
            skLineSegment(sketch, "E1286", {"start": v(56.66, 18.55) * mm, "end": v(57.4, 18.53) * mm});
            skLineSegment(sketch, "E1287", {"start": v(57.4, 18.53) * mm, "end": v(58.12, 18.43) * mm});
            skLineSegment(sketch, "E1288", {"start": v(58.12, 18.43) * mm, "end": v(58.8, 18.25) * mm});
            skLineSegment(sketch, "E1289", {"start": v(58.8, 18.25) * mm, "end": v(59.46, 18.03) * mm});
            skLineSegment(sketch, "E1290", {"start": v(59.46, 18.03) * mm, "end": v(60.08, 17.7) * mm});
            skLineSegment(sketch, "E1291", {"start": v(60.08, 17.7) * mm, "end": v(60.68, 17.36) * mm});
            skLineSegment(sketch, "E1292", {"start": v(60.68, 17.36) * mm, "end": v(61.25, 16.91) * mm});
            skLineSegment(sketch, "E1293", {"start": v(61.25, 16.91) * mm, "end": v(61.8, 16.42) * mm});
            skLineSegment(sketch, "E1294", {"start": v(61.8, 16.42) * mm, "end": v(62.3, 15.87) * mm});
            skLineSegment(sketch, "E1295", {"start": v(62.3, 15.87) * mm, "end": v(62.74, 15.3) * mm});
            skLineSegment(sketch, "E1296", {"start": v(62.74, 15.3) * mm, "end": v(63.08, 14.7) * mm});
            skLineSegment(sketch, "E1297", {"start": v(63.08, 14.7) * mm, "end": v(63.4, 14.09) * mm});
            skLineSegment(sketch, "E1298", {"start": v(63.4, 14.09) * mm, "end": v(63.63, 13.42) * mm});
            skLineSegment(sketch, "E1299", {"start": v(63.63, 13.42) * mm, "end": v(63.8, 12.75) * mm});
            skLineSegment(sketch, "E1300", {"start": v(63.8, 12.75) * mm, "end": v(63.9, 12.03) * mm});
            skLineSegment(sketch, "E1301", {"start": v(63.9, 12.03) * mm, "end": v(63.93, 11.28) * mm});
            skLineSegment(sketch, "E1302", {"start": v(63.93, 11.28) * mm, "end": v(63.93, 5.98) * mm});
            skLineSegment(sketch, "E1303", {"start": v(63.93, 5.98) * mm, "end": v(63.9, 5.33) * mm});
            skLineSegment(sketch, "E1304", {"start": v(63.9, 5.33) * mm, "end": v(63.83, 4.74) * mm});
            skLineSegment(sketch, "E1305", {"start": v(63.83, 4.74) * mm, "end": v(63.68, 4.14) * mm});
            skLineSegment(sketch, "E1306", {"start": v(63.68, 4.14) * mm, "end": v(63.48, 3.6) * mm});
            skLineSegment(sketch, "E1307", {"start": v(63.48, 3.6) * mm, "end": v(63.23, 3.07) * mm});
            skLineSegment(sketch, "E1308", {"start": v(63.23, 3.07) * mm, "end": v(62.94, 2.55) * mm});
            skLineSegment(sketch, "E1309", {"start": v(62.94, 2.55) * mm, "end": v(62.56, 2.08) * mm});
            skLineSegment(sketch, "E1310", {"start": v(62.56, 2.08) * mm, "end": v(62.17, 1.61) * mm});
            skLineSegment(sketch, "E1311", {"start": v(62.17, 1.61) * mm, "end": v(62.56, 1.16) * mm});
            skLineSegment(sketch, "E1312", {"start": v(62.56, 1.16) * mm, "end": v(62.94, 0.7) * mm});
            skLineSegment(sketch, "E1313", {"start": v(62.94, 0.7) * mm, "end": v(63.23, 0.17) * mm});
            skLineSegment(sketch, "E1314", {"start": v(63.23, 0.17) * mm, "end": v(63.48, -0.35) * mm});
            skLineSegment(sketch, "E1315", {"start": v(63.48, -0.35) * mm, "end": v(63.68, -0.9) * mm});
            skLineSegment(sketch, "E1316", {"start": v(63.68, -0.9) * mm, "end": v(63.83, -1.5) * mm});
            skLineSegment(sketch, "E1317", {"start": v(63.83, -1.5) * mm, "end": v(63.9, -2.09) * mm});
            skLineSegment(sketch, "E1318", {"start": v(63.9, -2.09) * mm, "end": v(63.93, -2.73) * mm});
            skLineSegment(sketch, "E1319", {"start": v(63.93, -2.73) * mm, "end": v(63.93, -8.06) * mm});
            skLineSegment(sketch, "E1320", {"start": v(63.93, -8.06) * mm, "end": v(63.9, -8.8) * mm});
            skLineSegment(sketch, "E1321", {"start": v(63.9, -8.8) * mm, "end": v(63.8, -9.53) * mm});
            skLineSegment(sketch, "E1322", {"start": v(63.8, -9.53) * mm, "end": v(63.63, -10.2) * mm});
            skLineSegment(sketch, "E1323", {"start": v(63.63, -10.2) * mm, "end": v(63.4, -10.87) * mm});
            skLineSegment(sketch, "E1324", {"start": v(63.4, -10.87) * mm, "end": v(63.08, -11.49) * mm});
            skLineSegment(sketch, "E1325", {"start": v(63.08, -11.49) * mm, "end": v(62.74, -12.08) * mm});
            skLineSegment(sketch, "E1326", {"start": v(62.74, -12.08) * mm, "end": v(62.3, -12.65) * mm});
            skLineSegment(sketch, "E1327", {"start": v(62.3, -12.65) * mm, "end": v(61.8, -13.2) * mm});
            skLineSegment(sketch, "E1328", {"start": v(61.8, -13.2) * mm, "end": v(61.25, -13.7) * mm});
            skLineSegment(sketch, "E1329", {"start": v(61.25, -13.7) * mm, "end": v(60.68, -14.14) * mm});
            skLineSegment(sketch, "E1330", {"start": v(60.68, -14.14) * mm, "end": v(60.08, -14.49) * mm});
            skLineSegment(sketch, "E1331", {"start": v(60.08, -14.49) * mm, "end": v(59.46, -14.81) * mm});
            skLineSegment(sketch, "E1332", {"start": v(59.46, -14.81) * mm, "end": v(58.8, -15.03) * mm});
            skLineSegment(sketch, "E1333", {"start": v(58.8, -15.03) * mm, "end": v(58.12, -15.2) * mm});
            skLineSegment(sketch, "E1334", {"start": v(58.12, -15.2) * mm, "end": v(57.4, -15.3) * mm});
            skLineSegment(sketch, "E1335", {"start": v(57.4, -15.3) * mm, "end": v(56.66, -15.33) * mm});
            skLineSegment(sketch, "E1336", {"start": v(56.66, -15.33) * mm, "end": v(55.94, -15.3) * mm});
            skLineSegment(sketch, "E1337", {"start": v(55.94, -15.3) * mm, "end": v(55.22, -15.18) * mm});
            skLineSegment(sketch, "E1338", {"start": v(55.22, -15.18) * mm, "end": v(54.53, -15) * mm});
            skLineSegment(sketch, "E1339", {"start": v(54.53, -15) * mm, "end": v(53.88, -14.79) * mm});
            skLineSegment(sketch, "E1340", {"start": v(53.88, -14.79) * mm, "end": v(53.24, -14.46) * mm});
            skLineSegment(sketch, "E1341", {"start": v(53.24, -14.46) * mm, "end": v(52.62, -14.1) * mm});
            skLineSegment(sketch, "E1342", {"start": v(52.62, -14.1) * mm, "end": v(52.05, -13.62) * mm});
            skLineSegment(sketch, "E1343", {"start": v(52.05, -13.62) * mm, "end": v(51.48, -13.1) * mm});
            skLineSegment(sketch, "E1344", {"start": v(51.48, -13.1) * mm, "end": v(51.33, -12.95) * mm});
            skLineSegment(sketch, "E1345", {"start": v(51.33, -12.95) * mm, "end": v(51.23, -12.8) * mm});
            skLineSegment(sketch, "E1346", {"start": v(51.23, -12.8) * mm, "end": v(51.13, -12.65) * mm});
            skLineSegment(sketch, "E1347", {"start": v(51.13, -12.65) * mm, "end": v(51.03, -12.48) * mm});
            skLineSegment(sketch, "E1348", {"start": v(51.03, -12.48) * mm, "end": v(50.98, -12.3) * mm});
            skLineSegment(sketch, "E1349", {"start": v(50.98, -12.3) * mm, "end": v(50.93, -12.13) * mm});
            skLineSegment(sketch, "E1350", {"start": v(50.93, -12.13) * mm, "end": v(50.9, -11.93) * mm});
            skLineSegment(sketch, "E1351", {"start": v(69.26, -8.8) * mm, "end": v(69.21, -8.06) * mm});
            skLineSegment(sketch, "E1352", {"start": v(69.21, -8.06) * mm, "end": v(69.21, -1.32) * mm});
            skLineSegment(sketch, "E1353", {"start": v(69.21, -1.32) * mm, "end": v(69.24, -1.14) * mm});
            skLineSegment(sketch, "E1354", {"start": v(69.24, -1.14) * mm, "end": v(69.26, -0.94) * mm});
            skLineSegment(sketch, "E1355", {"start": v(69.26, -0.94) * mm, "end": v(69.3, -0.77) * mm});
            skLineSegment(sketch, "E1356", {"start": v(69.3, -0.77) * mm, "end": v(69.36, -0.6) * mm});
            skLineSegment(sketch, "E1357", {"start": v(69.36, -0.6) * mm, "end": v(69.43, -0.42) * mm});
            skLineSegment(sketch, "E1358", {"start": v(69.43, -0.42) * mm, "end": v(69.53, -0.25) * mm});
            skLineSegment(sketch, "E1359", {"start": v(69.53, -0.25) * mm, "end": v(69.66, -0.1) * mm});
            skLineSegment(sketch, "E1360", {"start": v(69.66, -0.1) * mm, "end": v(69.78, 0.05) * mm});
            skLineSegment(sketch, "E1361", {"start": v(69.78, 0.05) * mm, "end": v(69.93, 0.17) * mm});
            skLineSegment(sketch, "E1362", {"start": v(69.93, 0.17) * mm, "end": v(70.08, 0.3) * mm});
            skLineSegment(sketch, "E1363", {"start": v(70.08, 0.3) * mm, "end": v(70.25, 0.4) * mm});
            skLineSegment(sketch, "E1364", {"start": v(70.25, 0.4) * mm, "end": v(70.43, 0.47) * mm});
            skLineSegment(sketch, "E1365", {"start": v(70.43, 0.47) * mm, "end": v(70.6, 0.52) * mm});
            skLineSegment(sketch, "E1366", {"start": v(70.6, 0.52) * mm, "end": v(70.77, 0.57) * mm});
            skLineSegment(sketch, "E1367", {"start": v(70.77, 0.57) * mm, "end": v(70.97, 0.6) * mm});
            skLineSegment(sketch, "E1368", {"start": v(70.97, 0.6) * mm, "end": v(71.15, 0.62) * mm});
            skLineSegment(sketch, "E1369", {"start": v(71.15, 0.62) * mm, "end": v(71.34, 0.6) * mm});
            skLineSegment(sketch, "E1370", {"start": v(71.34, 0.6) * mm, "end": v(71.54, 0.57) * mm});
            skLineSegment(sketch, "E1371", {"start": v(71.54, 0.57) * mm, "end": v(71.72, 0.52) * mm});
            skLineSegment(sketch, "E1372", {"start": v(71.72, 0.52) * mm, "end": v(71.89, 0.47) * mm});
            skLineSegment(sketch, "E1373", {"start": v(71.89, 0.47) * mm, "end": v(72.06, 0.4) * mm});
            skLineSegment(sketch, "E1374", {"start": v(72.06, 0.4) * mm, "end": v(72.24, 0.3) * mm});
            skLineSegment(sketch, "E1375", {"start": v(72.24, 0.3) * mm, "end": v(72.39, 0.17) * mm});
            skLineSegment(sketch, "E1376", {"start": v(72.39, 0.17) * mm, "end": v(72.53, 0.05) * mm});
            skLineSegment(sketch, "E1377", {"start": v(72.53, 0.05) * mm, "end": v(72.66, -0.1) * mm});
            skLineSegment(sketch, "E1378", {"start": v(72.66, -0.1) * mm, "end": v(72.78, -0.25) * mm});
            skLineSegment(sketch, "E1379", {"start": v(72.78, -0.25) * mm, "end": v(72.88, -0.42) * mm});
            skLineSegment(sketch, "E1380", {"start": v(72.88, -0.42) * mm, "end": v(72.96, -0.6) * mm});
            skLineSegment(sketch, "E1381", {"start": v(72.96, -0.6) * mm, "end": v(73, -0.77) * mm});
            skLineSegment(sketch, "E1382", {"start": v(73, -0.77) * mm, "end": v(73.06, -0.94) * mm});
            skLineSegment(sketch, "E1383", {"start": v(73.06, -0.94) * mm, "end": v(73.08, -1.14) * mm});
            skLineSegment(sketch, "E1384", {"start": v(73.08, -1.14) * mm, "end": v(73.08, -1.32) * mm});
            skLineSegment(sketch, "E1385", {"start": v(73.08, -1.32) * mm, "end": v(73.08, -8.06) * mm});
            skLineSegment(sketch, "E1386", {"start": v(73.08, -8.06) * mm, "end": v(73.1, -8.41) * mm});
            skLineSegment(sketch, "E1387", {"start": v(73.1, -8.41) * mm, "end": v(73.15, -8.76) * mm});
            skLineSegment(sketch, "E1388", {"start": v(73.15, -8.76) * mm, "end": v(73.23, -9.08) * mm});
            skLineSegment(sketch, "E1389", {"start": v(73.23, -9.08) * mm, "end": v(73.33, -9.38) * mm});
            skLineSegment(sketch, "E1390", {"start": v(73.33, -9.38) * mm, "end": v(73.48, -9.68) * mm});
            skLineSegment(sketch, "E1391", {"start": v(73.48, -9.68) * mm, "end": v(73.65, -9.95) * mm});
            skLineSegment(sketch, "E1392", {"start": v(73.65, -9.95) * mm, "end": v(73.85, -10.22) * mm});
            skLineSegment(sketch, "E1393", {"start": v(73.85, -10.22) * mm, "end": v(74.07, -10.47) * mm});
            skLineSegment(sketch, "E1394", {"start": v(74.07, -10.47) * mm, "end": v(74.35, -10.7) * mm});
            skLineSegment(sketch, "E1395", {"start": v(74.35, -10.7) * mm, "end": v(74.62, -10.92) * mm});
            skLineSegment(sketch, "E1396", {"start": v(74.62, -10.92) * mm, "end": v(74.9, -11.06) * mm});
            skLineSegment(sketch, "E1397", {"start": v(74.9, -11.06) * mm, "end": v(75.19, -11.21) * mm});
            skLineSegment(sketch, "E1398", {"start": v(75.19, -11.21) * mm, "end": v(75.49, -11.31) * mm});
            skLineSegment(sketch, "E1399", {"start": v(75.49, -11.31) * mm, "end": v(75.8, -11.41) * mm});
            skLineSegment(sketch, "E1400", {"start": v(75.8, -11.41) * mm, "end": v(76.13, -11.44) * mm});
            skLineSegment(sketch, "E1401", {"start": v(76.13, -11.44) * mm, "end": v(76.48, -11.46) * mm});
            skLineSegment(sketch, "E1402", {"start": v(76.48, -11.46) * mm, "end": v(76.83, -11.44) * mm});
            skLineSegment(sketch, "E1403", {"start": v(76.83, -11.44) * mm, "end": v(77.15, -11.41) * mm});
            skLineSegment(sketch, "E1404", {"start": v(77.15, -11.41) * mm, "end": v(77.47, -11.31) * mm});
            skLineSegment(sketch, "E1405", {"start": v(77.47, -11.31) * mm, "end": v(77.77, -11.21) * mm});
            skLineSegment(sketch, "E1406", {"start": v(77.77, -11.21) * mm, "end": v(78.07, -11.06) * mm});
            skLineSegment(sketch, "E1407", {"start": v(78.07, -11.06) * mm, "end": v(78.34, -10.92) * mm});
            skLineSegment(sketch, "E1408", {"start": v(78.34, -10.92) * mm, "end": v(78.61, -10.7) * mm});
            skLineSegment(sketch, "E1409", {"start": v(78.61, -10.7) * mm, "end": v(78.88, -10.47) * mm});
            skLineSegment(sketch, "E1410", {"start": v(78.88, -10.47) * mm, "end": v(79.1, -10.22) * mm});
            skLineSegment(sketch, "E1411", {"start": v(79.1, -10.22) * mm, "end": v(79.3, -9.95) * mm});
            skLineSegment(sketch, "E1412", {"start": v(79.3, -9.95) * mm, "end": v(79.48, -9.68) * mm});
            skLineSegment(sketch, "E1413", {"start": v(79.48, -9.68) * mm, "end": v(79.63, -9.38) * mm});
            skLineSegment(sketch, "E1414", {"start": v(79.63, -9.38) * mm, "end": v(79.73, -9.08) * mm});
            skLineSegment(sketch, "E1415", {"start": v(79.73, -9.08) * mm, "end": v(79.8, -8.76) * mm});
            skLineSegment(sketch, "E1416", {"start": v(79.8, -8.76) * mm, "end": v(79.85, -8.41) * mm});
            skLineSegment(sketch, "E1417", {"start": v(79.85, -8.41) * mm, "end": v(79.88, -8.06) * mm});
            skLineSegment(sketch, "E1418", {"start": v(79.88, -8.06) * mm, "end": v(79.88, -1.32) * mm});
            skLineSegment(sketch, "E1419", {"start": v(79.88, -1.32) * mm, "end": v(79.88, -1.14) * mm});
            skLineSegment(sketch, "E1420", {"start": v(79.88, -1.14) * mm, "end": v(79.9, -0.94) * mm});
            skLineSegment(sketch, "E1421", {"start": v(79.9, -0.94) * mm, "end": v(79.95, -0.77) * mm});
            skLineSegment(sketch, "E1422", {"start": v(79.95, -0.77) * mm, "end": v(80, -0.6) * mm});
            skLineSegment(sketch, "E1423", {"start": v(80, -0.6) * mm, "end": v(80.08, -0.42) * mm});
            skLineSegment(sketch, "E1424", {"start": v(80.08, -0.42) * mm, "end": v(80.17, -0.25) * mm});
            skLineSegment(sketch, "E1425", {"start": v(80.17, -0.25) * mm, "end": v(80.3, -0.1) * mm});
            skLineSegment(sketch, "E1426", {"start": v(80.3, -0.1) * mm, "end": v(80.42, 0.05) * mm});
            skLineSegment(sketch, "E1427", {"start": v(80.42, 0.05) * mm, "end": v(80.57, 0.17) * mm});
            skLineSegment(sketch, "E1428", {"start": v(80.57, 0.17) * mm, "end": v(80.72, 0.3) * mm});
            skLineSegment(sketch, "E1429", {"start": v(80.72, 0.3) * mm, "end": v(80.9, 0.4) * mm});
            skLineSegment(sketch, "E1430", {"start": v(80.9, 0.4) * mm, "end": v(81.07, 0.47) * mm});
            skLineSegment(sketch, "E1431", {"start": v(81.07, 0.47) * mm, "end": v(81.24, 0.52) * mm});
            skLineSegment(sketch, "E1432", {"start": v(81.24, 0.52) * mm, "end": v(81.41, 0.57) * mm});
            skLineSegment(sketch, "E1433", {"start": v(81.41, 0.57) * mm, "end": v(81.61, 0.6) * mm});
            skLineSegment(sketch, "E1434", {"start": v(81.61, 0.6) * mm, "end": v(81.81, 0.62) * mm});
            skLineSegment(sketch, "E1435", {"start": v(81.81, 0.62) * mm, "end": v(81.99, 0.6) * mm});
            skLineSegment(sketch, "E1436", {"start": v(81.99, 0.6) * mm, "end": v(82.18, 0.57) * mm});
            skLineSegment(sketch, "E1437", {"start": v(82.18, 0.57) * mm, "end": v(82.36, 0.52) * mm});
            skLineSegment(sketch, "E1438", {"start": v(82.36, 0.52) * mm, "end": v(82.53, 0.47) * mm});
            skLineSegment(sketch, "E1439", {"start": v(82.53, 0.47) * mm, "end": v(82.7, 0.4) * mm});
            skLineSegment(sketch, "E1440", {"start": v(82.7, 0.4) * mm, "end": v(82.88, 0.3) * mm});
            skLineSegment(sketch, "E1441", {"start": v(82.88, 0.3) * mm, "end": v(83.03, 0.17) * mm});
            skLineSegment(sketch, "E1442", {"start": v(83.03, 0.17) * mm, "end": v(83.18, 0.05) * mm});
            skLineSegment(sketch, "E1443", {"start": v(83.18, 0.05) * mm, "end": v(83.3, -0.1) * mm});
            skLineSegment(sketch, "E1444", {"start": v(83.3, -0.1) * mm, "end": v(83.42, -0.25) * mm});
            skLineSegment(sketch, "E1445", {"start": v(83.42, -0.25) * mm, "end": v(83.52, -0.42) * mm});
            skLineSegment(sketch, "E1446", {"start": v(83.52, -0.42) * mm, "end": v(83.6, -0.6) * mm});
            skLineSegment(sketch, "E1447", {"start": v(83.6, -0.6) * mm, "end": v(83.65, -0.77) * mm});
            skLineSegment(sketch, "E1448", {"start": v(83.65, -0.77) * mm, "end": v(83.7, -0.94) * mm});
            skLineSegment(sketch, "E1449", {"start": v(83.7, -0.94) * mm, "end": v(83.72, -1.14) * mm});
            skLineSegment(sketch, "E1450", {"start": v(83.72, -1.14) * mm, "end": v(83.75, -1.32) * mm});
            skLineSegment(sketch, "E1451", {"start": v(83.75, -1.32) * mm, "end": v(83.75, -8.06) * mm});
            skLineSegment(sketch, "E1452", {"start": v(83.75, -8.06) * mm, "end": v(83.7, -8.8) * mm});
            skLineSegment(sketch, "E1453", {"start": v(83.7, -8.8) * mm, "end": v(83.6, -9.53) * mm});
            skLineSegment(sketch, "E1454", {"start": v(83.6, -9.53) * mm, "end": v(83.42, -10.2) * mm});
            skLineSegment(sketch, "E1455", {"start": v(83.42, -10.2) * mm, "end": v(83.2, -10.87) * mm});
            skLineSegment(sketch, "E1456", {"start": v(83.2, -10.87) * mm, "end": v(82.9, -11.49) * mm});
            skLineSegment(sketch, "E1457", {"start": v(82.9, -11.49) * mm, "end": v(82.53, -12.08) * mm});
            skLineSegment(sketch, "E1458", {"start": v(82.53, -12.08) * mm, "end": v(82.1, -12.65) * mm});
            skLineSegment(sketch, "E1459", {"start": v(82.1, -12.65) * mm, "end": v(81.61, -13.2) * mm});
            skLineSegment(sketch, "E1460", {"start": v(81.61, -13.2) * mm, "end": v(81.07, -13.7) * mm});
            skLineSegment(sketch, "E1461", {"start": v(81.07, -13.7) * mm, "end": v(80.5, -14.14) * mm});
            skLineSegment(sketch, "E1462", {"start": v(80.5, -14.14) * mm, "end": v(79.88, -14.49) * mm});
            skLineSegment(sketch, "E1463", {"start": v(79.88, -14.49) * mm, "end": v(79.26, -14.81) * mm});
            skLineSegment(sketch, "E1464", {"start": v(79.26, -14.81) * mm, "end": v(78.61, -15.03) * mm});
            skLineSegment(sketch, "E1465", {"start": v(78.61, -15.03) * mm, "end": v(77.92, -15.2) * mm});
            skLineSegment(sketch, "E1466", {"start": v(77.92, -15.2) * mm, "end": v(77.22, -15.3) * mm});
            skLineSegment(sketch, "E1467", {"start": v(77.22, -15.3) * mm, "end": v(76.48, -15.33) * mm});
            skLineSegment(sketch, "E1468", {"start": v(76.48, -15.33) * mm, "end": v(75.73, -15.3) * mm});
            skLineSegment(sketch, "E1469", {"start": v(75.73, -15.3) * mm, "end": v(75.04, -15.2) * mm});
            skLineSegment(sketch, "E1470", {"start": v(75.04, -15.2) * mm, "end": v(74.35, -15.03) * mm});
            skLineSegment(sketch, "E1471", {"start": v(74.35, -15.03) * mm, "end": v(73.7, -14.81) * mm});
            skLineSegment(sketch, "E1472", {"start": v(73.7, -14.81) * mm, "end": v(73.08, -14.49) * mm});
            skLineSegment(sketch, "E1473", {"start": v(73.08, -14.49) * mm, "end": v(72.46, -14.14) * mm});
            skLineSegment(sketch, "E1474", {"start": v(72.46, -14.14) * mm, "end": v(71.89, -13.7) * mm});
            skLineSegment(sketch, "E1475", {"start": v(71.89, -13.7) * mm, "end": v(71.34, -13.2) * mm});
            skLineSegment(sketch, "E1476", {"start": v(71.34, -13.2) * mm, "end": v(70.85, -12.65) * mm});
            skLineSegment(sketch, "E1477", {"start": v(70.85, -12.65) * mm, "end": v(70.43, -12.08) * mm});
            skLineSegment(sketch, "E1478", {"start": v(70.43, -12.08) * mm, "end": v(70.05, -11.49) * mm});
            skLineSegment(sketch, "E1479", {"start": v(70.05, -11.49) * mm, "end": v(69.76, -10.87) * mm});
            skLineSegment(sketch, "E1480", {"start": v(69.76, -10.87) * mm, "end": v(69.53, -10.2) * mm});
            skLineSegment(sketch, "E1481", {"start": v(69.53, -10.2) * mm, "end": v(69.36, -9.53) * mm});
            skLineSegment(sketch, "E1482", {"start": v(69.36, -9.53) * mm, "end": v(69.26, -8.8) * mm});
            skLineSegment(sketch, "E1483", {"start": v(69.26, 12.03) * mm, "end": v(69.36, 12.75) * mm});
            skLineSegment(sketch, "E1484", {"start": v(69.36, 12.75) * mm, "end": v(69.53, 13.42) * mm});
            skLineSegment(sketch, "E1485", {"start": v(69.53, 13.42) * mm, "end": v(69.76, 14.09) * mm});
            skLineSegment(sketch, "E1486", {"start": v(69.76, 14.09) * mm, "end": v(70.05, 14.7) * mm});
            skLineSegment(sketch, "E1487", {"start": v(70.05, 14.7) * mm, "end": v(70.43, 15.3) * mm});
            skLineSegment(sketch, "E1488", {"start": v(70.43, 15.3) * mm, "end": v(70.85, 15.87) * mm});
            skLineSegment(sketch, "E1489", {"start": v(70.85, 15.87) * mm, "end": v(71.34, 16.42) * mm});
            skLineSegment(sketch, "E1490", {"start": v(71.34, 16.42) * mm, "end": v(71.89, 16.91) * mm});
            skLineSegment(sketch, "E1491", {"start": v(71.89, 16.91) * mm, "end": v(72.46, 17.36) * mm});
            skLineSegment(sketch, "E1492", {"start": v(72.46, 17.36) * mm, "end": v(73.08, 17.7) * mm});
            skLineSegment(sketch, "E1493", {"start": v(73.08, 17.7) * mm, "end": v(73.7, 18.03) * mm});
            skLineSegment(sketch, "E1494", {"start": v(73.7, 18.03) * mm, "end": v(74.35, 18.25) * mm});
            skLineSegment(sketch, "E1495", {"start": v(74.35, 18.25) * mm, "end": v(75.04, 18.43) * mm});
            skLineSegment(sketch, "E1496", {"start": v(75.04, 18.43) * mm, "end": v(75.73, 18.53) * mm});
            skLineSegment(sketch, "E1497", {"start": v(75.73, 18.53) * mm, "end": v(76.48, 18.55) * mm});
            skLineSegment(sketch, "E1498", {"start": v(76.48, 18.55) * mm, "end": v(77.22, 18.53) * mm});
            skLineSegment(sketch, "E1499", {"start": v(77.22, 18.53) * mm, "end": v(77.92, 18.43) * mm});
            skLineSegment(sketch, "E1500", {"start": v(77.92, 18.43) * mm, "end": v(78.61, 18.25) * mm});
            skLineSegment(sketch, "E1501", {"start": v(78.61, 18.25) * mm, "end": v(79.26, 18.03) * mm});
            skLineSegment(sketch, "E1502", {"start": v(79.26, 18.03) * mm, "end": v(79.88, 17.7) * mm});
            skLineSegment(sketch, "E1503", {"start": v(79.88, 17.7) * mm, "end": v(80.5, 17.36) * mm});
            skLineSegment(sketch, "E1504", {"start": v(80.5, 17.36) * mm, "end": v(81.07, 16.91) * mm});
            skLineSegment(sketch, "E1505", {"start": v(81.07, 16.91) * mm, "end": v(81.61, 16.42) * mm});
            skLineSegment(sketch, "E1506", {"start": v(81.61, 16.42) * mm, "end": v(82.1, 15.87) * mm});
            skLineSegment(sketch, "E1507", {"start": v(82.1, 15.87) * mm, "end": v(82.53, 15.3) * mm});
            skLineSegment(sketch, "E1508", {"start": v(82.53, 15.3) * mm, "end": v(82.9, 14.7) * mm});
            skLineSegment(sketch, "E1509", {"start": v(82.9, 14.7) * mm, "end": v(83.2, 14.09) * mm});
            skLineSegment(sketch, "E1510", {"start": v(83.2, 14.09) * mm, "end": v(83.42, 13.42) * mm});
            skLineSegment(sketch, "E1511", {"start": v(83.42, 13.42) * mm, "end": v(83.6, 12.75) * mm});
            skLineSegment(sketch, "E1512", {"start": v(83.6, 12.75) * mm, "end": v(83.7, 12.03) * mm});
            skLineSegment(sketch, "E1513", {"start": v(83.7, 12.03) * mm, "end": v(83.75, 11.28) * mm});
            skLineSegment(sketch, "E1514", {"start": v(83.75, 11.28) * mm, "end": v(83.75, 4.54) * mm});
            skLineSegment(sketch, "E1515", {"start": v(83.75, 4.54) * mm, "end": v(83.72, 4.36) * mm});
            skLineSegment(sketch, "E1516", {"start": v(83.72, 4.36) * mm, "end": v(83.7, 4.17) * mm});
            skLineSegment(sketch, "E1517", {"start": v(83.7, 4.17) * mm, "end": v(83.65, 4) * mm});
            skLineSegment(sketch, "E1518", {"start": v(83.65, 4) * mm, "end": v(83.6, 3.82) * mm});
            skLineSegment(sketch, "E1519", {"start": v(83.6, 3.82) * mm, "end": v(83.52, 3.64) * mm});
            skLineSegment(sketch, "E1520", {"start": v(83.52, 3.64) * mm, "end": v(83.42, 3.47) * mm});
            skLineSegment(sketch, "E1521", {"start": v(83.42, 3.47) * mm, "end": v(83.3, 3.32) * mm});
            skLineSegment(sketch, "E1522", {"start": v(83.3, 3.32) * mm, "end": v(83.18, 3.17) * mm});
            skLineSegment(sketch, "E1523", {"start": v(83.18, 3.17) * mm, "end": v(83.03, 3.05) * mm});
            skLineSegment(sketch, "E1524", {"start": v(83.03, 3.05) * mm, "end": v(82.88, 2.92) * mm});
            skLineSegment(sketch, "E1525", {"start": v(82.88, 2.92) * mm, "end": v(82.7, 2.83) * mm});
            skLineSegment(sketch, "E1526", {"start": v(82.7, 2.83) * mm, "end": v(82.53, 2.75) * mm});
            skLineSegment(sketch, "E1527", {"start": v(82.53, 2.75) * mm, "end": v(82.36, 2.7) * mm});
            skLineSegment(sketch, "E1528", {"start": v(82.36, 2.7) * mm, "end": v(82.18, 2.65) * mm});
            skLineSegment(sketch, "E1529", {"start": v(82.18, 2.65) * mm, "end": v(81.99, 2.63) * mm});
            skLineSegment(sketch, "E1530", {"start": v(81.99, 2.63) * mm, "end": v(81.81, 2.6) * mm});
            skLineSegment(sketch, "E1531", {"start": v(81.81, 2.6) * mm, "end": v(81.61, 2.63) * mm});
            skLineSegment(sketch, "E1532", {"start": v(81.61, 2.63) * mm, "end": v(81.41, 2.65) * mm});
            skLineSegment(sketch, "E1533", {"start": v(81.41, 2.65) * mm, "end": v(81.24, 2.7) * mm});
            skLineSegment(sketch, "E1534", {"start": v(81.24, 2.7) * mm, "end": v(81.07, 2.75) * mm});
            skLineSegment(sketch, "E1535", {"start": v(81.07, 2.75) * mm, "end": v(80.9, 2.83) * mm});
            skLineSegment(sketch, "E1536", {"start": v(80.9, 2.83) * mm, "end": v(80.72, 2.92) * mm});
            skLineSegment(sketch, "E1537", {"start": v(80.72, 2.92) * mm, "end": v(80.57, 3.05) * mm});
            skLineSegment(sketch, "E1538", {"start": v(80.57, 3.05) * mm, "end": v(80.42, 3.17) * mm});
            skLineSegment(sketch, "E1539", {"start": v(80.42, 3.17) * mm, "end": v(80.3, 3.32) * mm});
            skLineSegment(sketch, "E1540", {"start": v(80.3, 3.32) * mm, "end": v(80.17, 3.47) * mm});
            skLineSegment(sketch, "E1541", {"start": v(80.17, 3.47) * mm, "end": v(80.08, 3.64) * mm});
            skLineSegment(sketch, "E1542", {"start": v(80.08, 3.64) * mm, "end": v(80, 3.82) * mm});
            skLineSegment(sketch, "E1543", {"start": v(80, 3.82) * mm, "end": v(79.95, 4) * mm});
            skLineSegment(sketch, "E1544", {"start": v(79.95, 4) * mm, "end": v(79.9, 4.17) * mm});
            skLineSegment(sketch, "E1545", {"start": v(79.9, 4.17) * mm, "end": v(79.88, 4.36) * mm});
            skLineSegment(sketch, "E1546", {"start": v(79.88, 4.36) * mm, "end": v(79.88, 4.54) * mm});
            skLineSegment(sketch, "E1547", {"start": v(79.88, 4.54) * mm, "end": v(79.88, 11.28) * mm});
            skLineSegment(sketch, "E1548", {"start": v(79.88, 11.28) * mm, "end": v(79.85, 11.63) * mm});
            skLineSegment(sketch, "E1549", {"start": v(79.85, 11.63) * mm, "end": v(79.8, 11.98) * mm});
            skLineSegment(sketch, "E1550", {"start": v(79.8, 11.98) * mm, "end": v(79.73, 12.3) * mm});
            skLineSegment(sketch, "E1551", {"start": v(79.73, 12.3) * mm, "end": v(79.63, 12.6) * mm});
            skLineSegment(sketch, "E1552", {"start": v(79.63, 12.6) * mm, "end": v(79.48, 12.9) * mm});
            skLineSegment(sketch, "E1553", {"start": v(79.48, 12.9) * mm, "end": v(79.3, 13.17) * mm});
            skLineSegment(sketch, "E1554", {"start": v(79.3, 13.17) * mm, "end": v(79.1, 13.44) * mm});
            skLineSegment(sketch, "E1555", {"start": v(79.1, 13.44) * mm, "end": v(78.88, 13.7) * mm});
            skLineSegment(sketch, "E1556", {"start": v(78.88, 13.7) * mm, "end": v(78.61, 13.91) * mm});
            skLineSegment(sketch, "E1557", {"start": v(78.61, 13.91) * mm, "end": v(78.34, 14.11) * mm});
            skLineSegment(sketch, "E1558", {"start": v(78.34, 14.11) * mm, "end": v(78.07, 14.29) * mm});
            skLineSegment(sketch, "E1559", {"start": v(78.07, 14.29) * mm, "end": v(77.77, 14.43) * mm});
            skLineSegment(sketch, "E1560", {"start": v(77.77, 14.43) * mm, "end": v(77.47, 14.53) * mm});
            skLineSegment(sketch, "E1561", {"start": v(77.47, 14.53) * mm, "end": v(77.15, 14.6) * mm});
            skLineSegment(sketch, "E1562", {"start": v(77.15, 14.6) * mm, "end": v(76.83, 14.66) * mm});
            skLineSegment(sketch, "E1563", {"start": v(76.83, 14.66) * mm, "end": v(76.48, 14.68) * mm});
            skLineSegment(sketch, "E1564", {"start": v(76.48, 14.68) * mm, "end": v(76.13, 14.66) * mm});
            skLineSegment(sketch, "E1565", {"start": v(76.13, 14.66) * mm, "end": v(75.8, 14.6) * mm});
            skLineSegment(sketch, "E1566", {"start": v(75.8, 14.6) * mm, "end": v(75.49, 14.53) * mm});
            skLineSegment(sketch, "E1567", {"start": v(75.49, 14.53) * mm, "end": v(75.19, 14.43) * mm});
            skLineSegment(sketch, "E1568", {"start": v(75.19, 14.43) * mm, "end": v(74.9, 14.29) * mm});
            skLineSegment(sketch, "E1569", {"start": v(74.9, 14.29) * mm, "end": v(74.62, 14.11) * mm});
            skLineSegment(sketch, "E1570", {"start": v(74.62, 14.11) * mm, "end": v(74.35, 13.91) * mm});
            skLineSegment(sketch, "E1571", {"start": v(74.35, 13.91) * mm, "end": v(74.07, 13.7) * mm});
            skLineSegment(sketch, "E1572", {"start": v(74.07, 13.7) * mm, "end": v(73.85, 13.44) * mm});
            skLineSegment(sketch, "E1573", {"start": v(73.85, 13.44) * mm, "end": v(73.65, 13.17) * mm});
            skLineSegment(sketch, "E1574", {"start": v(73.65, 13.17) * mm, "end": v(73.48, 12.9) * mm});
            skLineSegment(sketch, "E1575", {"start": v(73.48, 12.9) * mm, "end": v(73.33, 12.6) * mm});
            skLineSegment(sketch, "E1576", {"start": v(73.33, 12.6) * mm, "end": v(73.23, 12.3) * mm});
            skLineSegment(sketch, "E1577", {"start": v(73.23, 12.3) * mm, "end": v(73.15, 11.98) * mm});
            skLineSegment(sketch, "E1578", {"start": v(73.15, 11.98) * mm, "end": v(73.1, 11.63) * mm});
            skLineSegment(sketch, "E1579", {"start": v(73.1, 11.63) * mm, "end": v(73.08, 11.28) * mm});
            skLineSegment(sketch, "E1580", {"start": v(73.08, 11.28) * mm, "end": v(73.08, 4.54) * mm});
            skLineSegment(sketch, "E1581", {"start": v(73.08, 4.54) * mm, "end": v(73.08, 4.36) * mm});
            skLineSegment(sketch, "E1582", {"start": v(73.08, 4.36) * mm, "end": v(73.06, 4.17) * mm});
            skLineSegment(sketch, "E1583", {"start": v(73.06, 4.17) * mm, "end": v(73, 4) * mm});
            skLineSegment(sketch, "E1584", {"start": v(73, 4) * mm, "end": v(72.96, 3.82) * mm});
            skLineSegment(sketch, "E1585", {"start": v(72.96, 3.82) * mm, "end": v(72.88, 3.64) * mm});
            skLineSegment(sketch, "E1586", {"start": v(72.88, 3.64) * mm, "end": v(72.78, 3.47) * mm});
            skLineSegment(sketch, "E1587", {"start": v(72.78, 3.47) * mm, "end": v(72.66, 3.32) * mm});
            skLineSegment(sketch, "E1588", {"start": v(72.66, 3.32) * mm, "end": v(72.53, 3.17) * mm});
            skLineSegment(sketch, "E1589", {"start": v(72.53, 3.17) * mm, "end": v(72.39, 3.05) * mm});
            skLineSegment(sketch, "E1590", {"start": v(72.39, 3.05) * mm, "end": v(72.24, 2.92) * mm});
            skLineSegment(sketch, "E1591", {"start": v(72.24, 2.92) * mm, "end": v(72.06, 2.83) * mm});
            skLineSegment(sketch, "E1592", {"start": v(72.06, 2.83) * mm, "end": v(71.89, 2.75) * mm});
            skLineSegment(sketch, "E1593", {"start": v(71.89, 2.75) * mm, "end": v(71.72, 2.7) * mm});
            skLineSegment(sketch, "E1594", {"start": v(71.72, 2.7) * mm, "end": v(71.54, 2.65) * mm});
            skLineSegment(sketch, "E1595", {"start": v(71.54, 2.65) * mm, "end": v(71.34, 2.63) * mm});
            skLineSegment(sketch, "E1596", {"start": v(71.34, 2.63) * mm, "end": v(71.15, 2.6) * mm});
            skLineSegment(sketch, "E1597", {"start": v(71.15, 2.6) * mm, "end": v(70.97, 2.63) * mm});
            skLineSegment(sketch, "E1598", {"start": v(70.97, 2.63) * mm, "end": v(70.77, 2.65) * mm});
            skLineSegment(sketch, "E1599", {"start": v(70.77, 2.65) * mm, "end": v(70.6, 2.7) * mm});
            skLineSegment(sketch, "E1600", {"start": v(70.6, 2.7) * mm, "end": v(70.43, 2.75) * mm});
            skLineSegment(sketch, "E1601", {"start": v(70.43, 2.75) * mm, "end": v(70.25, 2.83) * mm});
            skLineSegment(sketch, "E1602", {"start": v(70.25, 2.83) * mm, "end": v(70.08, 2.92) * mm});
            skLineSegment(sketch, "E1603", {"start": v(70.08, 2.92) * mm, "end": v(69.93, 3.05) * mm});
            skLineSegment(sketch, "E1604", {"start": v(69.93, 3.05) * mm, "end": v(69.78, 3.17) * mm});
            skLineSegment(sketch, "E1605", {"start": v(69.78, 3.17) * mm, "end": v(69.66, 3.32) * mm});
            skLineSegment(sketch, "E1606", {"start": v(69.66, 3.32) * mm, "end": v(69.53, 3.47) * mm});
            skLineSegment(sketch, "E1607", {"start": v(69.53, 3.47) * mm, "end": v(69.43, 3.64) * mm});
            skLineSegment(sketch, "E1608", {"start": v(69.43, 3.64) * mm, "end": v(69.36, 3.82) * mm});
            skLineSegment(sketch, "E1609", {"start": v(69.36, 3.82) * mm, "end": v(69.3, 4) * mm});
            skLineSegment(sketch, "E1610", {"start": v(69.3, 4) * mm, "end": v(69.26, 4.17) * mm});
            skLineSegment(sketch, "E1611", {"start": v(69.26, 4.17) * mm, "end": v(69.24, 4.36) * mm});
            skLineSegment(sketch, "E1612", {"start": v(69.24, 4.36) * mm, "end": v(69.21, 4.54) * mm});
            skLineSegment(sketch, "E1613", {"start": v(69.21, 4.54) * mm, "end": v(69.21, 11.28) * mm});
            skLineSegment(sketch, "E1614", {"start": v(69.21, 11.28) * mm, "end": v(69.26, 12.03) * mm});
            skLineSegment(sketch, "E1615", {"start": v(87.64, -4.62) * mm, "end": v(87.62, -4.42) * mm});
            skLineSegment(sketch, "E1616", {"start": v(87.62, -4.42) * mm, "end": v(87.62, -4.22) * mm});
            skLineSegment(sketch, "E1617", {"start": v(87.62, -4.22) * mm, "end": v(87.62, -4.14) * mm});
            skLineSegment(sketch, "E1618", {"start": v(87.62, -4.14) * mm, "end": v(87.62, -4.07) * mm});
            skLineSegment(sketch, "E1619", {"start": v(87.62, -4.07) * mm, "end": v(87.62, -4) * mm});
            skLineSegment(sketch, "E1620", {"start": v(87.62, -4) * mm, "end": v(87.62, -3.92) * mm});
            skLineSegment(sketch, "E1621", {"start": v(87.62, -3.92) * mm, "end": v(87.64, -3.85) * mm});
            skLineSegment(sketch, "E1622", {"start": v(87.64, -3.85) * mm, "end": v(87.67, -3.8) * mm});
            skLineSegment(sketch, "E1623", {"start": v(87.67, -3.8) * mm, "end": v(87.67, -3.72) * mm});
            skLineSegment(sketch, "E1624", {"start": v(87.67, -3.72) * mm, "end": v(87.7, -3.67) * mm});
            skLineSegment(sketch, "E1625", {"start": v(87.7, -3.67) * mm, "end": v(91.49, 16.12) * mm});
            skLineSegment(sketch, "E1626", {"start": v(91.49, 16.12) * mm, "end": v(91.51, 16.32) * mm});
            skLineSegment(sketch, "E1627", {"start": v(91.51, 16.32) * mm, "end": v(91.56, 16.52) * mm});
            skLineSegment(sketch, "E1628", {"start": v(91.56, 16.52) * mm, "end": v(91.6, 16.7) * mm});
            skLineSegment(sketch, "E1629", {"start": v(91.6, 16.7) * mm, "end": v(91.68, 16.87) * mm});
            skLineSegment(sketch, "E1630", {"start": v(91.68, 16.87) * mm, "end": v(91.76, 17.04) * mm});
            skLineSegment(sketch, "E1631", {"start": v(91.76, 17.04) * mm, "end": v(91.86, 17.19) * mm});
            skLineSegment(sketch, "E1632", {"start": v(91.86, 17.19) * mm, "end": v(91.96, 17.34) * mm});
            skLineSegment(sketch, "E1633", {"start": v(91.96, 17.34) * mm, "end": v(92.08, 17.49) * mm});
            skLineSegment(sketch, "E1634", {"start": v(92.08, 17.49) * mm, "end": v(92.23, 17.6) * mm});
            skLineSegment(sketch, "E1635", {"start": v(92.23, 17.6) * mm, "end": v(92.38, 17.73) * mm});
            skLineSegment(sketch, "E1636", {"start": v(92.38, 17.73) * mm, "end": v(92.53, 17.83) * mm});
            skLineSegment(sketch, "E1637", {"start": v(92.53, 17.83) * mm, "end": v(92.68, 17.9) * mm});
            skLineSegment(sketch, "E1638", {"start": v(92.68, 17.9) * mm, "end": v(92.85, 17.96) * mm});
            skLineSegment(sketch, "E1639", {"start": v(92.85, 17.96) * mm, "end": v(93.02, 18) * mm});
            skLineSegment(sketch, "E1640", {"start": v(93.02, 18) * mm, "end": v(93.22, 18.03) * mm});
            skLineSegment(sketch, "E1641", {"start": v(93.22, 18.03) * mm, "end": v(93.42, 18.03) * mm});
            skLineSegment(sketch, "E1642", {"start": v(93.42, 18.03) * mm, "end": v(93.6, 18.03) * mm});
            skLineSegment(sketch, "E1643", {"start": v(93.6, 18.03) * mm, "end": v(93.8, 18) * mm});
            skLineSegment(sketch, "E1644", {"start": v(93.8, 18) * mm, "end": v(93.97, 17.96) * mm});
            skLineSegment(sketch, "E1645", {"start": v(93.97, 17.96) * mm, "end": v(94.14, 17.9) * mm});
            skLineSegment(sketch, "E1646", {"start": v(94.14, 17.9) * mm, "end": v(94.31, 17.83) * mm});
            skLineSegment(sketch, "E1647", {"start": v(94.31, 17.83) * mm, "end": v(94.49, 17.73) * mm});
            skLineSegment(sketch, "E1648", {"start": v(94.49, 17.73) * mm, "end": v(94.64, 17.6) * mm});
            skLineSegment(sketch, "E1649", {"start": v(94.64, 17.6) * mm, "end": v(94.78, 17.49) * mm});
            skLineSegment(sketch, "E1650", {"start": v(94.78, 17.49) * mm, "end": v(94.9, 17.34) * mm});
            skLineSegment(sketch, "E1651", {"start": v(94.9, 17.34) * mm, "end": v(95.03, 17.19) * mm});
            skLineSegment(sketch, "E1652", {"start": v(95.03, 17.19) * mm, "end": v(95.13, 17.01) * mm});
            skLineSegment(sketch, "E1653", {"start": v(95.13, 17.01) * mm, "end": v(95.2, 16.84) * mm});
            skLineSegment(sketch, "E1654", {"start": v(95.2, 16.84) * mm, "end": v(95.26, 16.67) * mm});
            skLineSegment(sketch, "E1655", {"start": v(95.26, 16.67) * mm, "end": v(95.3, 16.5) * mm});
            skLineSegment(sketch, "E1656", {"start": v(95.3, 16.5) * mm, "end": v(95.33, 16.3) * mm});
            skLineSegment(sketch, "E1657", {"start": v(95.33, 16.3) * mm, "end": v(95.35, 16.1) * mm});
            skLineSegment(sketch, "E1658", {"start": v(95.35, 16.1) * mm, "end": v(95.33, 16.05) * mm});
            skLineSegment(sketch, "E1659", {"start": v(95.33, 16.05) * mm, "end": v(95.33, 15.97) * mm});
            skLineSegment(sketch, "E1660", {"start": v(95.33, 15.97) * mm, "end": v(95.33, 15.9) * mm});
            skLineSegment(sketch, "E1661", {"start": v(95.33, 15.9) * mm, "end": v(95.33, 15.82) * mm});
            skLineSegment(sketch, "E1662", {"start": v(95.33, 15.82) * mm, "end": v(95.33, 15.75) * mm});
            skLineSegment(sketch, "E1663", {"start": v(95.33, 15.75) * mm, "end": v(95.3, 15.67) * mm});
            skLineSegment(sketch, "E1664", {"start": v(95.3, 15.67) * mm, "end": v(95.3, 15.62) * mm});
            skLineSegment(sketch, "E1665", {"start": v(95.3, 15.62) * mm, "end": v(95.3, 15.55) * mm});
            skLineSegment(sketch, "E1666", {"start": v(95.3, 15.55) * mm, "end": v(91.88, -2.28) * mm});
            skLineSegment(sketch, "E1667", {"start": v(91.88, -2.28) * mm, "end": v(98.73, -2.28) * mm});
            skLineSegment(sketch, "E1668", {"start": v(98.73, -2.28) * mm, "end": v(98.73, 10.3) * mm});
            skLineSegment(sketch, "E1669", {"start": v(98.73, 10.3) * mm, "end": v(98.73, 10.47) * mm});
            skLineSegment(sketch, "E1670", {"start": v(98.73, 10.47) * mm, "end": v(98.75, 10.66) * mm});
            skLineSegment(sketch, "E1671", {"start": v(98.75, 10.66) * mm, "end": v(98.8, 10.84) * mm});
            skLineSegment(sketch, "E1672", {"start": v(98.8, 10.84) * mm, "end": v(98.88, 11.01) * mm});
            skLineSegment(sketch, "E1673", {"start": v(98.88, 11.01) * mm, "end": v(98.95, 11.18) * mm});
            skLineSegment(sketch, "E1674", {"start": v(98.95, 11.18) * mm, "end": v(99.05, 11.36) * mm});
            skLineSegment(sketch, "E1675", {"start": v(99.05, 11.36) * mm, "end": v(99.17, 11.5) * mm});
            skLineSegment(sketch, "E1676", {"start": v(99.17, 11.5) * mm, "end": v(99.3, 11.66) * mm});
            skLineSegment(sketch, "E1677", {"start": v(99.3, 11.66) * mm, "end": v(99.45, 11.78) * mm});
            skLineSegment(sketch, "E1678", {"start": v(99.45, 11.78) * mm, "end": v(99.6, 11.9) * mm});
            skLineSegment(sketch, "E1679", {"start": v(99.6, 11.9) * mm, "end": v(99.75, 12) * mm});
            skLineSegment(sketch, "E1680", {"start": v(99.75, 12) * mm, "end": v(99.92, 12.08) * mm});
            skLineSegment(sketch, "E1681", {"start": v(99.92, 12.08) * mm, "end": v(100.1, 12.13) * mm});
            skLineSegment(sketch, "E1682", {"start": v(100.1, 12.13) * mm, "end": v(100.27, 12.18) * mm});
            skLineSegment(sketch, "E1683", {"start": v(100.27, 12.18) * mm, "end": v(100.46, 12.2) * mm});
            skLineSegment(sketch, "E1684", {"start": v(100.46, 12.2) * mm, "end": v(100.66, 12.23) * mm});
            skLineSegment(sketch, "E1685", {"start": v(100.66, 12.23) * mm, "end": v(100.86, 12.2) * mm});
            skLineSegment(sketch, "E1686", {"start": v(100.86, 12.2) * mm, "end": v(101.06, 12.18) * mm});
            skLineSegment(sketch, "E1687", {"start": v(101.06, 12.18) * mm, "end": v(101.23, 12.13) * mm});
            skLineSegment(sketch, "E1688", {"start": v(101.23, 12.13) * mm, "end": v(101.4, 12.08) * mm});
            skLineSegment(sketch, "E1689", {"start": v(101.4, 12.08) * mm, "end": v(101.58, 12) * mm});
            skLineSegment(sketch, "E1690", {"start": v(101.58, 12) * mm, "end": v(101.73, 11.9) * mm});
            skLineSegment(sketch, "E1691", {"start": v(101.73, 11.9) * mm, "end": v(101.88, 11.78) * mm});
            skLineSegment(sketch, "E1692", {"start": v(101.88, 11.78) * mm, "end": v(102.03, 11.66) * mm});
            skLineSegment(sketch, "E1693", {"start": v(102.03, 11.66) * mm, "end": v(102.15, 11.5) * mm});
            skLineSegment(sketch, "E1694", {"start": v(102.15, 11.5) * mm, "end": v(102.28, 11.36) * mm});
            skLineSegment(sketch, "E1695", {"start": v(102.28, 11.36) * mm, "end": v(102.37, 11.18) * mm});
            skLineSegment(sketch, "E1696", {"start": v(102.37, 11.18) * mm, "end": v(102.45, 11.01) * mm});
            skLineSegment(sketch, "E1697", {"start": v(102.45, 11.01) * mm, "end": v(102.52, 10.84) * mm});
            skLineSegment(sketch, "E1698", {"start": v(102.52, 10.84) * mm, "end": v(102.57, 10.66) * mm});
            skLineSegment(sketch, "E1699", {"start": v(102.57, 10.66) * mm, "end": v(102.6, 10.47) * mm});
            skLineSegment(sketch, "E1700", {"start": v(102.6, 10.47) * mm, "end": v(102.6, 10.3) * mm});
            skLineSegment(sketch, "E1701", {"start": v(102.6, 10.3) * mm, "end": v(102.6, -12.93) * mm});
            skLineSegment(sketch, "E1702", {"start": v(102.6, -12.93) * mm, "end": v(102.6, -13.12) * mm});
            skLineSegment(sketch, "E1703", {"start": v(102.6, -13.12) * mm, "end": v(102.57, -13.32) * mm});
            skLineSegment(sketch, "E1704", {"start": v(102.57, -13.32) * mm, "end": v(102.52, -13.5) * mm});
            skLineSegment(sketch, "E1705", {"start": v(102.52, -13.5) * mm, "end": v(102.45, -13.67) * mm});
            skLineSegment(sketch, "E1706", {"start": v(102.45, -13.67) * mm, "end": v(102.37, -13.84) * mm});
            skLineSegment(sketch, "E1707", {"start": v(102.37, -13.84) * mm, "end": v(102.28, -14.02) * mm});
            skLineSegment(sketch, "E1708", {"start": v(102.28, -14.02) * mm, "end": v(102.15, -14.17) * mm});
            skLineSegment(sketch, "E1709", {"start": v(102.15, -14.17) * mm, "end": v(102.03, -14.31) * mm});
            skLineSegment(sketch, "E1710", {"start": v(102.03, -14.31) * mm, "end": v(101.88, -14.44) * mm});
            skLineSegment(sketch, "E1711", {"start": v(101.88, -14.44) * mm, "end": v(101.73, -14.56) * mm});
            skLineSegment(sketch, "E1712", {"start": v(101.73, -14.56) * mm, "end": v(101.58, -14.66) * mm});
            skLineSegment(sketch, "E1713", {"start": v(101.58, -14.66) * mm, "end": v(101.4, -14.74) * mm});
            skLineSegment(sketch, "E1714", {"start": v(101.4, -14.74) * mm, "end": v(101.23, -14.79) * mm});
            skLineSegment(sketch, "E1715", {"start": v(101.23, -14.79) * mm, "end": v(101.06, -14.84) * mm});
            skLineSegment(sketch, "E1716", {"start": v(101.06, -14.84) * mm, "end": v(100.86, -14.86) * mm});
            skLineSegment(sketch, "E1717", {"start": v(100.86, -14.86) * mm, "end": v(100.66, -14.86) * mm});
            skLineSegment(sketch, "E1718", {"start": v(100.66, -14.86) * mm, "end": v(100.46, -14.86) * mm});
            skLineSegment(sketch, "E1719", {"start": v(100.46, -14.86) * mm, "end": v(100.27, -14.84) * mm});
            skLineSegment(sketch, "E1720", {"start": v(100.27, -14.84) * mm, "end": v(100.1, -14.79) * mm});
            skLineSegment(sketch, "E1721", {"start": v(100.1, -14.79) * mm, "end": v(99.92, -14.74) * mm});
            skLineSegment(sketch, "E1722", {"start": v(99.92, -14.74) * mm, "end": v(99.75, -14.66) * mm});
            skLineSegment(sketch, "E1723", {"start": v(99.75, -14.66) * mm, "end": v(99.6, -14.56) * mm});
            skLineSegment(sketch, "E1724", {"start": v(99.6, -14.56) * mm, "end": v(99.45, -14.44) * mm});
            skLineSegment(sketch, "E1725", {"start": v(99.45, -14.44) * mm, "end": v(99.3, -14.31) * mm});
            skLineSegment(sketch, "E1726", {"start": v(99.3, -14.31) * mm, "end": v(99.17, -14.17) * mm});
            skLineSegment(sketch, "E1727", {"start": v(99.17, -14.17) * mm, "end": v(99.05, -14.02) * mm});
            skLineSegment(sketch, "E1728", {"start": v(99.05, -14.02) * mm, "end": v(98.95, -13.84) * mm});
            skLineSegment(sketch, "E1729", {"start": v(98.95, -13.84) * mm, "end": v(98.88, -13.67) * mm});
            skLineSegment(sketch, "E1730", {"start": v(98.88, -13.67) * mm, "end": v(98.8, -13.5) * mm});
            skLineSegment(sketch, "E1731", {"start": v(98.8, -13.5) * mm, "end": v(98.75, -13.32) * mm});
            skLineSegment(sketch, "E1732", {"start": v(98.75, -13.32) * mm, "end": v(98.73, -13.12) * mm});
            skLineSegment(sketch, "E1733", {"start": v(98.73, -13.12) * mm, "end": v(98.73, -12.93) * mm});
            skLineSegment(sketch, "E1734", {"start": v(98.73, -12.93) * mm, "end": v(98.73, -6.15) * mm});
            skLineSegment(sketch, "E1735", {"start": v(98.73, -6.15) * mm, "end": v(89.55, -6.15) * mm});
            skLineSegment(sketch, "E1736", {"start": v(89.55, -6.15) * mm, "end": v(89.35, -6.15) * mm});
            skLineSegment(sketch, "E1737", {"start": v(89.35, -6.15) * mm, "end": v(89.15, -6.13) * mm});
            skLineSegment(sketch, "E1738", {"start": v(89.15, -6.13) * mm, "end": v(88.98, -6.08) * mm});
            skLineSegment(sketch, "E1739", {"start": v(88.98, -6.08) * mm, "end": v(88.8, -6.03) * mm});
            skLineSegment(sketch, "E1740", {"start": v(88.8, -6.03) * mm, "end": v(88.63, -5.93) * mm});
            skLineSegment(sketch, "E1741", {"start": v(88.63, -5.93) * mm, "end": v(88.46, -5.83) * mm});
            skLineSegment(sketch, "E1742", {"start": v(88.46, -5.83) * mm, "end": v(88.31, -5.73) * mm});
            skLineSegment(sketch, "E1743", {"start": v(88.31, -5.73) * mm, "end": v(88.16, -5.58) * mm});
            skLineSegment(sketch, "E1744", {"start": v(88.16, -5.58) * mm, "end": v(88.04, -5.43) * mm});
            skLineSegment(sketch, "E1745", {"start": v(88.04, -5.43) * mm, "end": v(87.91, -5.29) * mm});
            skLineSegment(sketch, "E1746", {"start": v(87.91, -5.29) * mm, "end": v(87.81, -5.11) * mm});
            skLineSegment(sketch, "E1747", {"start": v(87.81, -5.11) * mm, "end": v(87.74, -4.96) * mm});
            skLineSegment(sketch, "E1748", {"start": v(87.74, -4.96) * mm, "end": v(87.7, -4.79) * mm});
            skLineSegment(sketch, "E1749", {"start": v(87.7, -4.79) * mm, "end": v(87.64, -4.62) * mm});
            skSolve(sketch);
        }
        {
            var Q0;
            Q0=makeQuery(id+"F0.imprint","IMPRINT",FACE,{"disambiguationData":[TD([[makeQuery(id+"F0.imprint","IMPRINT",EDGE,{"derivedFrom":sQuery(id+"F0.wireOp",EDGE,"E0")}),1.0]])]});
            extrude(context, id + "F1", {"entities" : qUnion([Q0]), "depth" : 2.03 * mm, "offsetDistance" : 25.4 * mm});
        }
    });
